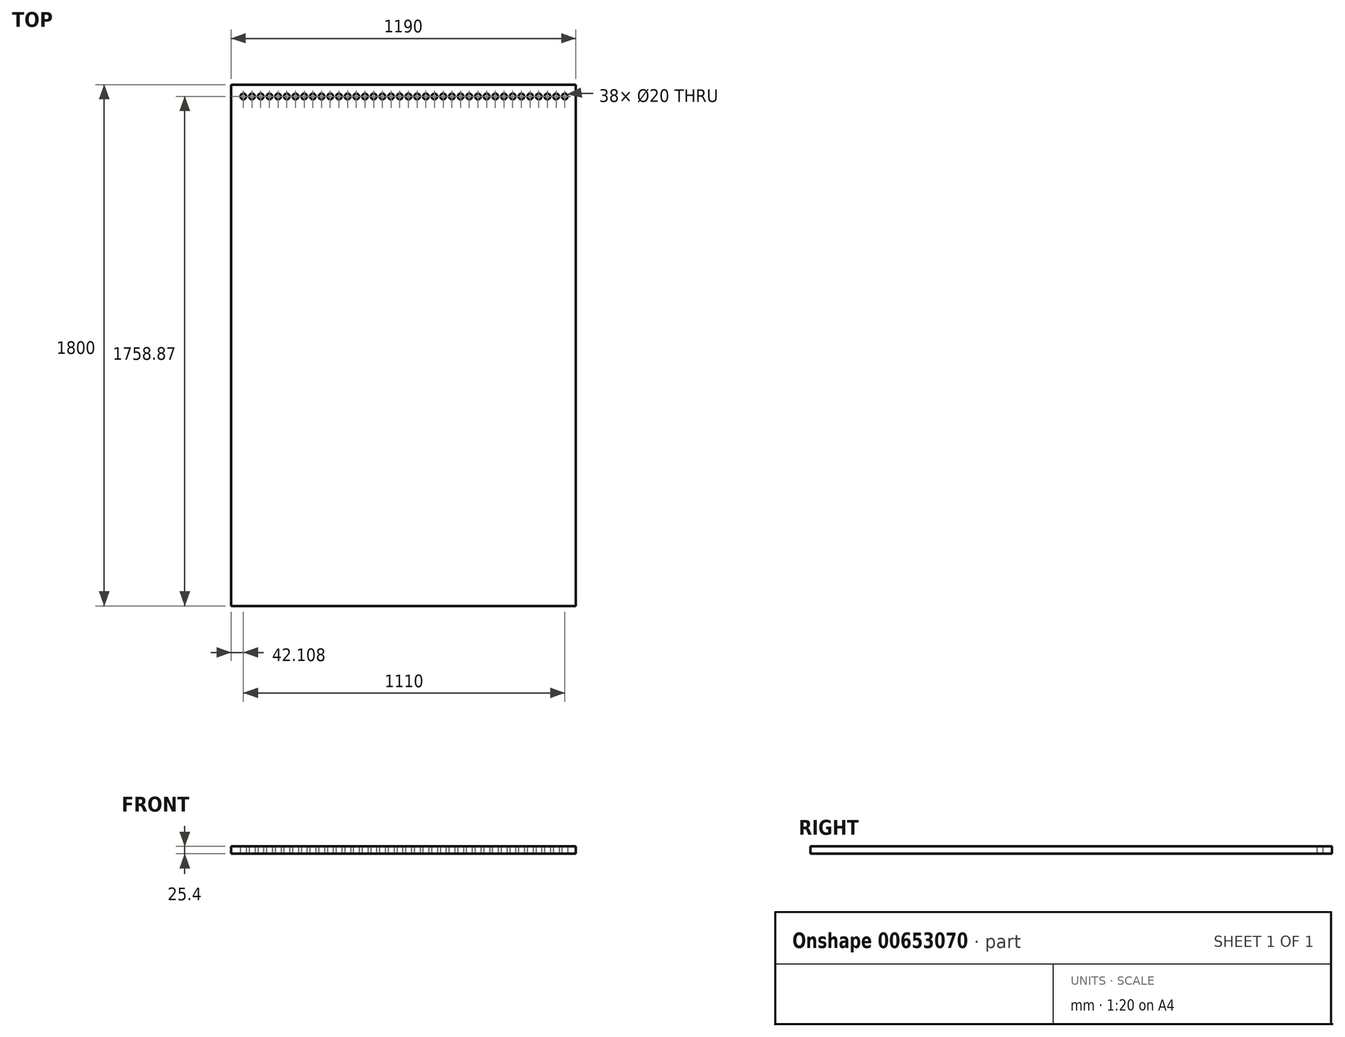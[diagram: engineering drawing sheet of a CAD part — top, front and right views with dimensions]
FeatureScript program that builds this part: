
annotation { "Feature Type Name" : "Feature", "Feature Type Description" : "" }
export const myFeature = defineFeature(function(context is Context, id is Id, definition is map)
    precondition{}
    {
        {
            var Q0;
            Q0=qCreatedBy(makeId("Front.planeOp"),FACE);
            var sketch = newSketch(context, id + "F0", { "sketchPlane" : qUnion([Q0])});
            skLineSegment(sketch, "E0.bottom", {"start": v(0, 0) * mm, "end": v(1190, 0) * mm});
            skLineSegment(sketch, "E0.top", {"start": v(0, 25.4) * mm, "end": v(1190, 25.4) * mm});
            skLineSegment(sketch, "E0.left", {"start": v(0, 0) * mm, "end": v(0, 25.4) * mm});
            skLineSegment(sketch, "E0.right", {"start": v(1190, 0) * mm, "end": v(1190, 25.4) * mm});
            skSolve(sketch);
        }
        {
            var Q0;
            Q0 = qSketchRegion(id + "F0", true);
            extrude(context, id + "F1", {"entities" : qUnion([Q0]), "depth" : 1800 * mm, "offsetDistance" : 25 * mm});
        }
        {
            var Q0;
            Q0=qCreatedBy(makeId("Top.planeOp"),FACE);
            var sketch = newSketch(context, id + "F2", { "sketchPlane" : qUnion([Q0])});
            skPoint(sketch, "E1", {"position": v(42.1, -41.13) * mm});
            skPoint(sketch, "E2.0.1.0", {"position": v(42.1, -66.13) * mm});
            skPoint(sketch, "E2.0.2.0", {"position": v(42.1, -91.13) * mm});
            skPoint(sketch, "E2.0.3.0", {"position": v(42.1, -116.13) * mm});
            skPoint(sketch, "E2.0.4.0", {"position": v(42.1, -141.13) * mm});
            skPoint(sketch, "E2.0.5.0", {"position": v(42.1, -166.13) * mm});
            skPoint(sketch, "E2.0.6.0", {"position": v(42.1, -191.13) * mm});
            skPoint(sketch, "E2.0.7.0", {"position": v(42.1, -216.13) * mm});
            skPoint(sketch, "E2.0.8.0", {"position": v(42.1, -241.13) * mm});
            skPoint(sketch, "E2.0.9.0", {"position": v(42.1, -266.13) * mm});
            skPoint(sketch, "E2.0.10.0", {"position": v(42.1, -291.13) * mm});
            skPoint(sketch, "E2.0.11.0", {"position": v(42.1, -316.13) * mm});
            skPoint(sketch, "E2.0.12.0", {"position": v(42.1, -341.13) * mm});
            skPoint(sketch, "E2.0.13.0", {"position": v(42.1, -366.13) * mm});
            skPoint(sketch, "E2.0.14.0", {"position": v(42.1, -391.13) * mm});
            skPoint(sketch, "E2.0.15.0", {"position": v(42.1, -416.13) * mm});
            skPoint(sketch, "E2.0.16.0", {"position": v(42.1, -441.13) * mm});
            skPoint(sketch, "E2.0.17.0", {"position": v(42.1, -466.13) * mm});
            skPoint(sketch, "E2.0.18.0", {"position": v(42.1, -491.13) * mm});
            skPoint(sketch, "E2.0.19.0", {"position": v(42.1, -516.13) * mm});
            skPoint(sketch, "E2.0.20.0", {"position": v(42.1, -541.13) * mm});
            skPoint(sketch, "E2.0.21.0", {"position": v(42.1, -566.13) * mm});
            skPoint(sketch, "E2.0.22.0", {"position": v(42.1, -591.13) * mm});
            skPoint(sketch, "E2.0.23.0", {"position": v(42.1, -616.13) * mm});
            skPoint(sketch, "E2.0.24.0", {"position": v(42.1, -641.13) * mm});
            skPoint(sketch, "E2.0.25.0", {"position": v(42.1, -666.13) * mm});
            skPoint(sketch, "E2.0.26.0", {"position": v(42.1, -691.13) * mm});
            skPoint(sketch, "E2.0.27.0", {"position": v(42.1, -716.13) * mm});
            skPoint(sketch, "E2.0.28.0", {"position": v(42.1, -741.13) * mm});
            skPoint(sketch, "E2.0.29.0", {"position": v(42.1, -766.13) * mm});
            skPoint(sketch, "E2.0.30.0", {"position": v(42.1, -791.13) * mm});
            skPoint(sketch, "E2.0.31.0", {"position": v(42.1, -816.13) * mm});
            skPoint(sketch, "E2.0.32.0", {"position": v(42.1, -841.13) * mm});
            skPoint(sketch, "E2.0.33.0", {"position": v(42.1, -866.13) * mm});
            skPoint(sketch, "E2.0.34.0", {"position": v(42.1, -891.13) * mm});
            skPoint(sketch, "E2.0.35.0", {"position": v(42.1, -916.13) * mm});
            skPoint(sketch, "E2.0.36.0", {"position": v(42.1, -941.13) * mm});
            skPoint(sketch, "E2.0.37.0", {"position": v(42.1, -966.13) * mm});
            skPoint(sketch, "E2.0.38.0", {"position": v(42.1, -991.13) * mm});
            skPoint(sketch, "E2.0.39.0", {"position": v(42.1, -1016.13) * mm});
            skPoint(sketch, "E2.0.40.0", {"position": v(42.1, -1041.13) * mm});
            skPoint(sketch, "E2.0.41.0", {"position": v(42.1, -1066.13) * mm});
            skPoint(sketch, "E2.0.42.0", {"position": v(42.1, -1091.13) * mm});
            skPoint(sketch, "E2.0.43.0", {"position": v(42.1, -1116.13) * mm});
            skPoint(sketch, "E2.0.44.0", {"position": v(42.1, -1141.13) * mm});
            skPoint(sketch, "E2.0.45.0", {"position": v(42.1, -1166.13) * mm});
            skPoint(sketch, "E2.0.46.0", {"position": v(42.1, -1191.13) * mm});
            skPoint(sketch, "E2.0.47.0", {"position": v(42.1, -1216.13) * mm});
            skPoint(sketch, "E2.0.48.0", {"position": v(42.1, -1241.13) * mm});
            skPoint(sketch, "E2.0.49.0", {"position": v(42.1, -1266.13) * mm});
            skPoint(sketch, "E2.0.50.0", {"position": v(42.1, -1291.13) * mm});
            skPoint(sketch, "E2.0.51.0", {"position": v(42.1, -1316.13) * mm});
            skPoint(sketch, "E2.0.52.0", {"position": v(42.1, -1341.13) * mm});
            skPoint(sketch, "E2.0.53.0", {"position": v(42.1, -1366.13) * mm});
            skPoint(sketch, "E2.0.54.0", {"position": v(42.1, -1391.13) * mm});
            skPoint(sketch, "E2.0.55.0", {"position": v(42.1, -1416.13) * mm});
            skPoint(sketch, "E2.0.56.0", {"position": v(42.1, -1441.13) * mm});
            skPoint(sketch, "E2.0.57.0", {"position": v(42.1, -1466.13) * mm});
            skPoint(sketch, "E2.0.58.0", {"position": v(42.1, -1491.13) * mm});
            skPoint(sketch, "E2.0.59.0", {"position": v(42.1, -1516.13) * mm});
            skPoint(sketch, "E2.0.60.0", {"position": v(42.1, -1541.13) * mm});
            skPoint(sketch, "E2.0.61.0", {"position": v(42.1, -1566.13) * mm});
            skPoint(sketch, "E2.0.62.0", {"position": v(42.1, -1591.13) * mm});
            skPoint(sketch, "E2.0.63.0", {"position": v(42.1, -1616.13) * mm});
            skPoint(sketch, "E2.0.64.0", {"position": v(42.1, -1641.13) * mm});
            skPoint(sketch, "E2.0.65.0", {"position": v(42.1, -1666.13) * mm});
            skPoint(sketch, "E2.0.66.0", {"position": v(42.1, -1691.13) * mm});
            skPoint(sketch, "E2.0.67.0", {"position": v(42.1, -1716.13) * mm});
            skPoint(sketch, "E2.0.68.0", {"position": v(42.1, -1741.13) * mm});
            skPoint(sketch, "E2.1.0.0", {"position": v(72.1, -41.13) * mm});
            skPoint(sketch, "E2.1.1.0", {"position": v(72.1, -66.13) * mm});
            skPoint(sketch, "E2.1.2.0", {"position": v(72.1, -91.13) * mm});
            skPoint(sketch, "E2.1.3.0", {"position": v(72.1, -116.13) * mm});
            skPoint(sketch, "E2.1.4.0", {"position": v(72.1, -141.13) * mm});
            skPoint(sketch, "E2.1.5.0", {"position": v(72.1, -166.13) * mm});
            skPoint(sketch, "E2.1.6.0", {"position": v(72.1, -191.13) * mm});
            skPoint(sketch, "E2.1.7.0", {"position": v(72.1, -216.13) * mm});
            skPoint(sketch, "E2.1.8.0", {"position": v(72.1, -241.13) * mm});
            skPoint(sketch, "E2.1.9.0", {"position": v(72.1, -266.13) * mm});
            skPoint(sketch, "E2.1.10.0", {"position": v(72.1, -291.13) * mm});
            skPoint(sketch, "E2.1.11.0", {"position": v(72.1, -316.13) * mm});
            skPoint(sketch, "E2.1.12.0", {"position": v(72.1, -341.13) * mm});
            skPoint(sketch, "E2.1.13.0", {"position": v(72.1, -366.13) * mm});
            skPoint(sketch, "E2.1.14.0", {"position": v(72.1, -391.13) * mm});
            skPoint(sketch, "E2.1.15.0", {"position": v(72.1, -416.13) * mm});
            skPoint(sketch, "E2.1.16.0", {"position": v(72.1, -441.13) * mm});
            skPoint(sketch, "E2.1.17.0", {"position": v(72.1, -466.13) * mm});
            skPoint(sketch, "E2.1.18.0", {"position": v(72.1, -491.13) * mm});
            skPoint(sketch, "E2.1.19.0", {"position": v(72.1, -516.13) * mm});
            skPoint(sketch, "E2.1.20.0", {"position": v(72.1, -541.13) * mm});
            skPoint(sketch, "E2.1.21.0", {"position": v(72.1, -566.13) * mm});
            skPoint(sketch, "E2.1.22.0", {"position": v(72.1, -591.13) * mm});
            skPoint(sketch, "E2.1.23.0", {"position": v(72.1, -616.13) * mm});
            skPoint(sketch, "E2.1.24.0", {"position": v(72.1, -641.13) * mm});
            skPoint(sketch, "E2.1.25.0", {"position": v(72.1, -666.13) * mm});
            skPoint(sketch, "E2.1.26.0", {"position": v(72.1, -691.13) * mm});
            skPoint(sketch, "E2.1.27.0", {"position": v(72.1, -716.13) * mm});
            skPoint(sketch, "E2.1.28.0", {"position": v(72.1, -741.13) * mm});
            skPoint(sketch, "E2.1.29.0", {"position": v(72.1, -766.13) * mm});
            skPoint(sketch, "E2.1.30.0", {"position": v(72.1, -791.13) * mm});
            skPoint(sketch, "E2.1.31.0", {"position": v(72.1, -816.13) * mm});
            skPoint(sketch, "E2.1.32.0", {"position": v(72.1, -841.13) * mm});
            skPoint(sketch, "E2.1.33.0", {"position": v(72.1, -866.13) * mm});
            skPoint(sketch, "E2.1.34.0", {"position": v(72.1, -891.13) * mm});
            skPoint(sketch, "E2.1.35.0", {"position": v(72.1, -916.13) * mm});
            skPoint(sketch, "E2.1.36.0", {"position": v(72.1, -941.13) * mm});
            skPoint(sketch, "E2.1.37.0", {"position": v(72.1, -966.13) * mm});
            skPoint(sketch, "E2.1.38.0", {"position": v(72.1, -991.13) * mm});
            skPoint(sketch, "E2.1.39.0", {"position": v(72.1, -1016.13) * mm});
            skPoint(sketch, "E2.1.40.0", {"position": v(72.1, -1041.13) * mm});
            skPoint(sketch, "E2.1.41.0", {"position": v(72.1, -1066.13) * mm});
            skPoint(sketch, "E2.1.42.0", {"position": v(72.1, -1091.13) * mm});
            skPoint(sketch, "E2.1.43.0", {"position": v(72.1, -1116.13) * mm});
            skPoint(sketch, "E2.1.44.0", {"position": v(72.1, -1141.13) * mm});
            skPoint(sketch, "E2.1.45.0", {"position": v(72.1, -1166.13) * mm});
            skPoint(sketch, "E2.1.46.0", {"position": v(72.1, -1191.13) * mm});
            skPoint(sketch, "E2.1.47.0", {"position": v(72.1, -1216.13) * mm});
            skPoint(sketch, "E2.1.48.0", {"position": v(72.1, -1241.13) * mm});
            skPoint(sketch, "E2.1.49.0", {"position": v(72.1, -1266.13) * mm});
            skPoint(sketch, "E2.1.50.0", {"position": v(72.1, -1291.13) * mm});
            skPoint(sketch, "E2.1.51.0", {"position": v(72.1, -1316.13) * mm});
            skPoint(sketch, "E2.1.52.0", {"position": v(72.1, -1341.13) * mm});
            skPoint(sketch, "E2.1.53.0", {"position": v(72.1, -1366.13) * mm});
            skPoint(sketch, "E2.1.54.0", {"position": v(72.1, -1391.13) * mm});
            skPoint(sketch, "E2.1.55.0", {"position": v(72.1, -1416.13) * mm});
            skPoint(sketch, "E2.1.56.0", {"position": v(72.1, -1441.13) * mm});
            skPoint(sketch, "E2.1.57.0", {"position": v(72.1, -1466.13) * mm});
            skPoint(sketch, "E2.1.58.0", {"position": v(72.1, -1491.13) * mm});
            skPoint(sketch, "E2.1.59.0", {"position": v(72.1, -1516.13) * mm});
            skPoint(sketch, "E2.1.60.0", {"position": v(72.1, -1541.13) * mm});
            skPoint(sketch, "E2.1.61.0", {"position": v(72.1, -1566.13) * mm});
            skPoint(sketch, "E2.1.62.0", {"position": v(72.1, -1591.13) * mm});
            skPoint(sketch, "E2.1.63.0", {"position": v(72.1, -1616.13) * mm});
            skPoint(sketch, "E2.1.64.0", {"position": v(72.1, -1641.13) * mm});
            skPoint(sketch, "E2.1.65.0", {"position": v(72.1, -1666.13) * mm});
            skPoint(sketch, "E2.1.66.0", {"position": v(72.1, -1691.13) * mm});
            skPoint(sketch, "E2.1.67.0", {"position": v(72.1, -1716.13) * mm});
            skPoint(sketch, "E2.1.68.0", {"position": v(72.1, -1741.13) * mm});
            skPoint(sketch, "E2.2.0.0", {"position": v(102.1, -41.13) * mm});
            skPoint(sketch, "E2.2.1.0", {"position": v(102.1, -66.13) * mm});
            skPoint(sketch, "E2.2.2.0", {"position": v(102.1, -91.13) * mm});
            skPoint(sketch, "E2.2.3.0", {"position": v(102.1, -116.13) * mm});
            skPoint(sketch, "E2.2.4.0", {"position": v(102.1, -141.13) * mm});
            skPoint(sketch, "E2.2.5.0", {"position": v(102.1, -166.13) * mm});
            skPoint(sketch, "E2.2.6.0", {"position": v(102.1, -191.13) * mm});
            skPoint(sketch, "E2.2.7.0", {"position": v(102.1, -216.13) * mm});
            skPoint(sketch, "E2.2.8.0", {"position": v(102.1, -241.13) * mm});
            skPoint(sketch, "E2.2.9.0", {"position": v(102.1, -266.13) * mm});
            skPoint(sketch, "E2.2.10.0", {"position": v(102.1, -291.13) * mm});
            skPoint(sketch, "E2.2.11.0", {"position": v(102.1, -316.13) * mm});
            skPoint(sketch, "E2.2.12.0", {"position": v(102.1, -341.13) * mm});
            skPoint(sketch, "E2.2.13.0", {"position": v(102.1, -366.13) * mm});
            skPoint(sketch, "E2.2.14.0", {"position": v(102.1, -391.13) * mm});
            skPoint(sketch, "E2.2.15.0", {"position": v(102.1, -416.13) * mm});
            skPoint(sketch, "E2.2.16.0", {"position": v(102.1, -441.13) * mm});
            skPoint(sketch, "E2.2.17.0", {"position": v(102.1, -466.13) * mm});
            skPoint(sketch, "E2.2.18.0", {"position": v(102.1, -491.13) * mm});
            skPoint(sketch, "E2.2.19.0", {"position": v(102.1, -516.13) * mm});
            skPoint(sketch, "E2.2.20.0", {"position": v(102.1, -541.13) * mm});
            skPoint(sketch, "E2.2.21.0", {"position": v(102.1, -566.13) * mm});
            skPoint(sketch, "E2.2.22.0", {"position": v(102.1, -591.13) * mm});
            skPoint(sketch, "E2.2.23.0", {"position": v(102.1, -616.13) * mm});
            skPoint(sketch, "E2.2.24.0", {"position": v(102.1, -641.13) * mm});
            skPoint(sketch, "E2.2.25.0", {"position": v(102.1, -666.13) * mm});
            skPoint(sketch, "E2.2.26.0", {"position": v(102.1, -691.13) * mm});
            skPoint(sketch, "E2.2.27.0", {"position": v(102.1, -716.13) * mm});
            skPoint(sketch, "E2.2.28.0", {"position": v(102.1, -741.13) * mm});
            skPoint(sketch, "E2.2.29.0", {"position": v(102.1, -766.13) * mm});
            skPoint(sketch, "E2.2.30.0", {"position": v(102.1, -791.13) * mm});
            skPoint(sketch, "E2.2.31.0", {"position": v(102.1, -816.13) * mm});
            skPoint(sketch, "E2.2.32.0", {"position": v(102.1, -841.13) * mm});
            skPoint(sketch, "E2.2.33.0", {"position": v(102.1, -866.13) * mm});
            skPoint(sketch, "E2.2.34.0", {"position": v(102.1, -891.13) * mm});
            skPoint(sketch, "E2.2.35.0", {"position": v(102.1, -916.13) * mm});
            skPoint(sketch, "E2.2.36.0", {"position": v(102.1, -941.13) * mm});
            skPoint(sketch, "E2.2.37.0", {"position": v(102.1, -966.13) * mm});
            skPoint(sketch, "E2.2.38.0", {"position": v(102.1, -991.13) * mm});
            skPoint(sketch, "E2.2.39.0", {"position": v(102.1, -1016.13) * mm});
            skPoint(sketch, "E2.2.40.0", {"position": v(102.1, -1041.13) * mm});
            skPoint(sketch, "E2.2.41.0", {"position": v(102.1, -1066.13) * mm});
            skPoint(sketch, "E2.2.42.0", {"position": v(102.1, -1091.13) * mm});
            skPoint(sketch, "E2.2.43.0", {"position": v(102.1, -1116.13) * mm});
            skPoint(sketch, "E2.2.44.0", {"position": v(102.1, -1141.13) * mm});
            skPoint(sketch, "E2.2.45.0", {"position": v(102.1, -1166.13) * mm});
            skPoint(sketch, "E2.2.46.0", {"position": v(102.1, -1191.13) * mm});
            skPoint(sketch, "E2.2.47.0", {"position": v(102.1, -1216.13) * mm});
            skPoint(sketch, "E2.2.48.0", {"position": v(102.1, -1241.13) * mm});
            skPoint(sketch, "E2.2.49.0", {"position": v(102.1, -1266.13) * mm});
            skPoint(sketch, "E2.2.50.0", {"position": v(102.1, -1291.13) * mm});
            skPoint(sketch, "E2.2.51.0", {"position": v(102.1, -1316.13) * mm});
            skPoint(sketch, "E2.2.52.0", {"position": v(102.1, -1341.13) * mm});
            skPoint(sketch, "E2.2.53.0", {"position": v(102.1, -1366.13) * mm});
            skPoint(sketch, "E2.2.54.0", {"position": v(102.1, -1391.13) * mm});
            skPoint(sketch, "E2.2.55.0", {"position": v(102.1, -1416.13) * mm});
            skPoint(sketch, "E2.2.56.0", {"position": v(102.1, -1441.13) * mm});
            skPoint(sketch, "E2.2.57.0", {"position": v(102.1, -1466.13) * mm});
            skPoint(sketch, "E2.2.58.0", {"position": v(102.1, -1491.13) * mm});
            skPoint(sketch, "E2.2.59.0", {"position": v(102.1, -1516.13) * mm});
            skPoint(sketch, "E2.2.60.0", {"position": v(102.1, -1541.13) * mm});
            skPoint(sketch, "E2.2.61.0", {"position": v(102.1, -1566.13) * mm});
            skPoint(sketch, "E2.2.62.0", {"position": v(102.1, -1591.13) * mm});
            skPoint(sketch, "E2.2.63.0", {"position": v(102.1, -1616.13) * mm});
            skPoint(sketch, "E2.2.64.0", {"position": v(102.1, -1641.13) * mm});
            skPoint(sketch, "E2.2.65.0", {"position": v(102.1, -1666.13) * mm});
            skPoint(sketch, "E2.2.66.0", {"position": v(102.1, -1691.13) * mm});
            skPoint(sketch, "E2.2.67.0", {"position": v(102.1, -1716.13) * mm});
            skPoint(sketch, "E2.2.68.0", {"position": v(102.1, -1741.13) * mm});
            skPoint(sketch, "E2.3.0.0", {"position": v(132.1, -41.13) * mm});
            skPoint(sketch, "E2.3.1.0", {"position": v(132.1, -66.13) * mm});
            skPoint(sketch, "E2.3.2.0", {"position": v(132.1, -91.13) * mm});
            skPoint(sketch, "E2.3.3.0", {"position": v(132.1, -116.13) * mm});
            skPoint(sketch, "E2.3.4.0", {"position": v(132.1, -141.13) * mm});
            skPoint(sketch, "E2.3.5.0", {"position": v(132.1, -166.13) * mm});
            skPoint(sketch, "E2.3.6.0", {"position": v(132.1, -191.13) * mm});
            skPoint(sketch, "E2.3.7.0", {"position": v(132.1, -216.13) * mm});
            skPoint(sketch, "E2.3.8.0", {"position": v(132.1, -241.13) * mm});
            skPoint(sketch, "E2.3.9.0", {"position": v(132.1, -266.13) * mm});
            skPoint(sketch, "E2.3.10.0", {"position": v(132.1, -291.13) * mm});
            skPoint(sketch, "E2.3.11.0", {"position": v(132.1, -316.13) * mm});
            skPoint(sketch, "E2.3.12.0", {"position": v(132.1, -341.13) * mm});
            skPoint(sketch, "E2.3.13.0", {"position": v(132.1, -366.13) * mm});
            skPoint(sketch, "E2.3.14.0", {"position": v(132.1, -391.13) * mm});
            skPoint(sketch, "E2.3.15.0", {"position": v(132.1, -416.13) * mm});
            skPoint(sketch, "E2.3.16.0", {"position": v(132.1, -441.13) * mm});
            skPoint(sketch, "E2.3.17.0", {"position": v(132.1, -466.13) * mm});
            skPoint(sketch, "E2.3.18.0", {"position": v(132.1, -491.13) * mm});
            skPoint(sketch, "E2.3.19.0", {"position": v(132.1, -516.13) * mm});
            skPoint(sketch, "E2.3.20.0", {"position": v(132.1, -541.13) * mm});
            skPoint(sketch, "E2.3.21.0", {"position": v(132.1, -566.13) * mm});
            skPoint(sketch, "E2.3.22.0", {"position": v(132.1, -591.13) * mm});
            skPoint(sketch, "E2.3.23.0", {"position": v(132.1, -616.13) * mm});
            skPoint(sketch, "E2.3.24.0", {"position": v(132.1, -641.13) * mm});
            skPoint(sketch, "E2.3.25.0", {"position": v(132.1, -666.13) * mm});
            skPoint(sketch, "E2.3.26.0", {"position": v(132.1, -691.13) * mm});
            skPoint(sketch, "E2.3.27.0", {"position": v(132.1, -716.13) * mm});
            skPoint(sketch, "E2.3.28.0", {"position": v(132.1, -741.13) * mm});
            skPoint(sketch, "E2.3.29.0", {"position": v(132.1, -766.13) * mm});
            skPoint(sketch, "E2.3.30.0", {"position": v(132.1, -791.13) * mm});
            skPoint(sketch, "E2.3.31.0", {"position": v(132.1, -816.13) * mm});
            skPoint(sketch, "E2.3.32.0", {"position": v(132.1, -841.13) * mm});
            skPoint(sketch, "E2.3.33.0", {"position": v(132.1, -866.13) * mm});
            skPoint(sketch, "E2.3.34.0", {"position": v(132.1, -891.13) * mm});
            skPoint(sketch, "E2.3.35.0", {"position": v(132.1, -916.13) * mm});
            skPoint(sketch, "E2.3.36.0", {"position": v(132.1, -941.13) * mm});
            skPoint(sketch, "E2.3.37.0", {"position": v(132.1, -966.13) * mm});
            skPoint(sketch, "E2.3.38.0", {"position": v(132.1, -991.13) * mm});
            skPoint(sketch, "E2.3.39.0", {"position": v(132.1, -1016.13) * mm});
            skPoint(sketch, "E2.3.40.0", {"position": v(132.1, -1041.13) * mm});
            skPoint(sketch, "E2.3.41.0", {"position": v(132.1, -1066.13) * mm});
            skPoint(sketch, "E2.3.42.0", {"position": v(132.1, -1091.13) * mm});
            skPoint(sketch, "E2.3.43.0", {"position": v(132.1, -1116.13) * mm});
            skPoint(sketch, "E2.3.44.0", {"position": v(132.1, -1141.13) * mm});
            skPoint(sketch, "E2.3.45.0", {"position": v(132.1, -1166.13) * mm});
            skPoint(sketch, "E2.3.46.0", {"position": v(132.1, -1191.13) * mm});
            skPoint(sketch, "E2.3.47.0", {"position": v(132.1, -1216.13) * mm});
            skPoint(sketch, "E2.3.48.0", {"position": v(132.1, -1241.13) * mm});
            skPoint(sketch, "E2.3.49.0", {"position": v(132.1, -1266.13) * mm});
            skPoint(sketch, "E2.3.50.0", {"position": v(132.1, -1291.13) * mm});
            skPoint(sketch, "E2.3.51.0", {"position": v(132.1, -1316.13) * mm});
            skPoint(sketch, "E2.3.52.0", {"position": v(132.1, -1341.13) * mm});
            skPoint(sketch, "E2.3.53.0", {"position": v(132.1, -1366.13) * mm});
            skPoint(sketch, "E2.3.54.0", {"position": v(132.1, -1391.13) * mm});
            skPoint(sketch, "E2.3.55.0", {"position": v(132.1, -1416.13) * mm});
            skPoint(sketch, "E2.3.56.0", {"position": v(132.1, -1441.13) * mm});
            skPoint(sketch, "E2.3.57.0", {"position": v(132.1, -1466.13) * mm});
            skPoint(sketch, "E2.3.58.0", {"position": v(132.1, -1491.13) * mm});
            skPoint(sketch, "E2.3.59.0", {"position": v(132.1, -1516.13) * mm});
            skPoint(sketch, "E2.3.60.0", {"position": v(132.1, -1541.13) * mm});
            skPoint(sketch, "E2.3.61.0", {"position": v(132.1, -1566.13) * mm});
            skPoint(sketch, "E2.3.62.0", {"position": v(132.1, -1591.13) * mm});
            skPoint(sketch, "E2.3.63.0", {"position": v(132.1, -1616.13) * mm});
            skPoint(sketch, "E2.3.64.0", {"position": v(132.1, -1641.13) * mm});
            skPoint(sketch, "E2.3.65.0", {"position": v(132.1, -1666.13) * mm});
            skPoint(sketch, "E2.3.66.0", {"position": v(132.1, -1691.13) * mm});
            skPoint(sketch, "E2.3.67.0", {"position": v(132.1, -1716.13) * mm});
            skPoint(sketch, "E2.3.68.0", {"position": v(132.1, -1741.13) * mm});
            skPoint(sketch, "E2.4.0.0", {"position": v(162.1, -41.13) * mm});
            skPoint(sketch, "E2.4.1.0", {"position": v(162.1, -66.13) * mm});
            skPoint(sketch, "E2.4.2.0", {"position": v(162.1, -91.13) * mm});
            skPoint(sketch, "E2.4.3.0", {"position": v(162.1, -116.13) * mm});
            skPoint(sketch, "E2.4.4.0", {"position": v(162.1, -141.13) * mm});
            skPoint(sketch, "E2.4.5.0", {"position": v(162.1, -166.13) * mm});
            skPoint(sketch, "E2.4.6.0", {"position": v(162.1, -191.13) * mm});
            skPoint(sketch, "E2.4.7.0", {"position": v(162.1, -216.13) * mm});
            skPoint(sketch, "E2.4.8.0", {"position": v(162.1, -241.13) * mm});
            skPoint(sketch, "E2.4.9.0", {"position": v(162.1, -266.13) * mm});
            skPoint(sketch, "E2.4.10.0", {"position": v(162.1, -291.13) * mm});
            skPoint(sketch, "E2.4.11.0", {"position": v(162.1, -316.13) * mm});
            skPoint(sketch, "E2.4.12.0", {"position": v(162.1, -341.13) * mm});
            skPoint(sketch, "E2.4.13.0", {"position": v(162.1, -366.13) * mm});
            skPoint(sketch, "E2.4.14.0", {"position": v(162.1, -391.13) * mm});
            skPoint(sketch, "E2.4.15.0", {"position": v(162.1, -416.13) * mm});
            skPoint(sketch, "E2.4.16.0", {"position": v(162.1, -441.13) * mm});
            skPoint(sketch, "E2.4.17.0", {"position": v(162.1, -466.13) * mm});
            skPoint(sketch, "E2.4.18.0", {"position": v(162.1, -491.13) * mm});
            skPoint(sketch, "E2.4.19.0", {"position": v(162.1, -516.13) * mm});
            skPoint(sketch, "E2.4.20.0", {"position": v(162.1, -541.13) * mm});
            skPoint(sketch, "E2.4.21.0", {"position": v(162.1, -566.13) * mm});
            skPoint(sketch, "E2.4.22.0", {"position": v(162.1, -591.13) * mm});
            skPoint(sketch, "E2.4.23.0", {"position": v(162.1, -616.13) * mm});
            skPoint(sketch, "E2.4.24.0", {"position": v(162.1, -641.13) * mm});
            skPoint(sketch, "E2.4.25.0", {"position": v(162.1, -666.13) * mm});
            skPoint(sketch, "E2.4.26.0", {"position": v(162.1, -691.13) * mm});
            skPoint(sketch, "E2.4.27.0", {"position": v(162.1, -716.13) * mm});
            skPoint(sketch, "E2.4.28.0", {"position": v(162.1, -741.13) * mm});
            skPoint(sketch, "E2.4.29.0", {"position": v(162.1, -766.13) * mm});
            skPoint(sketch, "E2.4.30.0", {"position": v(162.1, -791.13) * mm});
            skPoint(sketch, "E2.4.31.0", {"position": v(162.1, -816.13) * mm});
            skPoint(sketch, "E2.4.32.0", {"position": v(162.1, -841.13) * mm});
            skPoint(sketch, "E2.4.33.0", {"position": v(162.1, -866.13) * mm});
            skPoint(sketch, "E2.4.34.0", {"position": v(162.1, -891.13) * mm});
            skPoint(sketch, "E2.4.35.0", {"position": v(162.1, -916.13) * mm});
            skPoint(sketch, "E2.4.36.0", {"position": v(162.1, -941.13) * mm});
            skPoint(sketch, "E2.4.37.0", {"position": v(162.1, -966.13) * mm});
            skPoint(sketch, "E2.4.38.0", {"position": v(162.1, -991.13) * mm});
            skPoint(sketch, "E2.4.39.0", {"position": v(162.1, -1016.13) * mm});
            skPoint(sketch, "E2.4.40.0", {"position": v(162.1, -1041.13) * mm});
            skPoint(sketch, "E2.4.41.0", {"position": v(162.1, -1066.13) * mm});
            skPoint(sketch, "E2.4.42.0", {"position": v(162.1, -1091.13) * mm});
            skPoint(sketch, "E2.4.43.0", {"position": v(162.1, -1116.13) * mm});
            skPoint(sketch, "E2.4.44.0", {"position": v(162.1, -1141.13) * mm});
            skPoint(sketch, "E2.4.45.0", {"position": v(162.1, -1166.13) * mm});
            skPoint(sketch, "E2.4.46.0", {"position": v(162.1, -1191.13) * mm});
            skPoint(sketch, "E2.4.47.0", {"position": v(162.1, -1216.13) * mm});
            skPoint(sketch, "E2.4.48.0", {"position": v(162.1, -1241.13) * mm});
            skPoint(sketch, "E2.4.49.0", {"position": v(162.1, -1266.13) * mm});
            skPoint(sketch, "E2.4.50.0", {"position": v(162.1, -1291.13) * mm});
            skPoint(sketch, "E2.4.51.0", {"position": v(162.1, -1316.13) * mm});
            skPoint(sketch, "E2.4.52.0", {"position": v(162.1, -1341.13) * mm});
            skPoint(sketch, "E2.4.53.0", {"position": v(162.1, -1366.13) * mm});
            skPoint(sketch, "E2.4.54.0", {"position": v(162.1, -1391.13) * mm});
            skPoint(sketch, "E2.4.55.0", {"position": v(162.1, -1416.13) * mm});
            skPoint(sketch, "E2.4.56.0", {"position": v(162.1, -1441.13) * mm});
            skPoint(sketch, "E2.4.57.0", {"position": v(162.1, -1466.13) * mm});
            skPoint(sketch, "E2.4.58.0", {"position": v(162.1, -1491.13) * mm});
            skPoint(sketch, "E2.4.59.0", {"position": v(162.1, -1516.13) * mm});
            skPoint(sketch, "E2.4.60.0", {"position": v(162.1, -1541.13) * mm});
            skPoint(sketch, "E2.4.61.0", {"position": v(162.1, -1566.13) * mm});
            skPoint(sketch, "E2.4.62.0", {"position": v(162.1, -1591.13) * mm});
            skPoint(sketch, "E2.4.63.0", {"position": v(162.1, -1616.13) * mm});
            skPoint(sketch, "E2.4.64.0", {"position": v(162.1, -1641.13) * mm});
            skPoint(sketch, "E2.4.65.0", {"position": v(162.1, -1666.13) * mm});
            skPoint(sketch, "E2.4.66.0", {"position": v(162.1, -1691.13) * mm});
            skPoint(sketch, "E2.4.67.0", {"position": v(162.1, -1716.13) * mm});
            skPoint(sketch, "E2.4.68.0", {"position": v(162.1, -1741.13) * mm});
            skPoint(sketch, "E2.5.0.0", {"position": v(192.1, -41.13) * mm});
            skPoint(sketch, "E2.5.1.0", {"position": v(192.1, -66.13) * mm});
            skPoint(sketch, "E2.5.2.0", {"position": v(192.1, -91.13) * mm});
            skPoint(sketch, "E2.5.3.0", {"position": v(192.1, -116.13) * mm});
            skPoint(sketch, "E2.5.4.0", {"position": v(192.1, -141.13) * mm});
            skPoint(sketch, "E2.5.5.0", {"position": v(192.1, -166.13) * mm});
            skPoint(sketch, "E2.5.6.0", {"position": v(192.1, -191.13) * mm});
            skPoint(sketch, "E2.5.7.0", {"position": v(192.1, -216.13) * mm});
            skPoint(sketch, "E2.5.8.0", {"position": v(192.1, -241.13) * mm});
            skPoint(sketch, "E2.5.9.0", {"position": v(192.1, -266.13) * mm});
            skPoint(sketch, "E2.5.10.0", {"position": v(192.1, -291.13) * mm});
            skPoint(sketch, "E2.5.11.0", {"position": v(192.1, -316.13) * mm});
            skPoint(sketch, "E2.5.12.0", {"position": v(192.1, -341.13) * mm});
            skPoint(sketch, "E2.5.13.0", {"position": v(192.1, -366.13) * mm});
            skPoint(sketch, "E2.5.14.0", {"position": v(192.1, -391.13) * mm});
            skPoint(sketch, "E2.5.15.0", {"position": v(192.1, -416.13) * mm});
            skPoint(sketch, "E2.5.16.0", {"position": v(192.1, -441.13) * mm});
            skPoint(sketch, "E2.5.17.0", {"position": v(192.1, -466.13) * mm});
            skPoint(sketch, "E2.5.18.0", {"position": v(192.1, -491.13) * mm});
            skPoint(sketch, "E2.5.19.0", {"position": v(192.1, -516.13) * mm});
            skPoint(sketch, "E2.5.20.0", {"position": v(192.1, -541.13) * mm});
            skPoint(sketch, "E2.5.21.0", {"position": v(192.1, -566.13) * mm});
            skPoint(sketch, "E2.5.22.0", {"position": v(192.1, -591.13) * mm});
            skPoint(sketch, "E2.5.23.0", {"position": v(192.1, -616.13) * mm});
            skPoint(sketch, "E2.5.24.0", {"position": v(192.1, -641.13) * mm});
            skPoint(sketch, "E2.5.25.0", {"position": v(192.1, -666.13) * mm});
            skPoint(sketch, "E2.5.26.0", {"position": v(192.1, -691.13) * mm});
            skPoint(sketch, "E2.5.27.0", {"position": v(192.1, -716.13) * mm});
            skPoint(sketch, "E2.5.28.0", {"position": v(192.1, -741.13) * mm});
            skPoint(sketch, "E2.5.29.0", {"position": v(192.1, -766.13) * mm});
            skPoint(sketch, "E2.5.30.0", {"position": v(192.1, -791.13) * mm});
            skPoint(sketch, "E2.5.31.0", {"position": v(192.1, -816.13) * mm});
            skPoint(sketch, "E2.5.32.0", {"position": v(192.1, -841.13) * mm});
            skPoint(sketch, "E2.5.33.0", {"position": v(192.1, -866.13) * mm});
            skPoint(sketch, "E2.5.34.0", {"position": v(192.1, -891.13) * mm});
            skPoint(sketch, "E2.5.35.0", {"position": v(192.1, -916.13) * mm});
            skPoint(sketch, "E2.5.36.0", {"position": v(192.1, -941.13) * mm});
            skPoint(sketch, "E2.5.37.0", {"position": v(192.1, -966.13) * mm});
            skPoint(sketch, "E2.5.38.0", {"position": v(192.1, -991.13) * mm});
            skPoint(sketch, "E2.5.39.0", {"position": v(192.1, -1016.13) * mm});
            skPoint(sketch, "E2.5.40.0", {"position": v(192.1, -1041.13) * mm});
            skPoint(sketch, "E2.5.41.0", {"position": v(192.1, -1066.13) * mm});
            skPoint(sketch, "E2.5.42.0", {"position": v(192.1, -1091.13) * mm});
            skPoint(sketch, "E2.5.43.0", {"position": v(192.1, -1116.13) * mm});
            skPoint(sketch, "E2.5.44.0", {"position": v(192.1, -1141.13) * mm});
            skPoint(sketch, "E2.5.45.0", {"position": v(192.1, -1166.13) * mm});
            skPoint(sketch, "E2.5.46.0", {"position": v(192.1, -1191.13) * mm});
            skPoint(sketch, "E2.5.47.0", {"position": v(192.1, -1216.13) * mm});
            skPoint(sketch, "E2.5.48.0", {"position": v(192.1, -1241.13) * mm});
            skPoint(sketch, "E2.5.49.0", {"position": v(192.1, -1266.13) * mm});
            skPoint(sketch, "E2.5.50.0", {"position": v(192.1, -1291.13) * mm});
            skPoint(sketch, "E2.5.51.0", {"position": v(192.1, -1316.13) * mm});
            skPoint(sketch, "E2.5.52.0", {"position": v(192.1, -1341.13) * mm});
            skPoint(sketch, "E2.5.53.0", {"position": v(192.1, -1366.13) * mm});
            skPoint(sketch, "E2.5.54.0", {"position": v(192.1, -1391.13) * mm});
            skPoint(sketch, "E2.5.55.0", {"position": v(192.1, -1416.13) * mm});
            skPoint(sketch, "E2.5.56.0", {"position": v(192.1, -1441.13) * mm});
            skPoint(sketch, "E2.5.57.0", {"position": v(192.1, -1466.13) * mm});
            skPoint(sketch, "E2.5.58.0", {"position": v(192.1, -1491.13) * mm});
            skPoint(sketch, "E2.5.59.0", {"position": v(192.1, -1516.13) * mm});
            skPoint(sketch, "E2.5.60.0", {"position": v(192.1, -1541.13) * mm});
            skPoint(sketch, "E2.5.61.0", {"position": v(192.1, -1566.13) * mm});
            skPoint(sketch, "E2.5.62.0", {"position": v(192.1, -1591.13) * mm});
            skPoint(sketch, "E2.5.63.0", {"position": v(192.1, -1616.13) * mm});
            skPoint(sketch, "E2.5.64.0", {"position": v(192.1, -1641.13) * mm});
            skPoint(sketch, "E2.5.65.0", {"position": v(192.1, -1666.13) * mm});
            skPoint(sketch, "E2.5.66.0", {"position": v(192.1, -1691.13) * mm});
            skPoint(sketch, "E2.5.67.0", {"position": v(192.1, -1716.13) * mm});
            skPoint(sketch, "E2.5.68.0", {"position": v(192.1, -1741.13) * mm});
            skPoint(sketch, "E2.6.0.0", {"position": v(222.1, -41.13) * mm});
            skPoint(sketch, "E2.6.1.0", {"position": v(222.1, -66.13) * mm});
            skPoint(sketch, "E2.6.2.0", {"position": v(222.1, -91.13) * mm});
            skPoint(sketch, "E2.6.3.0", {"position": v(222.1, -116.13) * mm});
            skPoint(sketch, "E2.6.4.0", {"position": v(222.1, -141.13) * mm});
            skPoint(sketch, "E2.6.5.0", {"position": v(222.1, -166.13) * mm});
            skPoint(sketch, "E2.6.6.0", {"position": v(222.1, -191.13) * mm});
            skPoint(sketch, "E2.6.7.0", {"position": v(222.1, -216.13) * mm});
            skPoint(sketch, "E2.6.8.0", {"position": v(222.1, -241.13) * mm});
            skPoint(sketch, "E2.6.9.0", {"position": v(222.1, -266.13) * mm});
            skPoint(sketch, "E2.6.10.0", {"position": v(222.1, -291.13) * mm});
            skPoint(sketch, "E2.6.11.0", {"position": v(222.1, -316.13) * mm});
            skPoint(sketch, "E2.6.12.0", {"position": v(222.1, -341.13) * mm});
            skPoint(sketch, "E2.6.13.0", {"position": v(222.1, -366.13) * mm});
            skPoint(sketch, "E2.6.14.0", {"position": v(222.1, -391.13) * mm});
            skPoint(sketch, "E2.6.15.0", {"position": v(222.1, -416.13) * mm});
            skPoint(sketch, "E2.6.16.0", {"position": v(222.1, -441.13) * mm});
            skPoint(sketch, "E2.6.17.0", {"position": v(222.1, -466.13) * mm});
            skPoint(sketch, "E2.6.18.0", {"position": v(222.1, -491.13) * mm});
            skPoint(sketch, "E2.6.19.0", {"position": v(222.1, -516.13) * mm});
            skPoint(sketch, "E2.6.20.0", {"position": v(222.1, -541.13) * mm});
            skPoint(sketch, "E2.6.21.0", {"position": v(222.1, -566.13) * mm});
            skPoint(sketch, "E2.6.22.0", {"position": v(222.1, -591.13) * mm});
            skPoint(sketch, "E2.6.23.0", {"position": v(222.1, -616.13) * mm});
            skPoint(sketch, "E2.6.24.0", {"position": v(222.1, -641.13) * mm});
            skPoint(sketch, "E2.6.25.0", {"position": v(222.1, -666.13) * mm});
            skPoint(sketch, "E2.6.26.0", {"position": v(222.1, -691.13) * mm});
            skPoint(sketch, "E2.6.27.0", {"position": v(222.1, -716.13) * mm});
            skPoint(sketch, "E2.6.28.0", {"position": v(222.1, -741.13) * mm});
            skPoint(sketch, "E2.6.29.0", {"position": v(222.1, -766.13) * mm});
            skPoint(sketch, "E2.6.30.0", {"position": v(222.1, -791.13) * mm});
            skPoint(sketch, "E2.6.31.0", {"position": v(222.1, -816.13) * mm});
            skPoint(sketch, "E2.6.32.0", {"position": v(222.1, -841.13) * mm});
            skPoint(sketch, "E2.6.33.0", {"position": v(222.1, -866.13) * mm});
            skPoint(sketch, "E2.6.34.0", {"position": v(222.1, -891.13) * mm});
            skPoint(sketch, "E2.6.35.0", {"position": v(222.1, -916.13) * mm});
            skPoint(sketch, "E2.6.36.0", {"position": v(222.1, -941.13) * mm});
            skPoint(sketch, "E2.6.37.0", {"position": v(222.1, -966.13) * mm});
            skPoint(sketch, "E2.6.38.0", {"position": v(222.1, -991.13) * mm});
            skPoint(sketch, "E2.6.39.0", {"position": v(222.1, -1016.13) * mm});
            skPoint(sketch, "E2.6.40.0", {"position": v(222.1, -1041.13) * mm});
            skPoint(sketch, "E2.6.41.0", {"position": v(222.1, -1066.13) * mm});
            skPoint(sketch, "E2.6.42.0", {"position": v(222.1, -1091.13) * mm});
            skPoint(sketch, "E2.6.43.0", {"position": v(222.1, -1116.13) * mm});
            skPoint(sketch, "E2.6.44.0", {"position": v(222.1, -1141.13) * mm});
            skPoint(sketch, "E2.6.45.0", {"position": v(222.1, -1166.13) * mm});
            skPoint(sketch, "E2.6.46.0", {"position": v(222.1, -1191.13) * mm});
            skPoint(sketch, "E2.6.47.0", {"position": v(222.1, -1216.13) * mm});
            skPoint(sketch, "E2.6.48.0", {"position": v(222.1, -1241.13) * mm});
            skPoint(sketch, "E2.6.49.0", {"position": v(222.1, -1266.13) * mm});
            skPoint(sketch, "E2.6.50.0", {"position": v(222.1, -1291.13) * mm});
            skPoint(sketch, "E2.6.51.0", {"position": v(222.1, -1316.13) * mm});
            skPoint(sketch, "E2.6.52.0", {"position": v(222.1, -1341.13) * mm});
            skPoint(sketch, "E2.6.53.0", {"position": v(222.1, -1366.13) * mm});
            skPoint(sketch, "E2.6.54.0", {"position": v(222.1, -1391.13) * mm});
            skPoint(sketch, "E2.6.55.0", {"position": v(222.1, -1416.13) * mm});
            skPoint(sketch, "E2.6.56.0", {"position": v(222.1, -1441.13) * mm});
            skPoint(sketch, "E2.6.57.0", {"position": v(222.1, -1466.13) * mm});
            skPoint(sketch, "E2.6.58.0", {"position": v(222.1, -1491.13) * mm});
            skPoint(sketch, "E2.6.59.0", {"position": v(222.1, -1516.13) * mm});
            skPoint(sketch, "E2.6.60.0", {"position": v(222.1, -1541.13) * mm});
            skPoint(sketch, "E2.6.61.0", {"position": v(222.1, -1566.13) * mm});
            skPoint(sketch, "E2.6.62.0", {"position": v(222.1, -1591.13) * mm});
            skPoint(sketch, "E2.6.63.0", {"position": v(222.1, -1616.13) * mm});
            skPoint(sketch, "E2.6.64.0", {"position": v(222.1, -1641.13) * mm});
            skPoint(sketch, "E2.6.65.0", {"position": v(222.1, -1666.13) * mm});
            skPoint(sketch, "E2.6.66.0", {"position": v(222.1, -1691.13) * mm});
            skPoint(sketch, "E2.6.67.0", {"position": v(222.1, -1716.13) * mm});
            skPoint(sketch, "E2.6.68.0", {"position": v(222.1, -1741.13) * mm});
            skPoint(sketch, "E2.7.0.0", {"position": v(252.1, -41.13) * mm});
            skPoint(sketch, "E2.7.1.0", {"position": v(252.1, -66.13) * mm});
            skPoint(sketch, "E2.7.2.0", {"position": v(252.1, -91.13) * mm});
            skPoint(sketch, "E2.7.3.0", {"position": v(252.1, -116.13) * mm});
            skPoint(sketch, "E2.7.4.0", {"position": v(252.1, -141.13) * mm});
            skPoint(sketch, "E2.7.5.0", {"position": v(252.1, -166.13) * mm});
            skPoint(sketch, "E2.7.6.0", {"position": v(252.1, -191.13) * mm});
            skPoint(sketch, "E2.7.7.0", {"position": v(252.1, -216.13) * mm});
            skPoint(sketch, "E2.7.8.0", {"position": v(252.1, -241.13) * mm});
            skPoint(sketch, "E2.7.9.0", {"position": v(252.1, -266.13) * mm});
            skPoint(sketch, "E2.7.10.0", {"position": v(252.1, -291.13) * mm});
            skPoint(sketch, "E2.7.11.0", {"position": v(252.1, -316.13) * mm});
            skPoint(sketch, "E2.7.12.0", {"position": v(252.1, -341.13) * mm});
            skPoint(sketch, "E2.7.13.0", {"position": v(252.1, -366.13) * mm});
            skPoint(sketch, "E2.7.14.0", {"position": v(252.1, -391.13) * mm});
            skPoint(sketch, "E2.7.15.0", {"position": v(252.1, -416.13) * mm});
            skPoint(sketch, "E2.7.16.0", {"position": v(252.1, -441.13) * mm});
            skPoint(sketch, "E2.7.17.0", {"position": v(252.1, -466.13) * mm});
            skPoint(sketch, "E2.7.18.0", {"position": v(252.1, -491.13) * mm});
            skPoint(sketch, "E2.7.19.0", {"position": v(252.1, -516.13) * mm});
            skPoint(sketch, "E2.7.20.0", {"position": v(252.1, -541.13) * mm});
            skPoint(sketch, "E2.7.21.0", {"position": v(252.1, -566.13) * mm});
            skPoint(sketch, "E2.7.22.0", {"position": v(252.1, -591.13) * mm});
            skPoint(sketch, "E2.7.23.0", {"position": v(252.1, -616.13) * mm});
            skPoint(sketch, "E2.7.24.0", {"position": v(252.1, -641.13) * mm});
            skPoint(sketch, "E2.7.25.0", {"position": v(252.1, -666.13) * mm});
            skPoint(sketch, "E2.7.26.0", {"position": v(252.1, -691.13) * mm});
            skPoint(sketch, "E2.7.27.0", {"position": v(252.1, -716.13) * mm});
            skPoint(sketch, "E2.7.28.0", {"position": v(252.1, -741.13) * mm});
            skPoint(sketch, "E2.7.29.0", {"position": v(252.1, -766.13) * mm});
            skPoint(sketch, "E2.7.30.0", {"position": v(252.1, -791.13) * mm});
            skPoint(sketch, "E2.7.31.0", {"position": v(252.1, -816.13) * mm});
            skPoint(sketch, "E2.7.32.0", {"position": v(252.1, -841.13) * mm});
            skPoint(sketch, "E2.7.33.0", {"position": v(252.1, -866.13) * mm});
            skPoint(sketch, "E2.7.34.0", {"position": v(252.1, -891.13) * mm});
            skPoint(sketch, "E2.7.35.0", {"position": v(252.1, -916.13) * mm});
            skPoint(sketch, "E2.7.36.0", {"position": v(252.1, -941.13) * mm});
            skPoint(sketch, "E2.7.37.0", {"position": v(252.1, -966.13) * mm});
            skPoint(sketch, "E2.7.38.0", {"position": v(252.1, -991.13) * mm});
            skPoint(sketch, "E2.7.39.0", {"position": v(252.1, -1016.13) * mm});
            skPoint(sketch, "E2.7.40.0", {"position": v(252.1, -1041.13) * mm});
            skPoint(sketch, "E2.7.41.0", {"position": v(252.1, -1066.13) * mm});
            skPoint(sketch, "E2.7.42.0", {"position": v(252.1, -1091.13) * mm});
            skPoint(sketch, "E2.7.43.0", {"position": v(252.1, -1116.13) * mm});
            skPoint(sketch, "E2.7.44.0", {"position": v(252.1, -1141.13) * mm});
            skPoint(sketch, "E2.7.45.0", {"position": v(252.1, -1166.13) * mm});
            skPoint(sketch, "E2.7.46.0", {"position": v(252.1, -1191.13) * mm});
            skPoint(sketch, "E2.7.47.0", {"position": v(252.1, -1216.13) * mm});
            skPoint(sketch, "E2.7.48.0", {"position": v(252.1, -1241.13) * mm});
            skPoint(sketch, "E2.7.49.0", {"position": v(252.1, -1266.13) * mm});
            skPoint(sketch, "E2.7.50.0", {"position": v(252.1, -1291.13) * mm});
            skPoint(sketch, "E2.7.51.0", {"position": v(252.1, -1316.13) * mm});
            skPoint(sketch, "E2.7.52.0", {"position": v(252.1, -1341.13) * mm});
            skPoint(sketch, "E2.7.53.0", {"position": v(252.1, -1366.13) * mm});
            skPoint(sketch, "E2.7.54.0", {"position": v(252.1, -1391.13) * mm});
            skPoint(sketch, "E2.7.55.0", {"position": v(252.1, -1416.13) * mm});
            skPoint(sketch, "E2.7.56.0", {"position": v(252.1, -1441.13) * mm});
            skPoint(sketch, "E2.7.57.0", {"position": v(252.1, -1466.13) * mm});
            skPoint(sketch, "E2.7.58.0", {"position": v(252.1, -1491.13) * mm});
            skPoint(sketch, "E2.7.59.0", {"position": v(252.1, -1516.13) * mm});
            skPoint(sketch, "E2.7.60.0", {"position": v(252.1, -1541.13) * mm});
            skPoint(sketch, "E2.7.61.0", {"position": v(252.1, -1566.13) * mm});
            skPoint(sketch, "E2.7.62.0", {"position": v(252.1, -1591.13) * mm});
            skPoint(sketch, "E2.7.63.0", {"position": v(252.1, -1616.13) * mm});
            skPoint(sketch, "E2.7.64.0", {"position": v(252.1, -1641.13) * mm});
            skPoint(sketch, "E2.7.65.0", {"position": v(252.1, -1666.13) * mm});
            skPoint(sketch, "E2.7.66.0", {"position": v(252.1, -1691.13) * mm});
            skPoint(sketch, "E2.7.67.0", {"position": v(252.1, -1716.13) * mm});
            skPoint(sketch, "E2.7.68.0", {"position": v(252.1, -1741.13) * mm});
            skPoint(sketch, "E2.8.0.0", {"position": v(282.1, -41.13) * mm});
            skPoint(sketch, "E2.8.1.0", {"position": v(282.1, -66.13) * mm});
            skPoint(sketch, "E2.8.2.0", {"position": v(282.1, -91.13) * mm});
            skPoint(sketch, "E2.8.3.0", {"position": v(282.1, -116.13) * mm});
            skPoint(sketch, "E2.8.4.0", {"position": v(282.1, -141.13) * mm});
            skPoint(sketch, "E2.8.5.0", {"position": v(282.1, -166.13) * mm});
            skPoint(sketch, "E2.8.6.0", {"position": v(282.1, -191.13) * mm});
            skPoint(sketch, "E2.8.7.0", {"position": v(282.1, -216.13) * mm});
            skPoint(sketch, "E2.8.8.0", {"position": v(282.1, -241.13) * mm});
            skPoint(sketch, "E2.8.9.0", {"position": v(282.1, -266.13) * mm});
            skPoint(sketch, "E2.8.10.0", {"position": v(282.1, -291.13) * mm});
            skPoint(sketch, "E2.8.11.0", {"position": v(282.1, -316.13) * mm});
            skPoint(sketch, "E2.8.12.0", {"position": v(282.1, -341.13) * mm});
            skPoint(sketch, "E2.8.13.0", {"position": v(282.1, -366.13) * mm});
            skPoint(sketch, "E2.8.14.0", {"position": v(282.1, -391.13) * mm});
            skPoint(sketch, "E2.8.15.0", {"position": v(282.1, -416.13) * mm});
            skPoint(sketch, "E2.8.16.0", {"position": v(282.1, -441.13) * mm});
            skPoint(sketch, "E2.8.17.0", {"position": v(282.1, -466.13) * mm});
            skPoint(sketch, "E2.8.18.0", {"position": v(282.1, -491.13) * mm});
            skPoint(sketch, "E2.8.19.0", {"position": v(282.1, -516.13) * mm});
            skPoint(sketch, "E2.8.20.0", {"position": v(282.1, -541.13) * mm});
            skPoint(sketch, "E2.8.21.0", {"position": v(282.1, -566.13) * mm});
            skPoint(sketch, "E2.8.22.0", {"position": v(282.1, -591.13) * mm});
            skPoint(sketch, "E2.8.23.0", {"position": v(282.1, -616.13) * mm});
            skPoint(sketch, "E2.8.24.0", {"position": v(282.1, -641.13) * mm});
            skPoint(sketch, "E2.8.25.0", {"position": v(282.1, -666.13) * mm});
            skPoint(sketch, "E2.8.26.0", {"position": v(282.1, -691.13) * mm});
            skPoint(sketch, "E2.8.27.0", {"position": v(282.1, -716.13) * mm});
            skPoint(sketch, "E2.8.28.0", {"position": v(282.1, -741.13) * mm});
            skPoint(sketch, "E2.8.29.0", {"position": v(282.1, -766.13) * mm});
            skPoint(sketch, "E2.8.30.0", {"position": v(282.1, -791.13) * mm});
            skPoint(sketch, "E2.8.31.0", {"position": v(282.1, -816.13) * mm});
            skPoint(sketch, "E2.8.32.0", {"position": v(282.1, -841.13) * mm});
            skPoint(sketch, "E2.8.33.0", {"position": v(282.1, -866.13) * mm});
            skPoint(sketch, "E2.8.34.0", {"position": v(282.1, -891.13) * mm});
            skPoint(sketch, "E2.8.35.0", {"position": v(282.1, -916.13) * mm});
            skPoint(sketch, "E2.8.36.0", {"position": v(282.1, -941.13) * mm});
            skPoint(sketch, "E2.8.37.0", {"position": v(282.1, -966.13) * mm});
            skPoint(sketch, "E2.8.38.0", {"position": v(282.1, -991.13) * mm});
            skPoint(sketch, "E2.8.39.0", {"position": v(282.1, -1016.13) * mm});
            skPoint(sketch, "E2.8.40.0", {"position": v(282.1, -1041.13) * mm});
            skPoint(sketch, "E2.8.41.0", {"position": v(282.1, -1066.13) * mm});
            skPoint(sketch, "E2.8.42.0", {"position": v(282.1, -1091.13) * mm});
            skPoint(sketch, "E2.8.43.0", {"position": v(282.1, -1116.13) * mm});
            skPoint(sketch, "E2.8.44.0", {"position": v(282.1, -1141.13) * mm});
            skPoint(sketch, "E2.8.45.0", {"position": v(282.1, -1166.13) * mm});
            skPoint(sketch, "E2.8.46.0", {"position": v(282.1, -1191.13) * mm});
            skPoint(sketch, "E2.8.47.0", {"position": v(282.1, -1216.13) * mm});
            skPoint(sketch, "E2.8.48.0", {"position": v(282.1, -1241.13) * mm});
            skPoint(sketch, "E2.8.49.0", {"position": v(282.1, -1266.13) * mm});
            skPoint(sketch, "E2.8.50.0", {"position": v(282.1, -1291.13) * mm});
            skPoint(sketch, "E2.8.51.0", {"position": v(282.1, -1316.13) * mm});
            skPoint(sketch, "E2.8.52.0", {"position": v(282.1, -1341.13) * mm});
            skPoint(sketch, "E2.8.53.0", {"position": v(282.1, -1366.13) * mm});
            skPoint(sketch, "E2.8.54.0", {"position": v(282.1, -1391.13) * mm});
            skPoint(sketch, "E2.8.55.0", {"position": v(282.1, -1416.13) * mm});
            skPoint(sketch, "E2.8.56.0", {"position": v(282.1, -1441.13) * mm});
            skPoint(sketch, "E2.8.57.0", {"position": v(282.1, -1466.13) * mm});
            skPoint(sketch, "E2.8.58.0", {"position": v(282.1, -1491.13) * mm});
            skPoint(sketch, "E2.8.59.0", {"position": v(282.1, -1516.13) * mm});
            skPoint(sketch, "E2.8.60.0", {"position": v(282.1, -1541.13) * mm});
            skPoint(sketch, "E2.8.61.0", {"position": v(282.1, -1566.13) * mm});
            skPoint(sketch, "E2.8.62.0", {"position": v(282.1, -1591.13) * mm});
            skPoint(sketch, "E2.8.63.0", {"position": v(282.1, -1616.13) * mm});
            skPoint(sketch, "E2.8.64.0", {"position": v(282.1, -1641.13) * mm});
            skPoint(sketch, "E2.8.65.0", {"position": v(282.1, -1666.13) * mm});
            skPoint(sketch, "E2.8.66.0", {"position": v(282.1, -1691.13) * mm});
            skPoint(sketch, "E2.8.67.0", {"position": v(282.1, -1716.13) * mm});
            skPoint(sketch, "E2.8.68.0", {"position": v(282.1, -1741.13) * mm});
            skPoint(sketch, "E2.9.0.0", {"position": v(312.1, -41.13) * mm});
            skPoint(sketch, "E2.9.1.0", {"position": v(312.1, -66.13) * mm});
            skPoint(sketch, "E2.9.2.0", {"position": v(312.1, -91.13) * mm});
            skPoint(sketch, "E2.9.3.0", {"position": v(312.1, -116.13) * mm});
            skPoint(sketch, "E2.9.4.0", {"position": v(312.1, -141.13) * mm});
            skPoint(sketch, "E2.9.5.0", {"position": v(312.1, -166.13) * mm});
            skPoint(sketch, "E2.9.6.0", {"position": v(312.1, -191.13) * mm});
            skPoint(sketch, "E2.9.7.0", {"position": v(312.1, -216.13) * mm});
            skPoint(sketch, "E2.9.8.0", {"position": v(312.1, -241.13) * mm});
            skPoint(sketch, "E2.9.9.0", {"position": v(312.1, -266.13) * mm});
            skPoint(sketch, "E2.9.10.0", {"position": v(312.1, -291.13) * mm});
            skPoint(sketch, "E2.9.11.0", {"position": v(312.1, -316.13) * mm});
            skPoint(sketch, "E2.9.12.0", {"position": v(312.1, -341.13) * mm});
            skPoint(sketch, "E2.9.13.0", {"position": v(312.1, -366.13) * mm});
            skPoint(sketch, "E2.9.14.0", {"position": v(312.1, -391.13) * mm});
            skPoint(sketch, "E2.9.15.0", {"position": v(312.1, -416.13) * mm});
            skPoint(sketch, "E2.9.16.0", {"position": v(312.1, -441.13) * mm});
            skPoint(sketch, "E2.9.17.0", {"position": v(312.1, -466.13) * mm});
            skPoint(sketch, "E2.9.18.0", {"position": v(312.1, -491.13) * mm});
            skPoint(sketch, "E2.9.19.0", {"position": v(312.1, -516.13) * mm});
            skPoint(sketch, "E2.9.20.0", {"position": v(312.1, -541.13) * mm});
            skPoint(sketch, "E2.9.21.0", {"position": v(312.1, -566.13) * mm});
            skPoint(sketch, "E2.9.22.0", {"position": v(312.1, -591.13) * mm});
            skPoint(sketch, "E2.9.23.0", {"position": v(312.1, -616.13) * mm});
            skPoint(sketch, "E2.9.24.0", {"position": v(312.1, -641.13) * mm});
            skPoint(sketch, "E2.9.25.0", {"position": v(312.1, -666.13) * mm});
            skPoint(sketch, "E2.9.26.0", {"position": v(312.1, -691.13) * mm});
            skPoint(sketch, "E2.9.27.0", {"position": v(312.1, -716.13) * mm});
            skPoint(sketch, "E2.9.28.0", {"position": v(312.1, -741.13) * mm});
            skPoint(sketch, "E2.9.29.0", {"position": v(312.1, -766.13) * mm});
            skPoint(sketch, "E2.9.30.0", {"position": v(312.1, -791.13) * mm});
            skPoint(sketch, "E2.9.31.0", {"position": v(312.1, -816.13) * mm});
            skPoint(sketch, "E2.9.32.0", {"position": v(312.1, -841.13) * mm});
            skPoint(sketch, "E2.9.33.0", {"position": v(312.1, -866.13) * mm});
            skPoint(sketch, "E2.9.34.0", {"position": v(312.1, -891.13) * mm});
            skPoint(sketch, "E2.9.35.0", {"position": v(312.1, -916.13) * mm});
            skPoint(sketch, "E2.9.36.0", {"position": v(312.1, -941.13) * mm});
            skPoint(sketch, "E2.9.37.0", {"position": v(312.1, -966.13) * mm});
            skPoint(sketch, "E2.9.38.0", {"position": v(312.1, -991.13) * mm});
            skPoint(sketch, "E2.9.39.0", {"position": v(312.1, -1016.13) * mm});
            skPoint(sketch, "E2.9.40.0", {"position": v(312.1, -1041.13) * mm});
            skPoint(sketch, "E2.9.41.0", {"position": v(312.1, -1066.13) * mm});
            skPoint(sketch, "E2.9.42.0", {"position": v(312.1, -1091.13) * mm});
            skPoint(sketch, "E2.9.43.0", {"position": v(312.1, -1116.13) * mm});
            skPoint(sketch, "E2.9.44.0", {"position": v(312.1, -1141.13) * mm});
            skPoint(sketch, "E2.9.45.0", {"position": v(312.1, -1166.13) * mm});
            skPoint(sketch, "E2.9.46.0", {"position": v(312.1, -1191.13) * mm});
            skPoint(sketch, "E2.9.47.0", {"position": v(312.1, -1216.13) * mm});
            skPoint(sketch, "E2.9.48.0", {"position": v(312.1, -1241.13) * mm});
            skPoint(sketch, "E2.9.49.0", {"position": v(312.1, -1266.13) * mm});
            skPoint(sketch, "E2.9.50.0", {"position": v(312.1, -1291.13) * mm});
            skPoint(sketch, "E2.9.51.0", {"position": v(312.1, -1316.13) * mm});
            skPoint(sketch, "E2.9.52.0", {"position": v(312.1, -1341.13) * mm});
            skPoint(sketch, "E2.9.53.0", {"position": v(312.1, -1366.13) * mm});
            skPoint(sketch, "E2.9.54.0", {"position": v(312.1, -1391.13) * mm});
            skPoint(sketch, "E2.9.55.0", {"position": v(312.1, -1416.13) * mm});
            skPoint(sketch, "E2.9.56.0", {"position": v(312.1, -1441.13) * mm});
            skPoint(sketch, "E2.9.57.0", {"position": v(312.1, -1466.13) * mm});
            skPoint(sketch, "E2.9.58.0", {"position": v(312.1, -1491.13) * mm});
            skPoint(sketch, "E2.9.59.0", {"position": v(312.1, -1516.13) * mm});
            skPoint(sketch, "E2.9.60.0", {"position": v(312.1, -1541.13) * mm});
            skPoint(sketch, "E2.9.61.0", {"position": v(312.1, -1566.13) * mm});
            skPoint(sketch, "E2.9.62.0", {"position": v(312.1, -1591.13) * mm});
            skPoint(sketch, "E2.9.63.0", {"position": v(312.1, -1616.13) * mm});
            skPoint(sketch, "E2.9.64.0", {"position": v(312.1, -1641.13) * mm});
            skPoint(sketch, "E2.9.65.0", {"position": v(312.1, -1666.13) * mm});
            skPoint(sketch, "E2.9.66.0", {"position": v(312.1, -1691.13) * mm});
            skPoint(sketch, "E2.9.67.0", {"position": v(312.1, -1716.13) * mm});
            skPoint(sketch, "E2.9.68.0", {"position": v(312.1, -1741.13) * mm});
            skPoint(sketch, "E2.10.0.0", {"position": v(342.1, -41.13) * mm});
            skPoint(sketch, "E2.10.1.0", {"position": v(342.1, -66.13) * mm});
            skPoint(sketch, "E2.10.2.0", {"position": v(342.1, -91.13) * mm});
            skPoint(sketch, "E2.10.3.0", {"position": v(342.1, -116.13) * mm});
            skPoint(sketch, "E2.10.4.0", {"position": v(342.1, -141.13) * mm});
            skPoint(sketch, "E2.10.5.0", {"position": v(342.1, -166.13) * mm});
            skPoint(sketch, "E2.10.6.0", {"position": v(342.1, -191.13) * mm});
            skPoint(sketch, "E2.10.7.0", {"position": v(342.1, -216.13) * mm});
            skPoint(sketch, "E2.10.8.0", {"position": v(342.1, -241.13) * mm});
            skPoint(sketch, "E2.10.9.0", {"position": v(342.1, -266.13) * mm});
            skPoint(sketch, "E2.10.10.0", {"position": v(342.1, -291.13) * mm});
            skPoint(sketch, "E2.10.11.0", {"position": v(342.1, -316.13) * mm});
            skPoint(sketch, "E2.10.12.0", {"position": v(342.1, -341.13) * mm});
            skPoint(sketch, "E2.10.13.0", {"position": v(342.1, -366.13) * mm});
            skPoint(sketch, "E2.10.14.0", {"position": v(342.1, -391.13) * mm});
            skPoint(sketch, "E2.10.15.0", {"position": v(342.1, -416.13) * mm});
            skPoint(sketch, "E2.10.16.0", {"position": v(342.1, -441.13) * mm});
            skPoint(sketch, "E2.10.17.0", {"position": v(342.1, -466.13) * mm});
            skPoint(sketch, "E2.10.18.0", {"position": v(342.1, -491.13) * mm});
            skPoint(sketch, "E2.10.19.0", {"position": v(342.1, -516.13) * mm});
            skPoint(sketch, "E2.10.20.0", {"position": v(342.1, -541.13) * mm});
            skPoint(sketch, "E2.10.21.0", {"position": v(342.1, -566.13) * mm});
            skPoint(sketch, "E2.10.22.0", {"position": v(342.1, -591.13) * mm});
            skPoint(sketch, "E2.10.23.0", {"position": v(342.1, -616.13) * mm});
            skPoint(sketch, "E2.10.24.0", {"position": v(342.1, -641.13) * mm});
            skPoint(sketch, "E2.10.25.0", {"position": v(342.1, -666.13) * mm});
            skPoint(sketch, "E2.10.26.0", {"position": v(342.1, -691.13) * mm});
            skPoint(sketch, "E2.10.27.0", {"position": v(342.1, -716.13) * mm});
            skPoint(sketch, "E2.10.28.0", {"position": v(342.1, -741.13) * mm});
            skPoint(sketch, "E2.10.29.0", {"position": v(342.1, -766.13) * mm});
            skPoint(sketch, "E2.10.30.0", {"position": v(342.1, -791.13) * mm});
            skPoint(sketch, "E2.10.31.0", {"position": v(342.1, -816.13) * mm});
            skPoint(sketch, "E2.10.32.0", {"position": v(342.1, -841.13) * mm});
            skPoint(sketch, "E2.10.33.0", {"position": v(342.1, -866.13) * mm});
            skPoint(sketch, "E2.10.34.0", {"position": v(342.1, -891.13) * mm});
            skPoint(sketch, "E2.10.35.0", {"position": v(342.1, -916.13) * mm});
            skPoint(sketch, "E2.10.36.0", {"position": v(342.1, -941.13) * mm});
            skPoint(sketch, "E2.10.37.0", {"position": v(342.1, -966.13) * mm});
            skPoint(sketch, "E2.10.38.0", {"position": v(342.1, -991.13) * mm});
            skPoint(sketch, "E2.10.39.0", {"position": v(342.1, -1016.13) * mm});
            skPoint(sketch, "E2.10.40.0", {"position": v(342.1, -1041.13) * mm});
            skPoint(sketch, "E2.10.41.0", {"position": v(342.1, -1066.13) * mm});
            skPoint(sketch, "E2.10.42.0", {"position": v(342.1, -1091.13) * mm});
            skPoint(sketch, "E2.10.43.0", {"position": v(342.1, -1116.13) * mm});
            skPoint(sketch, "E2.10.44.0", {"position": v(342.1, -1141.13) * mm});
            skPoint(sketch, "E2.10.45.0", {"position": v(342.1, -1166.13) * mm});
            skPoint(sketch, "E2.10.46.0", {"position": v(342.1, -1191.13) * mm});
            skPoint(sketch, "E2.10.47.0", {"position": v(342.1, -1216.13) * mm});
            skPoint(sketch, "E2.10.48.0", {"position": v(342.1, -1241.13) * mm});
            skPoint(sketch, "E2.10.49.0", {"position": v(342.1, -1266.13) * mm});
            skPoint(sketch, "E2.10.50.0", {"position": v(342.1, -1291.13) * mm});
            skPoint(sketch, "E2.10.51.0", {"position": v(342.1, -1316.13) * mm});
            skPoint(sketch, "E2.10.52.0", {"position": v(342.1, -1341.13) * mm});
            skPoint(sketch, "E2.10.53.0", {"position": v(342.1, -1366.13) * mm});
            skPoint(sketch, "E2.10.54.0", {"position": v(342.1, -1391.13) * mm});
            skPoint(sketch, "E2.10.55.0", {"position": v(342.1, -1416.13) * mm});
            skPoint(sketch, "E2.10.56.0", {"position": v(342.1, -1441.13) * mm});
            skPoint(sketch, "E2.10.57.0", {"position": v(342.1, -1466.13) * mm});
            skPoint(sketch, "E2.10.58.0", {"position": v(342.1, -1491.13) * mm});
            skPoint(sketch, "E2.10.59.0", {"position": v(342.1, -1516.13) * mm});
            skPoint(sketch, "E2.10.60.0", {"position": v(342.1, -1541.13) * mm});
            skPoint(sketch, "E2.10.61.0", {"position": v(342.1, -1566.13) * mm});
            skPoint(sketch, "E2.10.62.0", {"position": v(342.1, -1591.13) * mm});
            skPoint(sketch, "E2.10.63.0", {"position": v(342.1, -1616.13) * mm});
            skPoint(sketch, "E2.10.64.0", {"position": v(342.1, -1641.13) * mm});
            skPoint(sketch, "E2.10.65.0", {"position": v(342.1, -1666.13) * mm});
            skPoint(sketch, "E2.10.66.0", {"position": v(342.1, -1691.13) * mm});
            skPoint(sketch, "E2.10.67.0", {"position": v(342.1, -1716.13) * mm});
            skPoint(sketch, "E2.10.68.0", {"position": v(342.1, -1741.13) * mm});
            skPoint(sketch, "E2.11.0.0", {"position": v(372.1, -41.13) * mm});
            skPoint(sketch, "E2.11.1.0", {"position": v(372.1, -66.13) * mm});
            skPoint(sketch, "E2.11.2.0", {"position": v(372.1, -91.13) * mm});
            skPoint(sketch, "E2.11.3.0", {"position": v(372.1, -116.13) * mm});
            skPoint(sketch, "E2.11.4.0", {"position": v(372.1, -141.13) * mm});
            skPoint(sketch, "E2.11.5.0", {"position": v(372.1, -166.13) * mm});
            skPoint(sketch, "E2.11.6.0", {"position": v(372.1, -191.13) * mm});
            skPoint(sketch, "E2.11.7.0", {"position": v(372.1, -216.13) * mm});
            skPoint(sketch, "E2.11.8.0", {"position": v(372.1, -241.13) * mm});
            skPoint(sketch, "E2.11.9.0", {"position": v(372.1, -266.13) * mm});
            skPoint(sketch, "E2.11.10.0", {"position": v(372.1, -291.13) * mm});
            skPoint(sketch, "E2.11.11.0", {"position": v(372.1, -316.13) * mm});
            skPoint(sketch, "E2.11.12.0", {"position": v(372.1, -341.13) * mm});
            skPoint(sketch, "E2.11.13.0", {"position": v(372.1, -366.13) * mm});
            skPoint(sketch, "E2.11.14.0", {"position": v(372.1, -391.13) * mm});
            skPoint(sketch, "E2.11.15.0", {"position": v(372.1, -416.13) * mm});
            skPoint(sketch, "E2.11.16.0", {"position": v(372.1, -441.13) * mm});
            skPoint(sketch, "E2.11.17.0", {"position": v(372.1, -466.13) * mm});
            skPoint(sketch, "E2.11.18.0", {"position": v(372.1, -491.13) * mm});
            skPoint(sketch, "E2.11.19.0", {"position": v(372.1, -516.13) * mm});
            skPoint(sketch, "E2.11.20.0", {"position": v(372.1, -541.13) * mm});
            skPoint(sketch, "E2.11.21.0", {"position": v(372.1, -566.13) * mm});
            skPoint(sketch, "E2.11.22.0", {"position": v(372.1, -591.13) * mm});
            skPoint(sketch, "E2.11.23.0", {"position": v(372.1, -616.13) * mm});
            skPoint(sketch, "E2.11.24.0", {"position": v(372.1, -641.13) * mm});
            skPoint(sketch, "E2.11.25.0", {"position": v(372.1, -666.13) * mm});
            skPoint(sketch, "E2.11.26.0", {"position": v(372.1, -691.13) * mm});
            skPoint(sketch, "E2.11.27.0", {"position": v(372.1, -716.13) * mm});
            skPoint(sketch, "E2.11.28.0", {"position": v(372.1, -741.13) * mm});
            skPoint(sketch, "E2.11.29.0", {"position": v(372.1, -766.13) * mm});
            skPoint(sketch, "E2.11.30.0", {"position": v(372.1, -791.13) * mm});
            skPoint(sketch, "E2.11.31.0", {"position": v(372.1, -816.13) * mm});
            skPoint(sketch, "E2.11.32.0", {"position": v(372.1, -841.13) * mm});
            skPoint(sketch, "E2.11.33.0", {"position": v(372.1, -866.13) * mm});
            skPoint(sketch, "E2.11.34.0", {"position": v(372.1, -891.13) * mm});
            skPoint(sketch, "E2.11.35.0", {"position": v(372.1, -916.13) * mm});
            skPoint(sketch, "E2.11.36.0", {"position": v(372.1, -941.13) * mm});
            skPoint(sketch, "E2.11.37.0", {"position": v(372.1, -966.13) * mm});
            skPoint(sketch, "E2.11.38.0", {"position": v(372.1, -991.13) * mm});
            skPoint(sketch, "E2.11.39.0", {"position": v(372.1, -1016.13) * mm});
            skPoint(sketch, "E2.11.40.0", {"position": v(372.1, -1041.13) * mm});
            skPoint(sketch, "E2.11.41.0", {"position": v(372.1, -1066.13) * mm});
            skPoint(sketch, "E2.11.42.0", {"position": v(372.1, -1091.13) * mm});
            skPoint(sketch, "E2.11.43.0", {"position": v(372.1, -1116.13) * mm});
            skPoint(sketch, "E2.11.44.0", {"position": v(372.1, -1141.13) * mm});
            skPoint(sketch, "E2.11.45.0", {"position": v(372.1, -1166.13) * mm});
            skPoint(sketch, "E2.11.46.0", {"position": v(372.1, -1191.13) * mm});
            skPoint(sketch, "E2.11.47.0", {"position": v(372.1, -1216.13) * mm});
            skPoint(sketch, "E2.11.48.0", {"position": v(372.1, -1241.13) * mm});
            skPoint(sketch, "E2.11.49.0", {"position": v(372.1, -1266.13) * mm});
            skPoint(sketch, "E2.11.50.0", {"position": v(372.1, -1291.13) * mm});
            skPoint(sketch, "E2.11.51.0", {"position": v(372.1, -1316.13) * mm});
            skPoint(sketch, "E2.11.52.0", {"position": v(372.1, -1341.13) * mm});
            skPoint(sketch, "E2.11.53.0", {"position": v(372.1, -1366.13) * mm});
            skPoint(sketch, "E2.11.54.0", {"position": v(372.1, -1391.13) * mm});
            skPoint(sketch, "E2.11.55.0", {"position": v(372.1, -1416.13) * mm});
            skPoint(sketch, "E2.11.56.0", {"position": v(372.1, -1441.13) * mm});
            skPoint(sketch, "E2.11.57.0", {"position": v(372.1, -1466.13) * mm});
            skPoint(sketch, "E2.11.58.0", {"position": v(372.1, -1491.13) * mm});
            skPoint(sketch, "E2.11.59.0", {"position": v(372.1, -1516.13) * mm});
            skPoint(sketch, "E2.11.60.0", {"position": v(372.1, -1541.13) * mm});
            skPoint(sketch, "E2.11.61.0", {"position": v(372.1, -1566.13) * mm});
            skPoint(sketch, "E2.11.62.0", {"position": v(372.1, -1591.13) * mm});
            skPoint(sketch, "E2.11.63.0", {"position": v(372.1, -1616.13) * mm});
            skPoint(sketch, "E2.11.64.0", {"position": v(372.1, -1641.13) * mm});
            skPoint(sketch, "E2.11.65.0", {"position": v(372.1, -1666.13) * mm});
            skPoint(sketch, "E2.11.66.0", {"position": v(372.1, -1691.13) * mm});
            skPoint(sketch, "E2.11.67.0", {"position": v(372.1, -1716.13) * mm});
            skPoint(sketch, "E2.11.68.0", {"position": v(372.1, -1741.13) * mm});
            skPoint(sketch, "E2.12.0.0", {"position": v(402.1, -41.13) * mm});
            skPoint(sketch, "E2.12.1.0", {"position": v(402.1, -66.13) * mm});
            skPoint(sketch, "E2.12.2.0", {"position": v(402.1, -91.13) * mm});
            skPoint(sketch, "E2.12.3.0", {"position": v(402.1, -116.13) * mm});
            skPoint(sketch, "E2.12.4.0", {"position": v(402.1, -141.13) * mm});
            skPoint(sketch, "E2.12.5.0", {"position": v(402.1, -166.13) * mm});
            skPoint(sketch, "E2.12.6.0", {"position": v(402.1, -191.13) * mm});
            skPoint(sketch, "E2.12.7.0", {"position": v(402.1, -216.13) * mm});
            skPoint(sketch, "E2.12.8.0", {"position": v(402.1, -241.13) * mm});
            skPoint(sketch, "E2.12.9.0", {"position": v(402.1, -266.13) * mm});
            skPoint(sketch, "E2.12.10.0", {"position": v(402.1, -291.13) * mm});
            skPoint(sketch, "E2.12.11.0", {"position": v(402.1, -316.13) * mm});
            skPoint(sketch, "E2.12.12.0", {"position": v(402.1, -341.13) * mm});
            skPoint(sketch, "E2.12.13.0", {"position": v(402.1, -366.13) * mm});
            skPoint(sketch, "E2.12.14.0", {"position": v(402.1, -391.13) * mm});
            skPoint(sketch, "E2.12.15.0", {"position": v(402.1, -416.13) * mm});
            skPoint(sketch, "E2.12.16.0", {"position": v(402.1, -441.13) * mm});
            skPoint(sketch, "E2.12.17.0", {"position": v(402.1, -466.13) * mm});
            skPoint(sketch, "E2.12.18.0", {"position": v(402.1, -491.13) * mm});
            skPoint(sketch, "E2.12.19.0", {"position": v(402.1, -516.13) * mm});
            skPoint(sketch, "E2.12.20.0", {"position": v(402.1, -541.13) * mm});
            skPoint(sketch, "E2.12.21.0", {"position": v(402.1, -566.13) * mm});
            skPoint(sketch, "E2.12.22.0", {"position": v(402.1, -591.13) * mm});
            skPoint(sketch, "E2.12.23.0", {"position": v(402.1, -616.13) * mm});
            skPoint(sketch, "E2.12.24.0", {"position": v(402.1, -641.13) * mm});
            skPoint(sketch, "E2.12.25.0", {"position": v(402.1, -666.13) * mm});
            skPoint(sketch, "E2.12.26.0", {"position": v(402.1, -691.13) * mm});
            skPoint(sketch, "E2.12.27.0", {"position": v(402.1, -716.13) * mm});
            skPoint(sketch, "E2.12.28.0", {"position": v(402.1, -741.13) * mm});
            skPoint(sketch, "E2.12.29.0", {"position": v(402.1, -766.13) * mm});
            skPoint(sketch, "E2.12.30.0", {"position": v(402.1, -791.13) * mm});
            skPoint(sketch, "E2.12.31.0", {"position": v(402.1, -816.13) * mm});
            skPoint(sketch, "E2.12.32.0", {"position": v(402.1, -841.13) * mm});
            skPoint(sketch, "E2.12.33.0", {"position": v(402.1, -866.13) * mm});
            skPoint(sketch, "E2.12.34.0", {"position": v(402.1, -891.13) * mm});
            skPoint(sketch, "E2.12.35.0", {"position": v(402.1, -916.13) * mm});
            skPoint(sketch, "E2.12.36.0", {"position": v(402.1, -941.13) * mm});
            skPoint(sketch, "E2.12.37.0", {"position": v(402.1, -966.13) * mm});
            skPoint(sketch, "E2.12.38.0", {"position": v(402.1, -991.13) * mm});
            skPoint(sketch, "E2.12.39.0", {"position": v(402.1, -1016.13) * mm});
            skPoint(sketch, "E2.12.40.0", {"position": v(402.1, -1041.13) * mm});
            skPoint(sketch, "E2.12.41.0", {"position": v(402.1, -1066.13) * mm});
            skPoint(sketch, "E2.12.42.0", {"position": v(402.1, -1091.13) * mm});
            skPoint(sketch, "E2.12.43.0", {"position": v(402.1, -1116.13) * mm});
            skPoint(sketch, "E2.12.44.0", {"position": v(402.1, -1141.13) * mm});
            skPoint(sketch, "E2.12.45.0", {"position": v(402.1, -1166.13) * mm});
            skPoint(sketch, "E2.12.46.0", {"position": v(402.1, -1191.13) * mm});
            skPoint(sketch, "E2.12.47.0", {"position": v(402.1, -1216.13) * mm});
            skPoint(sketch, "E2.12.48.0", {"position": v(402.1, -1241.13) * mm});
            skPoint(sketch, "E2.12.49.0", {"position": v(402.1, -1266.13) * mm});
            skPoint(sketch, "E2.12.50.0", {"position": v(402.1, -1291.13) * mm});
            skPoint(sketch, "E2.12.51.0", {"position": v(402.1, -1316.13) * mm});
            skPoint(sketch, "E2.12.52.0", {"position": v(402.1, -1341.13) * mm});
            skPoint(sketch, "E2.12.53.0", {"position": v(402.1, -1366.13) * mm});
            skPoint(sketch, "E2.12.54.0", {"position": v(402.1, -1391.13) * mm});
            skPoint(sketch, "E2.12.55.0", {"position": v(402.1, -1416.13) * mm});
            skPoint(sketch, "E2.12.56.0", {"position": v(402.1, -1441.13) * mm});
            skPoint(sketch, "E2.12.57.0", {"position": v(402.1, -1466.13) * mm});
            skPoint(sketch, "E2.12.58.0", {"position": v(402.1, -1491.13) * mm});
            skPoint(sketch, "E2.12.59.0", {"position": v(402.1, -1516.13) * mm});
            skPoint(sketch, "E2.12.60.0", {"position": v(402.1, -1541.13) * mm});
            skPoint(sketch, "E2.12.61.0", {"position": v(402.1, -1566.13) * mm});
            skPoint(sketch, "E2.12.62.0", {"position": v(402.1, -1591.13) * mm});
            skPoint(sketch, "E2.12.63.0", {"position": v(402.1, -1616.13) * mm});
            skPoint(sketch, "E2.12.64.0", {"position": v(402.1, -1641.13) * mm});
            skPoint(sketch, "E2.12.65.0", {"position": v(402.1, -1666.13) * mm});
            skPoint(sketch, "E2.12.66.0", {"position": v(402.1, -1691.13) * mm});
            skPoint(sketch, "E2.12.67.0", {"position": v(402.1, -1716.13) * mm});
            skPoint(sketch, "E2.12.68.0", {"position": v(402.1, -1741.13) * mm});
            skPoint(sketch, "E2.13.0.0", {"position": v(432.1, -41.13) * mm});
            skPoint(sketch, "E2.13.1.0", {"position": v(432.1, -66.13) * mm});
            skPoint(sketch, "E2.13.2.0", {"position": v(432.1, -91.13) * mm});
            skPoint(sketch, "E2.13.3.0", {"position": v(432.1, -116.13) * mm});
            skPoint(sketch, "E2.13.4.0", {"position": v(432.1, -141.13) * mm});
            skPoint(sketch, "E2.13.5.0", {"position": v(432.1, -166.13) * mm});
            skPoint(sketch, "E2.13.6.0", {"position": v(432.1, -191.13) * mm});
            skPoint(sketch, "E2.13.7.0", {"position": v(432.1, -216.13) * mm});
            skPoint(sketch, "E2.13.8.0", {"position": v(432.1, -241.13) * mm});
            skPoint(sketch, "E2.13.9.0", {"position": v(432.1, -266.13) * mm});
            skPoint(sketch, "E2.13.10.0", {"position": v(432.1, -291.13) * mm});
            skPoint(sketch, "E2.13.11.0", {"position": v(432.1, -316.13) * mm});
            skPoint(sketch, "E2.13.12.0", {"position": v(432.1, -341.13) * mm});
            skPoint(sketch, "E2.13.13.0", {"position": v(432.1, -366.13) * mm});
            skPoint(sketch, "E2.13.14.0", {"position": v(432.1, -391.13) * mm});
            skPoint(sketch, "E2.13.15.0", {"position": v(432.1, -416.13) * mm});
            skPoint(sketch, "E2.13.16.0", {"position": v(432.1, -441.13) * mm});
            skPoint(sketch, "E2.13.17.0", {"position": v(432.1, -466.13) * mm});
            skPoint(sketch, "E2.13.18.0", {"position": v(432.1, -491.13) * mm});
            skPoint(sketch, "E2.13.19.0", {"position": v(432.1, -516.13) * mm});
            skPoint(sketch, "E2.13.20.0", {"position": v(432.1, -541.13) * mm});
            skPoint(sketch, "E2.13.21.0", {"position": v(432.1, -566.13) * mm});
            skPoint(sketch, "E2.13.22.0", {"position": v(432.1, -591.13) * mm});
            skPoint(sketch, "E2.13.23.0", {"position": v(432.1, -616.13) * mm});
            skPoint(sketch, "E2.13.24.0", {"position": v(432.1, -641.13) * mm});
            skPoint(sketch, "E2.13.25.0", {"position": v(432.1, -666.13) * mm});
            skPoint(sketch, "E2.13.26.0", {"position": v(432.1, -691.13) * mm});
            skPoint(sketch, "E2.13.27.0", {"position": v(432.1, -716.13) * mm});
            skPoint(sketch, "E2.13.28.0", {"position": v(432.1, -741.13) * mm});
            skPoint(sketch, "E2.13.29.0", {"position": v(432.1, -766.13) * mm});
            skPoint(sketch, "E2.13.30.0", {"position": v(432.1, -791.13) * mm});
            skPoint(sketch, "E2.13.31.0", {"position": v(432.1, -816.13) * mm});
            skPoint(sketch, "E2.13.32.0", {"position": v(432.1, -841.13) * mm});
            skPoint(sketch, "E2.13.33.0", {"position": v(432.1, -866.13) * mm});
            skPoint(sketch, "E2.13.34.0", {"position": v(432.1, -891.13) * mm});
            skPoint(sketch, "E2.13.35.0", {"position": v(432.1, -916.13) * mm});
            skPoint(sketch, "E2.13.36.0", {"position": v(432.1, -941.13) * mm});
            skPoint(sketch, "E2.13.37.0", {"position": v(432.1, -966.13) * mm});
            skPoint(sketch, "E2.13.38.0", {"position": v(432.1, -991.13) * mm});
            skPoint(sketch, "E2.13.39.0", {"position": v(432.1, -1016.13) * mm});
            skPoint(sketch, "E2.13.40.0", {"position": v(432.1, -1041.13) * mm});
            skPoint(sketch, "E2.13.41.0", {"position": v(432.1, -1066.13) * mm});
            skPoint(sketch, "E2.13.42.0", {"position": v(432.1, -1091.13) * mm});
            skPoint(sketch, "E2.13.43.0", {"position": v(432.1, -1116.13) * mm});
            skPoint(sketch, "E2.13.44.0", {"position": v(432.1, -1141.13) * mm});
            skPoint(sketch, "E2.13.45.0", {"position": v(432.1, -1166.13) * mm});
            skPoint(sketch, "E2.13.46.0", {"position": v(432.1, -1191.13) * mm});
            skPoint(sketch, "E2.13.47.0", {"position": v(432.1, -1216.13) * mm});
            skPoint(sketch, "E2.13.48.0", {"position": v(432.1, -1241.13) * mm});
            skPoint(sketch, "E2.13.49.0", {"position": v(432.1, -1266.13) * mm});
            skPoint(sketch, "E2.13.50.0", {"position": v(432.1, -1291.13) * mm});
            skPoint(sketch, "E2.13.51.0", {"position": v(432.1, -1316.13) * mm});
            skPoint(sketch, "E2.13.52.0", {"position": v(432.1, -1341.13) * mm});
            skPoint(sketch, "E2.13.53.0", {"position": v(432.1, -1366.13) * mm});
            skPoint(sketch, "E2.13.54.0", {"position": v(432.1, -1391.13) * mm});
            skPoint(sketch, "E2.13.55.0", {"position": v(432.1, -1416.13) * mm});
            skPoint(sketch, "E2.13.56.0", {"position": v(432.1, -1441.13) * mm});
            skPoint(sketch, "E2.13.57.0", {"position": v(432.1, -1466.13) * mm});
            skPoint(sketch, "E2.13.58.0", {"position": v(432.1, -1491.13) * mm});
            skPoint(sketch, "E2.13.59.0", {"position": v(432.1, -1516.13) * mm});
            skPoint(sketch, "E2.13.60.0", {"position": v(432.1, -1541.13) * mm});
            skPoint(sketch, "E2.13.61.0", {"position": v(432.1, -1566.13) * mm});
            skPoint(sketch, "E2.13.62.0", {"position": v(432.1, -1591.13) * mm});
            skPoint(sketch, "E2.13.63.0", {"position": v(432.1, -1616.13) * mm});
            skPoint(sketch, "E2.13.64.0", {"position": v(432.1, -1641.13) * mm});
            skPoint(sketch, "E2.13.65.0", {"position": v(432.1, -1666.13) * mm});
            skPoint(sketch, "E2.13.66.0", {"position": v(432.1, -1691.13) * mm});
            skPoint(sketch, "E2.13.67.0", {"position": v(432.1, -1716.13) * mm});
            skPoint(sketch, "E2.13.68.0", {"position": v(432.1, -1741.13) * mm});
            skPoint(sketch, "E2.14.0.0", {"position": v(462.1, -41.13) * mm});
            skPoint(sketch, "E2.14.1.0", {"position": v(462.1, -66.13) * mm});
            skPoint(sketch, "E2.14.2.0", {"position": v(462.1, -91.13) * mm});
            skPoint(sketch, "E2.14.3.0", {"position": v(462.1, -116.13) * mm});
            skPoint(sketch, "E2.14.4.0", {"position": v(462.1, -141.13) * mm});
            skPoint(sketch, "E2.14.5.0", {"position": v(462.1, -166.13) * mm});
            skPoint(sketch, "E2.14.6.0", {"position": v(462.1, -191.13) * mm});
            skPoint(sketch, "E2.14.7.0", {"position": v(462.1, -216.13) * mm});
            skPoint(sketch, "E2.14.8.0", {"position": v(462.1, -241.13) * mm});
            skPoint(sketch, "E2.14.9.0", {"position": v(462.1, -266.13) * mm});
            skPoint(sketch, "E2.14.10.0", {"position": v(462.1, -291.13) * mm});
            skPoint(sketch, "E2.14.11.0", {"position": v(462.1, -316.13) * mm});
            skPoint(sketch, "E2.14.12.0", {"position": v(462.1, -341.13) * mm});
            skPoint(sketch, "E2.14.13.0", {"position": v(462.1, -366.13) * mm});
            skPoint(sketch, "E2.14.14.0", {"position": v(462.1, -391.13) * mm});
            skPoint(sketch, "E2.14.15.0", {"position": v(462.1, -416.13) * mm});
            skPoint(sketch, "E2.14.16.0", {"position": v(462.1, -441.13) * mm});
            skPoint(sketch, "E2.14.17.0", {"position": v(462.1, -466.13) * mm});
            skPoint(sketch, "E2.14.18.0", {"position": v(462.1, -491.13) * mm});
            skPoint(sketch, "E2.14.19.0", {"position": v(462.1, -516.13) * mm});
            skPoint(sketch, "E2.14.20.0", {"position": v(462.1, -541.13) * mm});
            skPoint(sketch, "E2.14.21.0", {"position": v(462.1, -566.13) * mm});
            skPoint(sketch, "E2.14.22.0", {"position": v(462.1, -591.13) * mm});
            skPoint(sketch, "E2.14.23.0", {"position": v(462.1, -616.13) * mm});
            skPoint(sketch, "E2.14.24.0", {"position": v(462.1, -641.13) * mm});
            skPoint(sketch, "E2.14.25.0", {"position": v(462.1, -666.13) * mm});
            skPoint(sketch, "E2.14.26.0", {"position": v(462.1, -691.13) * mm});
            skPoint(sketch, "E2.14.27.0", {"position": v(462.1, -716.13) * mm});
            skPoint(sketch, "E2.14.28.0", {"position": v(462.1, -741.13) * mm});
            skPoint(sketch, "E2.14.29.0", {"position": v(462.1, -766.13) * mm});
            skPoint(sketch, "E2.14.30.0", {"position": v(462.1, -791.13) * mm});
            skPoint(sketch, "E2.14.31.0", {"position": v(462.1, -816.13) * mm});
            skPoint(sketch, "E2.14.32.0", {"position": v(462.1, -841.13) * mm});
            skPoint(sketch, "E2.14.33.0", {"position": v(462.1, -866.13) * mm});
            skPoint(sketch, "E2.14.34.0", {"position": v(462.1, -891.13) * mm});
            skPoint(sketch, "E2.14.35.0", {"position": v(462.1, -916.13) * mm});
            skPoint(sketch, "E2.14.36.0", {"position": v(462.1, -941.13) * mm});
            skPoint(sketch, "E2.14.37.0", {"position": v(462.1, -966.13) * mm});
            skPoint(sketch, "E2.14.38.0", {"position": v(462.1, -991.13) * mm});
            skPoint(sketch, "E2.14.39.0", {"position": v(462.1, -1016.13) * mm});
            skPoint(sketch, "E2.14.40.0", {"position": v(462.1, -1041.13) * mm});
            skPoint(sketch, "E2.14.41.0", {"position": v(462.1, -1066.13) * mm});
            skPoint(sketch, "E2.14.42.0", {"position": v(462.1, -1091.13) * mm});
            skPoint(sketch, "E2.14.43.0", {"position": v(462.1, -1116.13) * mm});
            skPoint(sketch, "E2.14.44.0", {"position": v(462.1, -1141.13) * mm});
            skPoint(sketch, "E2.14.45.0", {"position": v(462.1, -1166.13) * mm});
            skPoint(sketch, "E2.14.46.0", {"position": v(462.1, -1191.13) * mm});
            skPoint(sketch, "E2.14.47.0", {"position": v(462.1, -1216.13) * mm});
            skPoint(sketch, "E2.14.48.0", {"position": v(462.1, -1241.13) * mm});
            skPoint(sketch, "E2.14.49.0", {"position": v(462.1, -1266.13) * mm});
            skPoint(sketch, "E2.14.50.0", {"position": v(462.1, -1291.13) * mm});
            skPoint(sketch, "E2.14.51.0", {"position": v(462.1, -1316.13) * mm});
            skPoint(sketch, "E2.14.52.0", {"position": v(462.1, -1341.13) * mm});
            skPoint(sketch, "E2.14.53.0", {"position": v(462.1, -1366.13) * mm});
            skPoint(sketch, "E2.14.54.0", {"position": v(462.1, -1391.13) * mm});
            skPoint(sketch, "E2.14.55.0", {"position": v(462.1, -1416.13) * mm});
            skPoint(sketch, "E2.14.56.0", {"position": v(462.1, -1441.13) * mm});
            skPoint(sketch, "E2.14.57.0", {"position": v(462.1, -1466.13) * mm});
            skPoint(sketch, "E2.14.58.0", {"position": v(462.1, -1491.13) * mm});
            skPoint(sketch, "E2.14.59.0", {"position": v(462.1, -1516.13) * mm});
            skPoint(sketch, "E2.14.60.0", {"position": v(462.1, -1541.13) * mm});
            skPoint(sketch, "E2.14.61.0", {"position": v(462.1, -1566.13) * mm});
            skPoint(sketch, "E2.14.62.0", {"position": v(462.1, -1591.13) * mm});
            skPoint(sketch, "E2.14.63.0", {"position": v(462.1, -1616.13) * mm});
            skPoint(sketch, "E2.14.64.0", {"position": v(462.1, -1641.13) * mm});
            skPoint(sketch, "E2.14.65.0", {"position": v(462.1, -1666.13) * mm});
            skPoint(sketch, "E2.14.66.0", {"position": v(462.1, -1691.13) * mm});
            skPoint(sketch, "E2.14.67.0", {"position": v(462.1, -1716.13) * mm});
            skPoint(sketch, "E2.14.68.0", {"position": v(462.1, -1741.13) * mm});
            skPoint(sketch, "E2.15.0.0", {"position": v(492.1, -41.13) * mm});
            skPoint(sketch, "E2.15.1.0", {"position": v(492.1, -66.13) * mm});
            skPoint(sketch, "E2.15.2.0", {"position": v(492.1, -91.13) * mm});
            skPoint(sketch, "E2.15.3.0", {"position": v(492.1, -116.13) * mm});
            skPoint(sketch, "E2.15.4.0", {"position": v(492.1, -141.13) * mm});
            skPoint(sketch, "E2.15.5.0", {"position": v(492.1, -166.13) * mm});
            skPoint(sketch, "E2.15.6.0", {"position": v(492.1, -191.13) * mm});
            skPoint(sketch, "E2.15.7.0", {"position": v(492.1, -216.13) * mm});
            skPoint(sketch, "E2.15.8.0", {"position": v(492.1, -241.13) * mm});
            skPoint(sketch, "E2.15.9.0", {"position": v(492.1, -266.13) * mm});
            skPoint(sketch, "E2.15.10.0", {"position": v(492.1, -291.13) * mm});
            skPoint(sketch, "E2.15.11.0", {"position": v(492.1, -316.13) * mm});
            skPoint(sketch, "E2.15.12.0", {"position": v(492.1, -341.13) * mm});
            skPoint(sketch, "E2.15.13.0", {"position": v(492.1, -366.13) * mm});
            skPoint(sketch, "E2.15.14.0", {"position": v(492.1, -391.13) * mm});
            skPoint(sketch, "E2.15.15.0", {"position": v(492.1, -416.13) * mm});
            skPoint(sketch, "E2.15.16.0", {"position": v(492.1, -441.13) * mm});
            skPoint(sketch, "E2.15.17.0", {"position": v(492.1, -466.13) * mm});
            skPoint(sketch, "E2.15.18.0", {"position": v(492.1, -491.13) * mm});
            skPoint(sketch, "E2.15.19.0", {"position": v(492.1, -516.13) * mm});
            skPoint(sketch, "E2.15.20.0", {"position": v(492.1, -541.13) * mm});
            skPoint(sketch, "E2.15.21.0", {"position": v(492.1, -566.13) * mm});
            skPoint(sketch, "E2.15.22.0", {"position": v(492.1, -591.13) * mm});
            skPoint(sketch, "E2.15.23.0", {"position": v(492.1, -616.13) * mm});
            skPoint(sketch, "E2.15.24.0", {"position": v(492.1, -641.13) * mm});
            skPoint(sketch, "E2.15.25.0", {"position": v(492.1, -666.13) * mm});
            skPoint(sketch, "E2.15.26.0", {"position": v(492.1, -691.13) * mm});
            skPoint(sketch, "E2.15.27.0", {"position": v(492.1, -716.13) * mm});
            skPoint(sketch, "E2.15.28.0", {"position": v(492.1, -741.13) * mm});
            skPoint(sketch, "E2.15.29.0", {"position": v(492.1, -766.13) * mm});
            skPoint(sketch, "E2.15.30.0", {"position": v(492.1, -791.13) * mm});
            skPoint(sketch, "E2.15.31.0", {"position": v(492.1, -816.13) * mm});
            skPoint(sketch, "E2.15.32.0", {"position": v(492.1, -841.13) * mm});
            skPoint(sketch, "E2.15.33.0", {"position": v(492.1, -866.13) * mm});
            skPoint(sketch, "E2.15.34.0", {"position": v(492.1, -891.13) * mm});
            skPoint(sketch, "E2.15.35.0", {"position": v(492.1, -916.13) * mm});
            skPoint(sketch, "E2.15.36.0", {"position": v(492.1, -941.13) * mm});
            skPoint(sketch, "E2.15.37.0", {"position": v(492.1, -966.13) * mm});
            skPoint(sketch, "E2.15.38.0", {"position": v(492.1, -991.13) * mm});
            skPoint(sketch, "E2.15.39.0", {"position": v(492.1, -1016.13) * mm});
            skPoint(sketch, "E2.15.40.0", {"position": v(492.1, -1041.13) * mm});
            skPoint(sketch, "E2.15.41.0", {"position": v(492.1, -1066.13) * mm});
            skPoint(sketch, "E2.15.42.0", {"position": v(492.1, -1091.13) * mm});
            skPoint(sketch, "E2.15.43.0", {"position": v(492.1, -1116.13) * mm});
            skPoint(sketch, "E2.15.44.0", {"position": v(492.1, -1141.13) * mm});
            skPoint(sketch, "E2.15.45.0", {"position": v(492.1, -1166.13) * mm});
            skPoint(sketch, "E2.15.46.0", {"position": v(492.1, -1191.13) * mm});
            skPoint(sketch, "E2.15.47.0", {"position": v(492.1, -1216.13) * mm});
            skPoint(sketch, "E2.15.48.0", {"position": v(492.1, -1241.13) * mm});
            skPoint(sketch, "E2.15.49.0", {"position": v(492.1, -1266.13) * mm});
            skPoint(sketch, "E2.15.50.0", {"position": v(492.1, -1291.13) * mm});
            skPoint(sketch, "E2.15.51.0", {"position": v(492.1, -1316.13) * mm});
            skPoint(sketch, "E2.15.52.0", {"position": v(492.1, -1341.13) * mm});
            skPoint(sketch, "E2.15.53.0", {"position": v(492.1, -1366.13) * mm});
            skPoint(sketch, "E2.15.54.0", {"position": v(492.1, -1391.13) * mm});
            skPoint(sketch, "E2.15.55.0", {"position": v(492.1, -1416.13) * mm});
            skPoint(sketch, "E2.15.56.0", {"position": v(492.1, -1441.13) * mm});
            skPoint(sketch, "E2.15.57.0", {"position": v(492.1, -1466.13) * mm});
            skPoint(sketch, "E2.15.58.0", {"position": v(492.1, -1491.13) * mm});
            skPoint(sketch, "E2.15.59.0", {"position": v(492.1, -1516.13) * mm});
            skPoint(sketch, "E2.15.60.0", {"position": v(492.1, -1541.13) * mm});
            skPoint(sketch, "E2.15.61.0", {"position": v(492.1, -1566.13) * mm});
            skPoint(sketch, "E2.15.62.0", {"position": v(492.1, -1591.13) * mm});
            skPoint(sketch, "E2.15.63.0", {"position": v(492.1, -1616.13) * mm});
            skPoint(sketch, "E2.15.64.0", {"position": v(492.1, -1641.13) * mm});
            skPoint(sketch, "E2.15.65.0", {"position": v(492.1, -1666.13) * mm});
            skPoint(sketch, "E2.15.66.0", {"position": v(492.1, -1691.13) * mm});
            skPoint(sketch, "E2.15.67.0", {"position": v(492.1, -1716.13) * mm});
            skPoint(sketch, "E2.15.68.0", {"position": v(492.1, -1741.13) * mm});
            skPoint(sketch, "E2.16.0.0", {"position": v(522.1, -41.13) * mm});
            skPoint(sketch, "E2.16.1.0", {"position": v(522.1, -66.13) * mm});
            skPoint(sketch, "E2.16.2.0", {"position": v(522.1, -91.13) * mm});
            skPoint(sketch, "E2.16.3.0", {"position": v(522.1, -116.13) * mm});
            skPoint(sketch, "E2.16.4.0", {"position": v(522.1, -141.13) * mm});
            skPoint(sketch, "E2.16.5.0", {"position": v(522.1, -166.13) * mm});
            skPoint(sketch, "E2.16.6.0", {"position": v(522.1, -191.13) * mm});
            skPoint(sketch, "E2.16.7.0", {"position": v(522.1, -216.13) * mm});
            skPoint(sketch, "E2.16.8.0", {"position": v(522.1, -241.13) * mm});
            skPoint(sketch, "E2.16.9.0", {"position": v(522.1, -266.13) * mm});
            skPoint(sketch, "E2.16.10.0", {"position": v(522.1, -291.13) * mm});
            skPoint(sketch, "E2.16.11.0", {"position": v(522.1, -316.13) * mm});
            skPoint(sketch, "E2.16.12.0", {"position": v(522.1, -341.13) * mm});
            skPoint(sketch, "E2.16.13.0", {"position": v(522.1, -366.13) * mm});
            skPoint(sketch, "E2.16.14.0", {"position": v(522.1, -391.13) * mm});
            skPoint(sketch, "E2.16.15.0", {"position": v(522.1, -416.13) * mm});
            skPoint(sketch, "E2.16.16.0", {"position": v(522.1, -441.13) * mm});
            skPoint(sketch, "E2.16.17.0", {"position": v(522.1, -466.13) * mm});
            skPoint(sketch, "E2.16.18.0", {"position": v(522.1, -491.13) * mm});
            skPoint(sketch, "E2.16.19.0", {"position": v(522.1, -516.13) * mm});
            skPoint(sketch, "E2.16.20.0", {"position": v(522.1, -541.13) * mm});
            skPoint(sketch, "E2.16.21.0", {"position": v(522.1, -566.13) * mm});
            skPoint(sketch, "E2.16.22.0", {"position": v(522.1, -591.13) * mm});
            skPoint(sketch, "E2.16.23.0", {"position": v(522.1, -616.13) * mm});
            skPoint(sketch, "E2.16.24.0", {"position": v(522.1, -641.13) * mm});
            skPoint(sketch, "E2.16.25.0", {"position": v(522.1, -666.13) * mm});
            skPoint(sketch, "E2.16.26.0", {"position": v(522.1, -691.13) * mm});
            skPoint(sketch, "E2.16.27.0", {"position": v(522.1, -716.13) * mm});
            skPoint(sketch, "E2.16.28.0", {"position": v(522.1, -741.13) * mm});
            skPoint(sketch, "E2.16.29.0", {"position": v(522.1, -766.13) * mm});
            skPoint(sketch, "E2.16.30.0", {"position": v(522.1, -791.13) * mm});
            skPoint(sketch, "E2.16.31.0", {"position": v(522.1, -816.13) * mm});
            skPoint(sketch, "E2.16.32.0", {"position": v(522.1, -841.13) * mm});
            skPoint(sketch, "E2.16.33.0", {"position": v(522.1, -866.13) * mm});
            skPoint(sketch, "E2.16.34.0", {"position": v(522.1, -891.13) * mm});
            skPoint(sketch, "E2.16.35.0", {"position": v(522.1, -916.13) * mm});
            skPoint(sketch, "E2.16.36.0", {"position": v(522.1, -941.13) * mm});
            skPoint(sketch, "E2.16.37.0", {"position": v(522.1, -966.13) * mm});
            skPoint(sketch, "E2.16.38.0", {"position": v(522.1, -991.13) * mm});
            skPoint(sketch, "E2.16.39.0", {"position": v(522.1, -1016.13) * mm});
            skPoint(sketch, "E2.16.40.0", {"position": v(522.1, -1041.13) * mm});
            skPoint(sketch, "E2.16.41.0", {"position": v(522.1, -1066.13) * mm});
            skPoint(sketch, "E2.16.42.0", {"position": v(522.1, -1091.13) * mm});
            skPoint(sketch, "E2.16.43.0", {"position": v(522.1, -1116.13) * mm});
            skPoint(sketch, "E2.16.44.0", {"position": v(522.1, -1141.13) * mm});
            skPoint(sketch, "E2.16.45.0", {"position": v(522.1, -1166.13) * mm});
            skPoint(sketch, "E2.16.46.0", {"position": v(522.1, -1191.13) * mm});
            skPoint(sketch, "E2.16.47.0", {"position": v(522.1, -1216.13) * mm});
            skPoint(sketch, "E2.16.48.0", {"position": v(522.1, -1241.13) * mm});
            skPoint(sketch, "E2.16.49.0", {"position": v(522.1, -1266.13) * mm});
            skPoint(sketch, "E2.16.50.0", {"position": v(522.1, -1291.13) * mm});
            skPoint(sketch, "E2.16.51.0", {"position": v(522.1, -1316.13) * mm});
            skPoint(sketch, "E2.16.52.0", {"position": v(522.1, -1341.13) * mm});
            skPoint(sketch, "E2.16.53.0", {"position": v(522.1, -1366.13) * mm});
            skPoint(sketch, "E2.16.54.0", {"position": v(522.1, -1391.13) * mm});
            skPoint(sketch, "E2.16.55.0", {"position": v(522.1, -1416.13) * mm});
            skPoint(sketch, "E2.16.56.0", {"position": v(522.1, -1441.13) * mm});
            skPoint(sketch, "E2.16.57.0", {"position": v(522.1, -1466.13) * mm});
            skPoint(sketch, "E2.16.58.0", {"position": v(522.1, -1491.13) * mm});
            skPoint(sketch, "E2.16.59.0", {"position": v(522.1, -1516.13) * mm});
            skPoint(sketch, "E2.16.60.0", {"position": v(522.1, -1541.13) * mm});
            skPoint(sketch, "E2.16.61.0", {"position": v(522.1, -1566.13) * mm});
            skPoint(sketch, "E2.16.62.0", {"position": v(522.1, -1591.13) * mm});
            skPoint(sketch, "E2.16.63.0", {"position": v(522.1, -1616.13) * mm});
            skPoint(sketch, "E2.16.64.0", {"position": v(522.1, -1641.13) * mm});
            skPoint(sketch, "E2.16.65.0", {"position": v(522.1, -1666.13) * mm});
            skPoint(sketch, "E2.16.66.0", {"position": v(522.1, -1691.13) * mm});
            skPoint(sketch, "E2.16.67.0", {"position": v(522.1, -1716.13) * mm});
            skPoint(sketch, "E2.16.68.0", {"position": v(522.1, -1741.13) * mm});
            skPoint(sketch, "E2.17.0.0", {"position": v(552.1, -41.13) * mm});
            skPoint(sketch, "E2.17.1.0", {"position": v(552.1, -66.13) * mm});
            skPoint(sketch, "E2.17.2.0", {"position": v(552.1, -91.13) * mm});
            skPoint(sketch, "E2.17.3.0", {"position": v(552.1, -116.13) * mm});
            skPoint(sketch, "E2.17.4.0", {"position": v(552.1, -141.13) * mm});
            skPoint(sketch, "E2.17.5.0", {"position": v(552.1, -166.13) * mm});
            skPoint(sketch, "E2.17.6.0", {"position": v(552.1, -191.13) * mm});
            skPoint(sketch, "E2.17.7.0", {"position": v(552.1, -216.13) * mm});
            skPoint(sketch, "E2.17.8.0", {"position": v(552.1, -241.13) * mm});
            skPoint(sketch, "E2.17.9.0", {"position": v(552.1, -266.13) * mm});
            skPoint(sketch, "E2.17.10.0", {"position": v(552.1, -291.13) * mm});
            skPoint(sketch, "E2.17.11.0", {"position": v(552.1, -316.13) * mm});
            skPoint(sketch, "E2.17.12.0", {"position": v(552.1, -341.13) * mm});
            skPoint(sketch, "E2.17.13.0", {"position": v(552.1, -366.13) * mm});
            skPoint(sketch, "E2.17.14.0", {"position": v(552.1, -391.13) * mm});
            skPoint(sketch, "E2.17.15.0", {"position": v(552.1, -416.13) * mm});
            skPoint(sketch, "E2.17.16.0", {"position": v(552.1, -441.13) * mm});
            skPoint(sketch, "E2.17.17.0", {"position": v(552.1, -466.13) * mm});
            skPoint(sketch, "E2.17.18.0", {"position": v(552.1, -491.13) * mm});
            skPoint(sketch, "E2.17.19.0", {"position": v(552.1, -516.13) * mm});
            skPoint(sketch, "E2.17.20.0", {"position": v(552.1, -541.13) * mm});
            skPoint(sketch, "E2.17.21.0", {"position": v(552.1, -566.13) * mm});
            skPoint(sketch, "E2.17.22.0", {"position": v(552.1, -591.13) * mm});
            skPoint(sketch, "E2.17.23.0", {"position": v(552.1, -616.13) * mm});
            skPoint(sketch, "E2.17.24.0", {"position": v(552.1, -641.13) * mm});
            skPoint(sketch, "E2.17.25.0", {"position": v(552.1, -666.13) * mm});
            skPoint(sketch, "E2.17.26.0", {"position": v(552.1, -691.13) * mm});
            skPoint(sketch, "E2.17.27.0", {"position": v(552.1, -716.13) * mm});
            skPoint(sketch, "E2.17.28.0", {"position": v(552.1, -741.13) * mm});
            skPoint(sketch, "E2.17.29.0", {"position": v(552.1, -766.13) * mm});
            skPoint(sketch, "E2.17.30.0", {"position": v(552.1, -791.13) * mm});
            skPoint(sketch, "E2.17.31.0", {"position": v(552.1, -816.13) * mm});
            skPoint(sketch, "E2.17.32.0", {"position": v(552.1, -841.13) * mm});
            skPoint(sketch, "E2.17.33.0", {"position": v(552.1, -866.13) * mm});
            skPoint(sketch, "E2.17.34.0", {"position": v(552.1, -891.13) * mm});
            skPoint(sketch, "E2.17.35.0", {"position": v(552.1, -916.13) * mm});
            skPoint(sketch, "E2.17.36.0", {"position": v(552.1, -941.13) * mm});
            skPoint(sketch, "E2.17.37.0", {"position": v(552.1, -966.13) * mm});
            skPoint(sketch, "E2.17.38.0", {"position": v(552.1, -991.13) * mm});
            skPoint(sketch, "E2.17.39.0", {"position": v(552.1, -1016.13) * mm});
            skPoint(sketch, "E2.17.40.0", {"position": v(552.1, -1041.13) * mm});
            skPoint(sketch, "E2.17.41.0", {"position": v(552.1, -1066.13) * mm});
            skPoint(sketch, "E2.17.42.0", {"position": v(552.1, -1091.13) * mm});
            skPoint(sketch, "E2.17.43.0", {"position": v(552.1, -1116.13) * mm});
            skPoint(sketch, "E2.17.44.0", {"position": v(552.1, -1141.13) * mm});
            skPoint(sketch, "E2.17.45.0", {"position": v(552.1, -1166.13) * mm});
            skPoint(sketch, "E2.17.46.0", {"position": v(552.1, -1191.13) * mm});
            skPoint(sketch, "E2.17.47.0", {"position": v(552.1, -1216.13) * mm});
            skPoint(sketch, "E2.17.48.0", {"position": v(552.1, -1241.13) * mm});
            skPoint(sketch, "E2.17.49.0", {"position": v(552.1, -1266.13) * mm});
            skPoint(sketch, "E2.17.50.0", {"position": v(552.1, -1291.13) * mm});
            skPoint(sketch, "E2.17.51.0", {"position": v(552.1, -1316.13) * mm});
            skPoint(sketch, "E2.17.52.0", {"position": v(552.1, -1341.13) * mm});
            skPoint(sketch, "E2.17.53.0", {"position": v(552.1, -1366.13) * mm});
            skPoint(sketch, "E2.17.54.0", {"position": v(552.1, -1391.13) * mm});
            skPoint(sketch, "E2.17.55.0", {"position": v(552.1, -1416.13) * mm});
            skPoint(sketch, "E2.17.56.0", {"position": v(552.1, -1441.13) * mm});
            skPoint(sketch, "E2.17.57.0", {"position": v(552.1, -1466.13) * mm});
            skPoint(sketch, "E2.17.58.0", {"position": v(552.1, -1491.13) * mm});
            skPoint(sketch, "E2.17.59.0", {"position": v(552.1, -1516.13) * mm});
            skPoint(sketch, "E2.17.60.0", {"position": v(552.1, -1541.13) * mm});
            skPoint(sketch, "E2.17.61.0", {"position": v(552.1, -1566.13) * mm});
            skPoint(sketch, "E2.17.62.0", {"position": v(552.1, -1591.13) * mm});
            skPoint(sketch, "E2.17.63.0", {"position": v(552.1, -1616.13) * mm});
            skPoint(sketch, "E2.17.64.0", {"position": v(552.1, -1641.13) * mm});
            skPoint(sketch, "E2.17.65.0", {"position": v(552.1, -1666.13) * mm});
            skPoint(sketch, "E2.17.66.0", {"position": v(552.1, -1691.13) * mm});
            skPoint(sketch, "E2.17.67.0", {"position": v(552.1, -1716.13) * mm});
            skPoint(sketch, "E2.17.68.0", {"position": v(552.1, -1741.13) * mm});
            skPoint(sketch, "E2.18.0.0", {"position": v(582.1, -41.13) * mm});
            skPoint(sketch, "E2.18.1.0", {"position": v(582.1, -66.13) * mm});
            skPoint(sketch, "E2.18.2.0", {"position": v(582.1, -91.13) * mm});
            skPoint(sketch, "E2.18.3.0", {"position": v(582.1, -116.13) * mm});
            skPoint(sketch, "E2.18.4.0", {"position": v(582.1, -141.13) * mm});
            skPoint(sketch, "E2.18.5.0", {"position": v(582.1, -166.13) * mm});
            skPoint(sketch, "E2.18.6.0", {"position": v(582.1, -191.13) * mm});
            skPoint(sketch, "E2.18.7.0", {"position": v(582.1, -216.13) * mm});
            skPoint(sketch, "E2.18.8.0", {"position": v(582.1, -241.13) * mm});
            skPoint(sketch, "E2.18.9.0", {"position": v(582.1, -266.13) * mm});
            skPoint(sketch, "E2.18.10.0", {"position": v(582.1, -291.13) * mm});
            skPoint(sketch, "E2.18.11.0", {"position": v(582.1, -316.13) * mm});
            skPoint(sketch, "E2.18.12.0", {"position": v(582.1, -341.13) * mm});
            skPoint(sketch, "E2.18.13.0", {"position": v(582.1, -366.13) * mm});
            skPoint(sketch, "E2.18.14.0", {"position": v(582.1, -391.13) * mm});
            skPoint(sketch, "E2.18.15.0", {"position": v(582.1, -416.13) * mm});
            skPoint(sketch, "E2.18.16.0", {"position": v(582.1, -441.13) * mm});
            skPoint(sketch, "E2.18.17.0", {"position": v(582.1, -466.13) * mm});
            skPoint(sketch, "E2.18.18.0", {"position": v(582.1, -491.13) * mm});
            skPoint(sketch, "E2.18.19.0", {"position": v(582.1, -516.13) * mm});
            skPoint(sketch, "E2.18.20.0", {"position": v(582.1, -541.13) * mm});
            skPoint(sketch, "E2.18.21.0", {"position": v(582.1, -566.13) * mm});
            skPoint(sketch, "E2.18.22.0", {"position": v(582.1, -591.13) * mm});
            skPoint(sketch, "E2.18.23.0", {"position": v(582.1, -616.13) * mm});
            skPoint(sketch, "E2.18.24.0", {"position": v(582.1, -641.13) * mm});
            skPoint(sketch, "E2.18.25.0", {"position": v(582.1, -666.13) * mm});
            skPoint(sketch, "E2.18.26.0", {"position": v(582.1, -691.13) * mm});
            skPoint(sketch, "E2.18.27.0", {"position": v(582.1, -716.13) * mm});
            skPoint(sketch, "E2.18.28.0", {"position": v(582.1, -741.13) * mm});
            skPoint(sketch, "E2.18.29.0", {"position": v(582.1, -766.13) * mm});
            skPoint(sketch, "E2.18.30.0", {"position": v(582.1, -791.13) * mm});
            skPoint(sketch, "E2.18.31.0", {"position": v(582.1, -816.13) * mm});
            skPoint(sketch, "E2.18.32.0", {"position": v(582.1, -841.13) * mm});
            skPoint(sketch, "E2.18.33.0", {"position": v(582.1, -866.13) * mm});
            skPoint(sketch, "E2.18.34.0", {"position": v(582.1, -891.13) * mm});
            skPoint(sketch, "E2.18.35.0", {"position": v(582.1, -916.13) * mm});
            skPoint(sketch, "E2.18.36.0", {"position": v(582.1, -941.13) * mm});
            skPoint(sketch, "E2.18.37.0", {"position": v(582.1, -966.13) * mm});
            skPoint(sketch, "E2.18.38.0", {"position": v(582.1, -991.13) * mm});
            skPoint(sketch, "E2.18.39.0", {"position": v(582.1, -1016.13) * mm});
            skPoint(sketch, "E2.18.40.0", {"position": v(582.1, -1041.13) * mm});
            skPoint(sketch, "E2.18.41.0", {"position": v(582.1, -1066.13) * mm});
            skPoint(sketch, "E2.18.42.0", {"position": v(582.1, -1091.13) * mm});
            skPoint(sketch, "E2.18.43.0", {"position": v(582.1, -1116.13) * mm});
            skPoint(sketch, "E2.18.44.0", {"position": v(582.1, -1141.13) * mm});
            skPoint(sketch, "E2.18.45.0", {"position": v(582.1, -1166.13) * mm});
            skPoint(sketch, "E2.18.46.0", {"position": v(582.1, -1191.13) * mm});
            skPoint(sketch, "E2.18.47.0", {"position": v(582.1, -1216.13) * mm});
            skPoint(sketch, "E2.18.48.0", {"position": v(582.1, -1241.13) * mm});
            skPoint(sketch, "E2.18.49.0", {"position": v(582.1, -1266.13) * mm});
            skPoint(sketch, "E2.18.50.0", {"position": v(582.1, -1291.13) * mm});
            skPoint(sketch, "E2.18.51.0", {"position": v(582.1, -1316.13) * mm});
            skPoint(sketch, "E2.18.52.0", {"position": v(582.1, -1341.13) * mm});
            skPoint(sketch, "E2.18.53.0", {"position": v(582.1, -1366.13) * mm});
            skPoint(sketch, "E2.18.54.0", {"position": v(582.1, -1391.13) * mm});
            skPoint(sketch, "E2.18.55.0", {"position": v(582.1, -1416.13) * mm});
            skPoint(sketch, "E2.18.56.0", {"position": v(582.1, -1441.13) * mm});
            skPoint(sketch, "E2.18.57.0", {"position": v(582.1, -1466.13) * mm});
            skPoint(sketch, "E2.18.58.0", {"position": v(582.1, -1491.13) * mm});
            skPoint(sketch, "E2.18.59.0", {"position": v(582.1, -1516.13) * mm});
            skPoint(sketch, "E2.18.60.0", {"position": v(582.1, -1541.13) * mm});
            skPoint(sketch, "E2.18.61.0", {"position": v(582.1, -1566.13) * mm});
            skPoint(sketch, "E2.18.62.0", {"position": v(582.1, -1591.13) * mm});
            skPoint(sketch, "E2.18.63.0", {"position": v(582.1, -1616.13) * mm});
            skPoint(sketch, "E2.18.64.0", {"position": v(582.1, -1641.13) * mm});
            skPoint(sketch, "E2.18.65.0", {"position": v(582.1, -1666.13) * mm});
            skPoint(sketch, "E2.18.66.0", {"position": v(582.1, -1691.13) * mm});
            skPoint(sketch, "E2.18.67.0", {"position": v(582.1, -1716.13) * mm});
            skPoint(sketch, "E2.18.68.0", {"position": v(582.1, -1741.13) * mm});
            skPoint(sketch, "E2.19.0.0", {"position": v(612.1, -41.13) * mm});
            skPoint(sketch, "E2.19.1.0", {"position": v(612.1, -66.13) * mm});
            skPoint(sketch, "E2.19.2.0", {"position": v(612.1, -91.13) * mm});
            skPoint(sketch, "E2.19.3.0", {"position": v(612.1, -116.13) * mm});
            skPoint(sketch, "E2.19.4.0", {"position": v(612.1, -141.13) * mm});
            skPoint(sketch, "E2.19.5.0", {"position": v(612.1, -166.13) * mm});
            skPoint(sketch, "E2.19.6.0", {"position": v(612.1, -191.13) * mm});
            skPoint(sketch, "E2.19.7.0", {"position": v(612.1, -216.13) * mm});
            skPoint(sketch, "E2.19.8.0", {"position": v(612.1, -241.13) * mm});
            skPoint(sketch, "E2.19.9.0", {"position": v(612.1, -266.13) * mm});
            skPoint(sketch, "E2.19.10.0", {"position": v(612.1, -291.13) * mm});
            skPoint(sketch, "E2.19.11.0", {"position": v(612.1, -316.13) * mm});
            skPoint(sketch, "E2.19.12.0", {"position": v(612.1, -341.13) * mm});
            skPoint(sketch, "E2.19.13.0", {"position": v(612.1, -366.13) * mm});
            skPoint(sketch, "E2.19.14.0", {"position": v(612.1, -391.13) * mm});
            skPoint(sketch, "E2.19.15.0", {"position": v(612.1, -416.13) * mm});
            skPoint(sketch, "E2.19.16.0", {"position": v(612.1, -441.13) * mm});
            skPoint(sketch, "E2.19.17.0", {"position": v(612.1, -466.13) * mm});
            skPoint(sketch, "E2.19.18.0", {"position": v(612.1, -491.13) * mm});
            skPoint(sketch, "E2.19.19.0", {"position": v(612.1, -516.13) * mm});
            skPoint(sketch, "E2.19.20.0", {"position": v(612.1, -541.13) * mm});
            skPoint(sketch, "E2.19.21.0", {"position": v(612.1, -566.13) * mm});
            skPoint(sketch, "E2.19.22.0", {"position": v(612.1, -591.13) * mm});
            skPoint(sketch, "E2.19.23.0", {"position": v(612.1, -616.13) * mm});
            skPoint(sketch, "E2.19.24.0", {"position": v(612.1, -641.13) * mm});
            skPoint(sketch, "E2.19.25.0", {"position": v(612.1, -666.13) * mm});
            skPoint(sketch, "E2.19.26.0", {"position": v(612.1, -691.13) * mm});
            skPoint(sketch, "E2.19.27.0", {"position": v(612.1, -716.13) * mm});
            skPoint(sketch, "E2.19.28.0", {"position": v(612.1, -741.13) * mm});
            skPoint(sketch, "E2.19.29.0", {"position": v(612.1, -766.13) * mm});
            skPoint(sketch, "E2.19.30.0", {"position": v(612.1, -791.13) * mm});
            skPoint(sketch, "E2.19.31.0", {"position": v(612.1, -816.13) * mm});
            skPoint(sketch, "E2.19.32.0", {"position": v(612.1, -841.13) * mm});
            skPoint(sketch, "E2.19.33.0", {"position": v(612.1, -866.13) * mm});
            skPoint(sketch, "E2.19.34.0", {"position": v(612.1, -891.13) * mm});
            skPoint(sketch, "E2.19.35.0", {"position": v(612.1, -916.13) * mm});
            skPoint(sketch, "E2.19.36.0", {"position": v(612.1, -941.13) * mm});
            skPoint(sketch, "E2.19.37.0", {"position": v(612.1, -966.13) * mm});
            skPoint(sketch, "E2.19.38.0", {"position": v(612.1, -991.13) * mm});
            skPoint(sketch, "E2.19.39.0", {"position": v(612.1, -1016.13) * mm});
            skPoint(sketch, "E2.19.40.0", {"position": v(612.1, -1041.13) * mm});
            skPoint(sketch, "E2.19.41.0", {"position": v(612.1, -1066.13) * mm});
            skPoint(sketch, "E2.19.42.0", {"position": v(612.1, -1091.13) * mm});
            skPoint(sketch, "E2.19.43.0", {"position": v(612.1, -1116.13) * mm});
            skPoint(sketch, "E2.19.44.0", {"position": v(612.1, -1141.13) * mm});
            skPoint(sketch, "E2.19.45.0", {"position": v(612.1, -1166.13) * mm});
            skPoint(sketch, "E2.19.46.0", {"position": v(612.1, -1191.13) * mm});
            skPoint(sketch, "E2.19.47.0", {"position": v(612.1, -1216.13) * mm});
            skPoint(sketch, "E2.19.48.0", {"position": v(612.1, -1241.13) * mm});
            skPoint(sketch, "E2.19.49.0", {"position": v(612.1, -1266.13) * mm});
            skPoint(sketch, "E2.19.50.0", {"position": v(612.1, -1291.13) * mm});
            skPoint(sketch, "E2.19.51.0", {"position": v(612.1, -1316.13) * mm});
            skPoint(sketch, "E2.19.52.0", {"position": v(612.1, -1341.13) * mm});
            skPoint(sketch, "E2.19.53.0", {"position": v(612.1, -1366.13) * mm});
            skPoint(sketch, "E2.19.54.0", {"position": v(612.1, -1391.13) * mm});
            skPoint(sketch, "E2.19.55.0", {"position": v(612.1, -1416.13) * mm});
            skPoint(sketch, "E2.19.56.0", {"position": v(612.1, -1441.13) * mm});
            skPoint(sketch, "E2.19.57.0", {"position": v(612.1, -1466.13) * mm});
            skPoint(sketch, "E2.19.58.0", {"position": v(612.1, -1491.13) * mm});
            skPoint(sketch, "E2.19.59.0", {"position": v(612.1, -1516.13) * mm});
            skPoint(sketch, "E2.19.60.0", {"position": v(612.1, -1541.13) * mm});
            skPoint(sketch, "E2.19.61.0", {"position": v(612.1, -1566.13) * mm});
            skPoint(sketch, "E2.19.62.0", {"position": v(612.1, -1591.13) * mm});
            skPoint(sketch, "E2.19.63.0", {"position": v(612.1, -1616.13) * mm});
            skPoint(sketch, "E2.19.64.0", {"position": v(612.1, -1641.13) * mm});
            skPoint(sketch, "E2.19.65.0", {"position": v(612.1, -1666.13) * mm});
            skPoint(sketch, "E2.19.66.0", {"position": v(612.1, -1691.13) * mm});
            skPoint(sketch, "E2.19.67.0", {"position": v(612.1, -1716.13) * mm});
            skPoint(sketch, "E2.19.68.0", {"position": v(612.1, -1741.13) * mm});
            skPoint(sketch, "E2.20.0.0", {"position": v(642.1, -41.13) * mm});
            skPoint(sketch, "E2.20.1.0", {"position": v(642.1, -66.13) * mm});
            skPoint(sketch, "E2.20.2.0", {"position": v(642.1, -91.13) * mm});
            skPoint(sketch, "E2.20.3.0", {"position": v(642.1, -116.13) * mm});
            skPoint(sketch, "E2.20.4.0", {"position": v(642.1, -141.13) * mm});
            skPoint(sketch, "E2.20.5.0", {"position": v(642.1, -166.13) * mm});
            skPoint(sketch, "E2.20.6.0", {"position": v(642.1, -191.13) * mm});
            skPoint(sketch, "E2.20.7.0", {"position": v(642.1, -216.13) * mm});
            skPoint(sketch, "E2.20.8.0", {"position": v(642.1, -241.13) * mm});
            skPoint(sketch, "E2.20.9.0", {"position": v(642.1, -266.13) * mm});
            skPoint(sketch, "E2.20.10.0", {"position": v(642.1, -291.13) * mm});
            skPoint(sketch, "E2.20.11.0", {"position": v(642.1, -316.13) * mm});
            skPoint(sketch, "E2.20.12.0", {"position": v(642.1, -341.13) * mm});
            skPoint(sketch, "E2.20.13.0", {"position": v(642.1, -366.13) * mm});
            skPoint(sketch, "E2.20.14.0", {"position": v(642.1, -391.13) * mm});
            skPoint(sketch, "E2.20.15.0", {"position": v(642.1, -416.13) * mm});
            skPoint(sketch, "E2.20.16.0", {"position": v(642.1, -441.13) * mm});
            skPoint(sketch, "E2.20.17.0", {"position": v(642.1, -466.13) * mm});
            skPoint(sketch, "E2.20.18.0", {"position": v(642.1, -491.13) * mm});
            skPoint(sketch, "E2.20.19.0", {"position": v(642.1, -516.13) * mm});
            skPoint(sketch, "E2.20.20.0", {"position": v(642.1, -541.13) * mm});
            skPoint(sketch, "E2.20.21.0", {"position": v(642.1, -566.13) * mm});
            skPoint(sketch, "E2.20.22.0", {"position": v(642.1, -591.13) * mm});
            skPoint(sketch, "E2.20.23.0", {"position": v(642.1, -616.13) * mm});
            skPoint(sketch, "E2.20.24.0", {"position": v(642.1, -641.13) * mm});
            skPoint(sketch, "E2.20.25.0", {"position": v(642.1, -666.13) * mm});
            skPoint(sketch, "E2.20.26.0", {"position": v(642.1, -691.13) * mm});
            skPoint(sketch, "E2.20.27.0", {"position": v(642.1, -716.13) * mm});
            skPoint(sketch, "E2.20.28.0", {"position": v(642.1, -741.13) * mm});
            skPoint(sketch, "E2.20.29.0", {"position": v(642.1, -766.13) * mm});
            skPoint(sketch, "E2.20.30.0", {"position": v(642.1, -791.13) * mm});
            skPoint(sketch, "E2.20.31.0", {"position": v(642.1, -816.13) * mm});
            skPoint(sketch, "E2.20.32.0", {"position": v(642.1, -841.13) * mm});
            skPoint(sketch, "E2.20.33.0", {"position": v(642.1, -866.13) * mm});
            skPoint(sketch, "E2.20.34.0", {"position": v(642.1, -891.13) * mm});
            skPoint(sketch, "E2.20.35.0", {"position": v(642.1, -916.13) * mm});
            skPoint(sketch, "E2.20.36.0", {"position": v(642.1, -941.13) * mm});
            skPoint(sketch, "E2.20.37.0", {"position": v(642.1, -966.13) * mm});
            skPoint(sketch, "E2.20.38.0", {"position": v(642.1, -991.13) * mm});
            skPoint(sketch, "E2.20.39.0", {"position": v(642.1, -1016.13) * mm});
            skPoint(sketch, "E2.20.40.0", {"position": v(642.1, -1041.13) * mm});
            skPoint(sketch, "E2.20.41.0", {"position": v(642.1, -1066.13) * mm});
            skPoint(sketch, "E2.20.42.0", {"position": v(642.1, -1091.13) * mm});
            skPoint(sketch, "E2.20.43.0", {"position": v(642.1, -1116.13) * mm});
            skPoint(sketch, "E2.20.44.0", {"position": v(642.1, -1141.13) * mm});
            skPoint(sketch, "E2.20.45.0", {"position": v(642.1, -1166.13) * mm});
            skPoint(sketch, "E2.20.46.0", {"position": v(642.1, -1191.13) * mm});
            skPoint(sketch, "E2.20.47.0", {"position": v(642.1, -1216.13) * mm});
            skPoint(sketch, "E2.20.48.0", {"position": v(642.1, -1241.13) * mm});
            skPoint(sketch, "E2.20.49.0", {"position": v(642.1, -1266.13) * mm});
            skPoint(sketch, "E2.20.50.0", {"position": v(642.1, -1291.13) * mm});
            skPoint(sketch, "E2.20.51.0", {"position": v(642.1, -1316.13) * mm});
            skPoint(sketch, "E2.20.52.0", {"position": v(642.1, -1341.13) * mm});
            skPoint(sketch, "E2.20.53.0", {"position": v(642.1, -1366.13) * mm});
            skPoint(sketch, "E2.20.54.0", {"position": v(642.1, -1391.13) * mm});
            skPoint(sketch, "E2.20.55.0", {"position": v(642.1, -1416.13) * mm});
            skPoint(sketch, "E2.20.56.0", {"position": v(642.1, -1441.13) * mm});
            skPoint(sketch, "E2.20.57.0", {"position": v(642.1, -1466.13) * mm});
            skPoint(sketch, "E2.20.58.0", {"position": v(642.1, -1491.13) * mm});
            skPoint(sketch, "E2.20.59.0", {"position": v(642.1, -1516.13) * mm});
            skPoint(sketch, "E2.20.60.0", {"position": v(642.1, -1541.13) * mm});
            skPoint(sketch, "E2.20.61.0", {"position": v(642.1, -1566.13) * mm});
            skPoint(sketch, "E2.20.62.0", {"position": v(642.1, -1591.13) * mm});
            skPoint(sketch, "E2.20.63.0", {"position": v(642.1, -1616.13) * mm});
            skPoint(sketch, "E2.20.64.0", {"position": v(642.1, -1641.13) * mm});
            skPoint(sketch, "E2.20.65.0", {"position": v(642.1, -1666.13) * mm});
            skPoint(sketch, "E2.20.66.0", {"position": v(642.1, -1691.13) * mm});
            skPoint(sketch, "E2.20.67.0", {"position": v(642.1, -1716.13) * mm});
            skPoint(sketch, "E2.20.68.0", {"position": v(642.1, -1741.13) * mm});
            skPoint(sketch, "E2.21.0.0", {"position": v(672.1, -41.13) * mm});
            skPoint(sketch, "E2.21.1.0", {"position": v(672.1, -66.13) * mm});
            skPoint(sketch, "E2.21.2.0", {"position": v(672.1, -91.13) * mm});
            skPoint(sketch, "E2.21.3.0", {"position": v(672.1, -116.13) * mm});
            skPoint(sketch, "E2.21.4.0", {"position": v(672.1, -141.13) * mm});
            skPoint(sketch, "E2.21.5.0", {"position": v(672.1, -166.13) * mm});
            skPoint(sketch, "E2.21.6.0", {"position": v(672.1, -191.13) * mm});
            skPoint(sketch, "E2.21.7.0", {"position": v(672.1, -216.13) * mm});
            skPoint(sketch, "E2.21.8.0", {"position": v(672.1, -241.13) * mm});
            skPoint(sketch, "E2.21.9.0", {"position": v(672.1, -266.13) * mm});
            skPoint(sketch, "E2.21.10.0", {"position": v(672.1, -291.13) * mm});
            skPoint(sketch, "E2.21.11.0", {"position": v(672.1, -316.13) * mm});
            skPoint(sketch, "E2.21.12.0", {"position": v(672.1, -341.13) * mm});
            skPoint(sketch, "E2.21.13.0", {"position": v(672.1, -366.13) * mm});
            skPoint(sketch, "E2.21.14.0", {"position": v(672.1, -391.13) * mm});
            skPoint(sketch, "E2.21.15.0", {"position": v(672.1, -416.13) * mm});
            skPoint(sketch, "E2.21.16.0", {"position": v(672.1, -441.13) * mm});
            skPoint(sketch, "E2.21.17.0", {"position": v(672.1, -466.13) * mm});
            skPoint(sketch, "E2.21.18.0", {"position": v(672.1, -491.13) * mm});
            skPoint(sketch, "E2.21.19.0", {"position": v(672.1, -516.13) * mm});
            skPoint(sketch, "E2.21.20.0", {"position": v(672.1, -541.13) * mm});
            skPoint(sketch, "E2.21.21.0", {"position": v(672.1, -566.13) * mm});
            skPoint(sketch, "E2.21.22.0", {"position": v(672.1, -591.13) * mm});
            skPoint(sketch, "E2.21.23.0", {"position": v(672.1, -616.13) * mm});
            skPoint(sketch, "E2.21.24.0", {"position": v(672.1, -641.13) * mm});
            skPoint(sketch, "E2.21.25.0", {"position": v(672.1, -666.13) * mm});
            skPoint(sketch, "E2.21.26.0", {"position": v(672.1, -691.13) * mm});
            skPoint(sketch, "E2.21.27.0", {"position": v(672.1, -716.13) * mm});
            skPoint(sketch, "E2.21.28.0", {"position": v(672.1, -741.13) * mm});
            skPoint(sketch, "E2.21.29.0", {"position": v(672.1, -766.13) * mm});
            skPoint(sketch, "E2.21.30.0", {"position": v(672.1, -791.13) * mm});
            skPoint(sketch, "E2.21.31.0", {"position": v(672.1, -816.13) * mm});
            skPoint(sketch, "E2.21.32.0", {"position": v(672.1, -841.13) * mm});
            skPoint(sketch, "E2.21.33.0", {"position": v(672.1, -866.13) * mm});
            skPoint(sketch, "E2.21.34.0", {"position": v(672.1, -891.13) * mm});
            skPoint(sketch, "E2.21.35.0", {"position": v(672.1, -916.13) * mm});
            skPoint(sketch, "E2.21.36.0", {"position": v(672.1, -941.13) * mm});
            skPoint(sketch, "E2.21.37.0", {"position": v(672.1, -966.13) * mm});
            skPoint(sketch, "E2.21.38.0", {"position": v(672.1, -991.13) * mm});
            skPoint(sketch, "E2.21.39.0", {"position": v(672.1, -1016.13) * mm});
            skPoint(sketch, "E2.21.40.0", {"position": v(672.1, -1041.13) * mm});
            skPoint(sketch, "E2.21.41.0", {"position": v(672.1, -1066.13) * mm});
            skPoint(sketch, "E2.21.42.0", {"position": v(672.1, -1091.13) * mm});
            skPoint(sketch, "E2.21.43.0", {"position": v(672.1, -1116.13) * mm});
            skPoint(sketch, "E2.21.44.0", {"position": v(672.1, -1141.13) * mm});
            skPoint(sketch, "E2.21.45.0", {"position": v(672.1, -1166.13) * mm});
            skPoint(sketch, "E2.21.46.0", {"position": v(672.1, -1191.13) * mm});
            skPoint(sketch, "E2.21.47.0", {"position": v(672.1, -1216.13) * mm});
            skPoint(sketch, "E2.21.48.0", {"position": v(672.1, -1241.13) * mm});
            skPoint(sketch, "E2.21.49.0", {"position": v(672.1, -1266.13) * mm});
            skPoint(sketch, "E2.21.50.0", {"position": v(672.1, -1291.13) * mm});
            skPoint(sketch, "E2.21.51.0", {"position": v(672.1, -1316.13) * mm});
            skPoint(sketch, "E2.21.52.0", {"position": v(672.1, -1341.13) * mm});
            skPoint(sketch, "E2.21.53.0", {"position": v(672.1, -1366.13) * mm});
            skPoint(sketch, "E2.21.54.0", {"position": v(672.1, -1391.13) * mm});
            skPoint(sketch, "E2.21.55.0", {"position": v(672.1, -1416.13) * mm});
            skPoint(sketch, "E2.21.56.0", {"position": v(672.1, -1441.13) * mm});
            skPoint(sketch, "E2.21.57.0", {"position": v(672.1, -1466.13) * mm});
            skPoint(sketch, "E2.21.58.0", {"position": v(672.1, -1491.13) * mm});
            skPoint(sketch, "E2.21.59.0", {"position": v(672.1, -1516.13) * mm});
            skPoint(sketch, "E2.21.60.0", {"position": v(672.1, -1541.13) * mm});
            skPoint(sketch, "E2.21.61.0", {"position": v(672.1, -1566.13) * mm});
            skPoint(sketch, "E2.21.62.0", {"position": v(672.1, -1591.13) * mm});
            skPoint(sketch, "E2.21.63.0", {"position": v(672.1, -1616.13) * mm});
            skPoint(sketch, "E2.21.64.0", {"position": v(672.1, -1641.13) * mm});
            skPoint(sketch, "E2.21.65.0", {"position": v(672.1, -1666.13) * mm});
            skPoint(sketch, "E2.21.66.0", {"position": v(672.1, -1691.13) * mm});
            skPoint(sketch, "E2.21.67.0", {"position": v(672.1, -1716.13) * mm});
            skPoint(sketch, "E2.21.68.0", {"position": v(672.1, -1741.13) * mm});
            skPoint(sketch, "E2.22.0.0", {"position": v(702.1, -41.13) * mm});
            skPoint(sketch, "E2.22.1.0", {"position": v(702.1, -66.13) * mm});
            skPoint(sketch, "E2.22.2.0", {"position": v(702.1, -91.13) * mm});
            skPoint(sketch, "E2.22.3.0", {"position": v(702.1, -116.13) * mm});
            skPoint(sketch, "E2.22.4.0", {"position": v(702.1, -141.13) * mm});
            skPoint(sketch, "E2.22.5.0", {"position": v(702.1, -166.13) * mm});
            skPoint(sketch, "E2.22.6.0", {"position": v(702.1, -191.13) * mm});
            skPoint(sketch, "E2.22.7.0", {"position": v(702.1, -216.13) * mm});
            skPoint(sketch, "E2.22.8.0", {"position": v(702.1, -241.13) * mm});
            skPoint(sketch, "E2.22.9.0", {"position": v(702.1, -266.13) * mm});
            skPoint(sketch, "E2.22.10.0", {"position": v(702.1, -291.13) * mm});
            skPoint(sketch, "E2.22.11.0", {"position": v(702.1, -316.13) * mm});
            skPoint(sketch, "E2.22.12.0", {"position": v(702.1, -341.13) * mm});
            skPoint(sketch, "E2.22.13.0", {"position": v(702.1, -366.13) * mm});
            skPoint(sketch, "E2.22.14.0", {"position": v(702.1, -391.13) * mm});
            skPoint(sketch, "E2.22.15.0", {"position": v(702.1, -416.13) * mm});
            skPoint(sketch, "E2.22.16.0", {"position": v(702.1, -441.13) * mm});
            skPoint(sketch, "E2.22.17.0", {"position": v(702.1, -466.13) * mm});
            skPoint(sketch, "E2.22.18.0", {"position": v(702.1, -491.13) * mm});
            skPoint(sketch, "E2.22.19.0", {"position": v(702.1, -516.13) * mm});
            skPoint(sketch, "E2.22.20.0", {"position": v(702.1, -541.13) * mm});
            skPoint(sketch, "E2.22.21.0", {"position": v(702.1, -566.13) * mm});
            skPoint(sketch, "E2.22.22.0", {"position": v(702.1, -591.13) * mm});
            skPoint(sketch, "E2.22.23.0", {"position": v(702.1, -616.13) * mm});
            skPoint(sketch, "E2.22.24.0", {"position": v(702.1, -641.13) * mm});
            skPoint(sketch, "E2.22.25.0", {"position": v(702.1, -666.13) * mm});
            skPoint(sketch, "E2.22.26.0", {"position": v(702.1, -691.13) * mm});
            skPoint(sketch, "E2.22.27.0", {"position": v(702.1, -716.13) * mm});
            skPoint(sketch, "E2.22.28.0", {"position": v(702.1, -741.13) * mm});
            skPoint(sketch, "E2.22.29.0", {"position": v(702.1, -766.13) * mm});
            skPoint(sketch, "E2.22.30.0", {"position": v(702.1, -791.13) * mm});
            skPoint(sketch, "E2.22.31.0", {"position": v(702.1, -816.13) * mm});
            skPoint(sketch, "E2.22.32.0", {"position": v(702.1, -841.13) * mm});
            skPoint(sketch, "E2.22.33.0", {"position": v(702.1, -866.13) * mm});
            skPoint(sketch, "E2.22.34.0", {"position": v(702.1, -891.13) * mm});
            skPoint(sketch, "E2.22.35.0", {"position": v(702.1, -916.13) * mm});
            skPoint(sketch, "E2.22.36.0", {"position": v(702.1, -941.13) * mm});
            skPoint(sketch, "E2.22.37.0", {"position": v(702.1, -966.13) * mm});
            skPoint(sketch, "E2.22.38.0", {"position": v(702.1, -991.13) * mm});
            skPoint(sketch, "E2.22.39.0", {"position": v(702.1, -1016.13) * mm});
            skPoint(sketch, "E2.22.40.0", {"position": v(702.1, -1041.13) * mm});
            skPoint(sketch, "E2.22.41.0", {"position": v(702.1, -1066.13) * mm});
            skPoint(sketch, "E2.22.42.0", {"position": v(702.1, -1091.13) * mm});
            skPoint(sketch, "E2.22.43.0", {"position": v(702.1, -1116.13) * mm});
            skPoint(sketch, "E2.22.44.0", {"position": v(702.1, -1141.13) * mm});
            skPoint(sketch, "E2.22.45.0", {"position": v(702.1, -1166.13) * mm});
            skPoint(sketch, "E2.22.46.0", {"position": v(702.1, -1191.13) * mm});
            skPoint(sketch, "E2.22.47.0", {"position": v(702.1, -1216.13) * mm});
            skPoint(sketch, "E2.22.48.0", {"position": v(702.1, -1241.13) * mm});
            skPoint(sketch, "E2.22.49.0", {"position": v(702.1, -1266.13) * mm});
            skPoint(sketch, "E2.22.50.0", {"position": v(702.1, -1291.13) * mm});
            skPoint(sketch, "E2.22.51.0", {"position": v(702.1, -1316.13) * mm});
            skPoint(sketch, "E2.22.52.0", {"position": v(702.1, -1341.13) * mm});
            skPoint(sketch, "E2.22.53.0", {"position": v(702.1, -1366.13) * mm});
            skPoint(sketch, "E2.22.54.0", {"position": v(702.1, -1391.13) * mm});
            skPoint(sketch, "E2.22.55.0", {"position": v(702.1, -1416.13) * mm});
            skPoint(sketch, "E2.22.56.0", {"position": v(702.1, -1441.13) * mm});
            skPoint(sketch, "E2.22.57.0", {"position": v(702.1, -1466.13) * mm});
            skPoint(sketch, "E2.22.58.0", {"position": v(702.1, -1491.13) * mm});
            skPoint(sketch, "E2.22.59.0", {"position": v(702.1, -1516.13) * mm});
            skPoint(sketch, "E2.22.60.0", {"position": v(702.1, -1541.13) * mm});
            skPoint(sketch, "E2.22.61.0", {"position": v(702.1, -1566.13) * mm});
            skPoint(sketch, "E2.22.62.0", {"position": v(702.1, -1591.13) * mm});
            skPoint(sketch, "E2.22.63.0", {"position": v(702.1, -1616.13) * mm});
            skPoint(sketch, "E2.22.64.0", {"position": v(702.1, -1641.13) * mm});
            skPoint(sketch, "E2.22.65.0", {"position": v(702.1, -1666.13) * mm});
            skPoint(sketch, "E2.22.66.0", {"position": v(702.1, -1691.13) * mm});
            skPoint(sketch, "E2.22.67.0", {"position": v(702.1, -1716.13) * mm});
            skPoint(sketch, "E2.22.68.0", {"position": v(702.1, -1741.13) * mm});
            skPoint(sketch, "E2.23.0.0", {"position": v(732.1, -41.13) * mm});
            skPoint(sketch, "E2.23.1.0", {"position": v(732.1, -66.13) * mm});
            skPoint(sketch, "E2.23.2.0", {"position": v(732.1, -91.13) * mm});
            skPoint(sketch, "E2.23.3.0", {"position": v(732.1, -116.13) * mm});
            skPoint(sketch, "E2.23.4.0", {"position": v(732.1, -141.13) * mm});
            skPoint(sketch, "E2.23.5.0", {"position": v(732.1, -166.13) * mm});
            skPoint(sketch, "E2.23.6.0", {"position": v(732.1, -191.13) * mm});
            skPoint(sketch, "E2.23.7.0", {"position": v(732.1, -216.13) * mm});
            skPoint(sketch, "E2.23.8.0", {"position": v(732.1, -241.13) * mm});
            skPoint(sketch, "E2.23.9.0", {"position": v(732.1, -266.13) * mm});
            skPoint(sketch, "E2.23.10.0", {"position": v(732.1, -291.13) * mm});
            skPoint(sketch, "E2.23.11.0", {"position": v(732.1, -316.13) * mm});
            skPoint(sketch, "E2.23.12.0", {"position": v(732.1, -341.13) * mm});
            skPoint(sketch, "E2.23.13.0", {"position": v(732.1, -366.13) * mm});
            skPoint(sketch, "E2.23.14.0", {"position": v(732.1, -391.13) * mm});
            skPoint(sketch, "E2.23.15.0", {"position": v(732.1, -416.13) * mm});
            skPoint(sketch, "E2.23.16.0", {"position": v(732.1, -441.13) * mm});
            skPoint(sketch, "E2.23.17.0", {"position": v(732.1, -466.13) * mm});
            skPoint(sketch, "E2.23.18.0", {"position": v(732.1, -491.13) * mm});
            skPoint(sketch, "E2.23.19.0", {"position": v(732.1, -516.13) * mm});
            skPoint(sketch, "E2.23.20.0", {"position": v(732.1, -541.13) * mm});
            skPoint(sketch, "E2.23.21.0", {"position": v(732.1, -566.13) * mm});
            skPoint(sketch, "E2.23.22.0", {"position": v(732.1, -591.13) * mm});
            skPoint(sketch, "E2.23.23.0", {"position": v(732.1, -616.13) * mm});
            skPoint(sketch, "E2.23.24.0", {"position": v(732.1, -641.13) * mm});
            skPoint(sketch, "E2.23.25.0", {"position": v(732.1, -666.13) * mm});
            skPoint(sketch, "E2.23.26.0", {"position": v(732.1, -691.13) * mm});
            skPoint(sketch, "E2.23.27.0", {"position": v(732.1, -716.13) * mm});
            skPoint(sketch, "E2.23.28.0", {"position": v(732.1, -741.13) * mm});
            skPoint(sketch, "E2.23.29.0", {"position": v(732.1, -766.13) * mm});
            skPoint(sketch, "E2.23.30.0", {"position": v(732.1, -791.13) * mm});
            skPoint(sketch, "E2.23.31.0", {"position": v(732.1, -816.13) * mm});
            skPoint(sketch, "E2.23.32.0", {"position": v(732.1, -841.13) * mm});
            skPoint(sketch, "E2.23.33.0", {"position": v(732.1, -866.13) * mm});
            skPoint(sketch, "E2.23.34.0", {"position": v(732.1, -891.13) * mm});
            skPoint(sketch, "E2.23.35.0", {"position": v(732.1, -916.13) * mm});
            skPoint(sketch, "E2.23.36.0", {"position": v(732.1, -941.13) * mm});
            skPoint(sketch, "E2.23.37.0", {"position": v(732.1, -966.13) * mm});
            skPoint(sketch, "E2.23.38.0", {"position": v(732.1, -991.13) * mm});
            skPoint(sketch, "E2.23.39.0", {"position": v(732.1, -1016.13) * mm});
            skPoint(sketch, "E2.23.40.0", {"position": v(732.1, -1041.13) * mm});
            skPoint(sketch, "E2.23.41.0", {"position": v(732.1, -1066.13) * mm});
            skPoint(sketch, "E2.23.42.0", {"position": v(732.1, -1091.13) * mm});
            skPoint(sketch, "E2.23.43.0", {"position": v(732.1, -1116.13) * mm});
            skPoint(sketch, "E2.23.44.0", {"position": v(732.1, -1141.13) * mm});
            skPoint(sketch, "E2.23.45.0", {"position": v(732.1, -1166.13) * mm});
            skPoint(sketch, "E2.23.46.0", {"position": v(732.1, -1191.13) * mm});
            skPoint(sketch, "E2.23.47.0", {"position": v(732.1, -1216.13) * mm});
            skPoint(sketch, "E2.23.48.0", {"position": v(732.1, -1241.13) * mm});
            skPoint(sketch, "E2.23.49.0", {"position": v(732.1, -1266.13) * mm});
            skPoint(sketch, "E2.23.50.0", {"position": v(732.1, -1291.13) * mm});
            skPoint(sketch, "E2.23.51.0", {"position": v(732.1, -1316.13) * mm});
            skPoint(sketch, "E2.23.52.0", {"position": v(732.1, -1341.13) * mm});
            skPoint(sketch, "E2.23.53.0", {"position": v(732.1, -1366.13) * mm});
            skPoint(sketch, "E2.23.54.0", {"position": v(732.1, -1391.13) * mm});
            skPoint(sketch, "E2.23.55.0", {"position": v(732.1, -1416.13) * mm});
            skPoint(sketch, "E2.23.56.0", {"position": v(732.1, -1441.13) * mm});
            skPoint(sketch, "E2.23.57.0", {"position": v(732.1, -1466.13) * mm});
            skPoint(sketch, "E2.23.58.0", {"position": v(732.1, -1491.13) * mm});
            skPoint(sketch, "E2.23.59.0", {"position": v(732.1, -1516.13) * mm});
            skPoint(sketch, "E2.23.60.0", {"position": v(732.1, -1541.13) * mm});
            skPoint(sketch, "E2.23.61.0", {"position": v(732.1, -1566.13) * mm});
            skPoint(sketch, "E2.23.62.0", {"position": v(732.1, -1591.13) * mm});
            skPoint(sketch, "E2.23.63.0", {"position": v(732.1, -1616.13) * mm});
            skPoint(sketch, "E2.23.64.0", {"position": v(732.1, -1641.13) * mm});
            skPoint(sketch, "E2.23.65.0", {"position": v(732.1, -1666.13) * mm});
            skPoint(sketch, "E2.23.66.0", {"position": v(732.1, -1691.13) * mm});
            skPoint(sketch, "E2.23.67.0", {"position": v(732.1, -1716.13) * mm});
            skPoint(sketch, "E2.23.68.0", {"position": v(732.1, -1741.13) * mm});
            skPoint(sketch, "E2.24.0.0", {"position": v(762.1, -41.13) * mm});
            skPoint(sketch, "E2.24.1.0", {"position": v(762.1, -66.13) * mm});
            skPoint(sketch, "E2.24.2.0", {"position": v(762.1, -91.13) * mm});
            skPoint(sketch, "E2.24.3.0", {"position": v(762.1, -116.13) * mm});
            skPoint(sketch, "E2.24.4.0", {"position": v(762.1, -141.13) * mm});
            skPoint(sketch, "E2.24.5.0", {"position": v(762.1, -166.13) * mm});
            skPoint(sketch, "E2.24.6.0", {"position": v(762.1, -191.13) * mm});
            skPoint(sketch, "E2.24.7.0", {"position": v(762.1, -216.13) * mm});
            skPoint(sketch, "E2.24.8.0", {"position": v(762.1, -241.13) * mm});
            skPoint(sketch, "E2.24.9.0", {"position": v(762.1, -266.13) * mm});
            skPoint(sketch, "E2.24.10.0", {"position": v(762.1, -291.13) * mm});
            skPoint(sketch, "E2.24.11.0", {"position": v(762.1, -316.13) * mm});
            skPoint(sketch, "E2.24.12.0", {"position": v(762.1, -341.13) * mm});
            skPoint(sketch, "E2.24.13.0", {"position": v(762.1, -366.13) * mm});
            skPoint(sketch, "E2.24.14.0", {"position": v(762.1, -391.13) * mm});
            skPoint(sketch, "E2.24.15.0", {"position": v(762.1, -416.13) * mm});
            skPoint(sketch, "E2.24.16.0", {"position": v(762.1, -441.13) * mm});
            skPoint(sketch, "E2.24.17.0", {"position": v(762.1, -466.13) * mm});
            skPoint(sketch, "E2.24.18.0", {"position": v(762.1, -491.13) * mm});
            skPoint(sketch, "E2.24.19.0", {"position": v(762.1, -516.13) * mm});
            skPoint(sketch, "E2.24.20.0", {"position": v(762.1, -541.13) * mm});
            skPoint(sketch, "E2.24.21.0", {"position": v(762.1, -566.13) * mm});
            skPoint(sketch, "E2.24.22.0", {"position": v(762.1, -591.13) * mm});
            skPoint(sketch, "E2.24.23.0", {"position": v(762.1, -616.13) * mm});
            skPoint(sketch, "E2.24.24.0", {"position": v(762.1, -641.13) * mm});
            skPoint(sketch, "E2.24.25.0", {"position": v(762.1, -666.13) * mm});
            skPoint(sketch, "E2.24.26.0", {"position": v(762.1, -691.13) * mm});
            skPoint(sketch, "E2.24.27.0", {"position": v(762.1, -716.13) * mm});
            skPoint(sketch, "E2.24.28.0", {"position": v(762.1, -741.13) * mm});
            skPoint(sketch, "E2.24.29.0", {"position": v(762.1, -766.13) * mm});
            skPoint(sketch, "E2.24.30.0", {"position": v(762.1, -791.13) * mm});
            skPoint(sketch, "E2.24.31.0", {"position": v(762.1, -816.13) * mm});
            skPoint(sketch, "E2.24.32.0", {"position": v(762.1, -841.13) * mm});
            skPoint(sketch, "E2.24.33.0", {"position": v(762.1, -866.13) * mm});
            skPoint(sketch, "E2.24.34.0", {"position": v(762.1, -891.13) * mm});
            skPoint(sketch, "E2.24.35.0", {"position": v(762.1, -916.13) * mm});
            skPoint(sketch, "E2.24.36.0", {"position": v(762.1, -941.13) * mm});
            skPoint(sketch, "E2.24.37.0", {"position": v(762.1, -966.13) * mm});
            skPoint(sketch, "E2.24.38.0", {"position": v(762.1, -991.13) * mm});
            skPoint(sketch, "E2.24.39.0", {"position": v(762.1, -1016.13) * mm});
            skPoint(sketch, "E2.24.40.0", {"position": v(762.1, -1041.13) * mm});
            skPoint(sketch, "E2.24.41.0", {"position": v(762.1, -1066.13) * mm});
            skPoint(sketch, "E2.24.42.0", {"position": v(762.1, -1091.13) * mm});
            skPoint(sketch, "E2.24.43.0", {"position": v(762.1, -1116.13) * mm});
            skPoint(sketch, "E2.24.44.0", {"position": v(762.1, -1141.13) * mm});
            skPoint(sketch, "E2.24.45.0", {"position": v(762.1, -1166.13) * mm});
            skPoint(sketch, "E2.24.46.0", {"position": v(762.1, -1191.13) * mm});
            skPoint(sketch, "E2.24.47.0", {"position": v(762.1, -1216.13) * mm});
            skPoint(sketch, "E2.24.48.0", {"position": v(762.1, -1241.13) * mm});
            skPoint(sketch, "E2.24.49.0", {"position": v(762.1, -1266.13) * mm});
            skPoint(sketch, "E2.24.50.0", {"position": v(762.1, -1291.13) * mm});
            skPoint(sketch, "E2.24.51.0", {"position": v(762.1, -1316.13) * mm});
            skPoint(sketch, "E2.24.52.0", {"position": v(762.1, -1341.13) * mm});
            skPoint(sketch, "E2.24.53.0", {"position": v(762.1, -1366.13) * mm});
            skPoint(sketch, "E2.24.54.0", {"position": v(762.1, -1391.13) * mm});
            skPoint(sketch, "E2.24.55.0", {"position": v(762.1, -1416.13) * mm});
            skPoint(sketch, "E2.24.56.0", {"position": v(762.1, -1441.13) * mm});
            skPoint(sketch, "E2.24.57.0", {"position": v(762.1, -1466.13) * mm});
            skPoint(sketch, "E2.24.58.0", {"position": v(762.1, -1491.13) * mm});
            skPoint(sketch, "E2.24.59.0", {"position": v(762.1, -1516.13) * mm});
            skPoint(sketch, "E2.24.60.0", {"position": v(762.1, -1541.13) * mm});
            skPoint(sketch, "E2.24.61.0", {"position": v(762.1, -1566.13) * mm});
            skPoint(sketch, "E2.24.62.0", {"position": v(762.1, -1591.13) * mm});
            skPoint(sketch, "E2.24.63.0", {"position": v(762.1, -1616.13) * mm});
            skPoint(sketch, "E2.24.64.0", {"position": v(762.1, -1641.13) * mm});
            skPoint(sketch, "E2.24.65.0", {"position": v(762.1, -1666.13) * mm});
            skPoint(sketch, "E2.24.66.0", {"position": v(762.1, -1691.13) * mm});
            skPoint(sketch, "E2.24.67.0", {"position": v(762.1, -1716.13) * mm});
            skPoint(sketch, "E2.24.68.0", {"position": v(762.1, -1741.13) * mm});
            skPoint(sketch, "E2.25.0.0", {"position": v(792.1, -41.13) * mm});
            skPoint(sketch, "E2.25.1.0", {"position": v(792.1, -66.13) * mm});
            skPoint(sketch, "E2.25.2.0", {"position": v(792.1, -91.13) * mm});
            skPoint(sketch, "E2.25.3.0", {"position": v(792.1, -116.13) * mm});
            skPoint(sketch, "E2.25.4.0", {"position": v(792.1, -141.13) * mm});
            skPoint(sketch, "E2.25.5.0", {"position": v(792.1, -166.13) * mm});
            skPoint(sketch, "E2.25.6.0", {"position": v(792.1, -191.13) * mm});
            skPoint(sketch, "E2.25.7.0", {"position": v(792.1, -216.13) * mm});
            skPoint(sketch, "E2.25.8.0", {"position": v(792.1, -241.13) * mm});
            skPoint(sketch, "E2.25.9.0", {"position": v(792.1, -266.13) * mm});
            skPoint(sketch, "E2.25.10.0", {"position": v(792.1, -291.13) * mm});
            skPoint(sketch, "E2.25.11.0", {"position": v(792.1, -316.13) * mm});
            skPoint(sketch, "E2.25.12.0", {"position": v(792.1, -341.13) * mm});
            skPoint(sketch, "E2.25.13.0", {"position": v(792.1, -366.13) * mm});
            skPoint(sketch, "E2.25.14.0", {"position": v(792.1, -391.13) * mm});
            skPoint(sketch, "E2.25.15.0", {"position": v(792.1, -416.13) * mm});
            skPoint(sketch, "E2.25.16.0", {"position": v(792.1, -441.13) * mm});
            skPoint(sketch, "E2.25.17.0", {"position": v(792.1, -466.13) * mm});
            skPoint(sketch, "E2.25.18.0", {"position": v(792.1, -491.13) * mm});
            skPoint(sketch, "E2.25.19.0", {"position": v(792.1, -516.13) * mm});
            skPoint(sketch, "E2.25.20.0", {"position": v(792.1, -541.13) * mm});
            skPoint(sketch, "E2.25.21.0", {"position": v(792.1, -566.13) * mm});
            skPoint(sketch, "E2.25.22.0", {"position": v(792.1, -591.13) * mm});
            skPoint(sketch, "E2.25.23.0", {"position": v(792.1, -616.13) * mm});
            skPoint(sketch, "E2.25.24.0", {"position": v(792.1, -641.13) * mm});
            skPoint(sketch, "E2.25.25.0", {"position": v(792.1, -666.13) * mm});
            skPoint(sketch, "E2.25.26.0", {"position": v(792.1, -691.13) * mm});
            skPoint(sketch, "E2.25.27.0", {"position": v(792.1, -716.13) * mm});
            skPoint(sketch, "E2.25.28.0", {"position": v(792.1, -741.13) * mm});
            skPoint(sketch, "E2.25.29.0", {"position": v(792.1, -766.13) * mm});
            skPoint(sketch, "E2.25.30.0", {"position": v(792.1, -791.13) * mm});
            skPoint(sketch, "E2.25.31.0", {"position": v(792.1, -816.13) * mm});
            skPoint(sketch, "E2.25.32.0", {"position": v(792.1, -841.13) * mm});
            skPoint(sketch, "E2.25.33.0", {"position": v(792.1, -866.13) * mm});
            skPoint(sketch, "E2.25.34.0", {"position": v(792.1, -891.13) * mm});
            skPoint(sketch, "E2.25.35.0", {"position": v(792.1, -916.13) * mm});
            skPoint(sketch, "E2.25.36.0", {"position": v(792.1, -941.13) * mm});
            skPoint(sketch, "E2.25.37.0", {"position": v(792.1, -966.13) * mm});
            skPoint(sketch, "E2.25.38.0", {"position": v(792.1, -991.13) * mm});
            skPoint(sketch, "E2.25.39.0", {"position": v(792.1, -1016.13) * mm});
            skPoint(sketch, "E2.25.40.0", {"position": v(792.1, -1041.13) * mm});
            skPoint(sketch, "E2.25.41.0", {"position": v(792.1, -1066.13) * mm});
            skPoint(sketch, "E2.25.42.0", {"position": v(792.1, -1091.13) * mm});
            skPoint(sketch, "E2.25.43.0", {"position": v(792.1, -1116.13) * mm});
            skPoint(sketch, "E2.25.44.0", {"position": v(792.1, -1141.13) * mm});
            skPoint(sketch, "E2.25.45.0", {"position": v(792.1, -1166.13) * mm});
            skPoint(sketch, "E2.25.46.0", {"position": v(792.1, -1191.13) * mm});
            skPoint(sketch, "E2.25.47.0", {"position": v(792.1, -1216.13) * mm});
            skPoint(sketch, "E2.25.48.0", {"position": v(792.1, -1241.13) * mm});
            skPoint(sketch, "E2.25.49.0", {"position": v(792.1, -1266.13) * mm});
            skPoint(sketch, "E2.25.50.0", {"position": v(792.1, -1291.13) * mm});
            skPoint(sketch, "E2.25.51.0", {"position": v(792.1, -1316.13) * mm});
            skPoint(sketch, "E2.25.52.0", {"position": v(792.1, -1341.13) * mm});
            skPoint(sketch, "E2.25.53.0", {"position": v(792.1, -1366.13) * mm});
            skPoint(sketch, "E2.25.54.0", {"position": v(792.1, -1391.13) * mm});
            skPoint(sketch, "E2.25.55.0", {"position": v(792.1, -1416.13) * mm});
            skPoint(sketch, "E2.25.56.0", {"position": v(792.1, -1441.13) * mm});
            skPoint(sketch, "E2.25.57.0", {"position": v(792.1, -1466.13) * mm});
            skPoint(sketch, "E2.25.58.0", {"position": v(792.1, -1491.13) * mm});
            skPoint(sketch, "E2.25.59.0", {"position": v(792.1, -1516.13) * mm});
            skPoint(sketch, "E2.25.60.0", {"position": v(792.1, -1541.13) * mm});
            skPoint(sketch, "E2.25.61.0", {"position": v(792.1, -1566.13) * mm});
            skPoint(sketch, "E2.25.62.0", {"position": v(792.1, -1591.13) * mm});
            skPoint(sketch, "E2.25.63.0", {"position": v(792.1, -1616.13) * mm});
            skPoint(sketch, "E2.25.64.0", {"position": v(792.1, -1641.13) * mm});
            skPoint(sketch, "E2.25.65.0", {"position": v(792.1, -1666.13) * mm});
            skPoint(sketch, "E2.25.66.0", {"position": v(792.1, -1691.13) * mm});
            skPoint(sketch, "E2.25.67.0", {"position": v(792.1, -1716.13) * mm});
            skPoint(sketch, "E2.25.68.0", {"position": v(792.1, -1741.13) * mm});
            skPoint(sketch, "E2.26.0.0", {"position": v(822.1, -41.13) * mm});
            skPoint(sketch, "E2.26.1.0", {"position": v(822.1, -66.13) * mm});
            skPoint(sketch, "E2.26.2.0", {"position": v(822.1, -91.13) * mm});
            skPoint(sketch, "E2.26.3.0", {"position": v(822.1, -116.13) * mm});
            skPoint(sketch, "E2.26.4.0", {"position": v(822.1, -141.13) * mm});
            skPoint(sketch, "E2.26.5.0", {"position": v(822.1, -166.13) * mm});
            skPoint(sketch, "E2.26.6.0", {"position": v(822.1, -191.13) * mm});
            skPoint(sketch, "E2.26.7.0", {"position": v(822.1, -216.13) * mm});
            skPoint(sketch, "E2.26.8.0", {"position": v(822.1, -241.13) * mm});
            skPoint(sketch, "E2.26.9.0", {"position": v(822.1, -266.13) * mm});
            skPoint(sketch, "E2.26.10.0", {"position": v(822.1, -291.13) * mm});
            skPoint(sketch, "E2.26.11.0", {"position": v(822.1, -316.13) * mm});
            skPoint(sketch, "E2.26.12.0", {"position": v(822.1, -341.13) * mm});
            skPoint(sketch, "E2.26.13.0", {"position": v(822.1, -366.13) * mm});
            skPoint(sketch, "E2.26.14.0", {"position": v(822.1, -391.13) * mm});
            skPoint(sketch, "E2.26.15.0", {"position": v(822.1, -416.13) * mm});
            skPoint(sketch, "E2.26.16.0", {"position": v(822.1, -441.13) * mm});
            skPoint(sketch, "E2.26.17.0", {"position": v(822.1, -466.13) * mm});
            skPoint(sketch, "E2.26.18.0", {"position": v(822.1, -491.13) * mm});
            skPoint(sketch, "E2.26.19.0", {"position": v(822.1, -516.13) * mm});
            skPoint(sketch, "E2.26.20.0", {"position": v(822.1, -541.13) * mm});
            skPoint(sketch, "E2.26.21.0", {"position": v(822.1, -566.13) * mm});
            skPoint(sketch, "E2.26.22.0", {"position": v(822.1, -591.13) * mm});
            skPoint(sketch, "E2.26.23.0", {"position": v(822.1, -616.13) * mm});
            skPoint(sketch, "E2.26.24.0", {"position": v(822.1, -641.13) * mm});
            skPoint(sketch, "E2.26.25.0", {"position": v(822.1, -666.13) * mm});
            skPoint(sketch, "E2.26.26.0", {"position": v(822.1, -691.13) * mm});
            skPoint(sketch, "E2.26.27.0", {"position": v(822.1, -716.13) * mm});
            skPoint(sketch, "E2.26.28.0", {"position": v(822.1, -741.13) * mm});
            skPoint(sketch, "E2.26.29.0", {"position": v(822.1, -766.13) * mm});
            skPoint(sketch, "E2.26.30.0", {"position": v(822.1, -791.13) * mm});
            skPoint(sketch, "E2.26.31.0", {"position": v(822.1, -816.13) * mm});
            skPoint(sketch, "E2.26.32.0", {"position": v(822.1, -841.13) * mm});
            skPoint(sketch, "E2.26.33.0", {"position": v(822.1, -866.13) * mm});
            skPoint(sketch, "E2.26.34.0", {"position": v(822.1, -891.13) * mm});
            skPoint(sketch, "E2.26.35.0", {"position": v(822.1, -916.13) * mm});
            skPoint(sketch, "E2.26.36.0", {"position": v(822.1, -941.13) * mm});
            skPoint(sketch, "E2.26.37.0", {"position": v(822.1, -966.13) * mm});
            skPoint(sketch, "E2.26.38.0", {"position": v(822.1, -991.13) * mm});
            skPoint(sketch, "E2.26.39.0", {"position": v(822.1, -1016.13) * mm});
            skPoint(sketch, "E2.26.40.0", {"position": v(822.1, -1041.13) * mm});
            skPoint(sketch, "E2.26.41.0", {"position": v(822.1, -1066.13) * mm});
            skPoint(sketch, "E2.26.42.0", {"position": v(822.1, -1091.13) * mm});
            skPoint(sketch, "E2.26.43.0", {"position": v(822.1, -1116.13) * mm});
            skPoint(sketch, "E2.26.44.0", {"position": v(822.1, -1141.13) * mm});
            skPoint(sketch, "E2.26.45.0", {"position": v(822.1, -1166.13) * mm});
            skPoint(sketch, "E2.26.46.0", {"position": v(822.1, -1191.13) * mm});
            skPoint(sketch, "E2.26.47.0", {"position": v(822.1, -1216.13) * mm});
            skPoint(sketch, "E2.26.48.0", {"position": v(822.1, -1241.13) * mm});
            skPoint(sketch, "E2.26.49.0", {"position": v(822.1, -1266.13) * mm});
            skPoint(sketch, "E2.26.50.0", {"position": v(822.1, -1291.13) * mm});
            skPoint(sketch, "E2.26.51.0", {"position": v(822.1, -1316.13) * mm});
            skPoint(sketch, "E2.26.52.0", {"position": v(822.1, -1341.13) * mm});
            skPoint(sketch, "E2.26.53.0", {"position": v(822.1, -1366.13) * mm});
            skPoint(sketch, "E2.26.54.0", {"position": v(822.1, -1391.13) * mm});
            skPoint(sketch, "E2.26.55.0", {"position": v(822.1, -1416.13) * mm});
            skPoint(sketch, "E2.26.56.0", {"position": v(822.1, -1441.13) * mm});
            skPoint(sketch, "E2.26.57.0", {"position": v(822.1, -1466.13) * mm});
            skPoint(sketch, "E2.26.58.0", {"position": v(822.1, -1491.13) * mm});
            skPoint(sketch, "E2.26.59.0", {"position": v(822.1, -1516.13) * mm});
            skPoint(sketch, "E2.26.60.0", {"position": v(822.1, -1541.13) * mm});
            skPoint(sketch, "E2.26.61.0", {"position": v(822.1, -1566.13) * mm});
            skPoint(sketch, "E2.26.62.0", {"position": v(822.1, -1591.13) * mm});
            skPoint(sketch, "E2.26.63.0", {"position": v(822.1, -1616.13) * mm});
            skPoint(sketch, "E2.26.64.0", {"position": v(822.1, -1641.13) * mm});
            skPoint(sketch, "E2.26.65.0", {"position": v(822.1, -1666.13) * mm});
            skPoint(sketch, "E2.26.66.0", {"position": v(822.1, -1691.13) * mm});
            skPoint(sketch, "E2.26.67.0", {"position": v(822.1, -1716.13) * mm});
            skPoint(sketch, "E2.26.68.0", {"position": v(822.1, -1741.13) * mm});
            skPoint(sketch, "E2.27.0.0", {"position": v(852.1, -41.13) * mm});
            skPoint(sketch, "E2.27.1.0", {"position": v(852.1, -66.13) * mm});
            skPoint(sketch, "E2.27.2.0", {"position": v(852.1, -91.13) * mm});
            skPoint(sketch, "E2.27.3.0", {"position": v(852.1, -116.13) * mm});
            skPoint(sketch, "E2.27.4.0", {"position": v(852.1, -141.13) * mm});
            skPoint(sketch, "E2.27.5.0", {"position": v(852.1, -166.13) * mm});
            skPoint(sketch, "E2.27.6.0", {"position": v(852.1, -191.13) * mm});
            skPoint(sketch, "E2.27.7.0", {"position": v(852.1, -216.13) * mm});
            skPoint(sketch, "E2.27.8.0", {"position": v(852.1, -241.13) * mm});
            skPoint(sketch, "E2.27.9.0", {"position": v(852.1, -266.13) * mm});
            skPoint(sketch, "E2.27.10.0", {"position": v(852.1, -291.13) * mm});
            skPoint(sketch, "E2.27.11.0", {"position": v(852.1, -316.13) * mm});
            skPoint(sketch, "E2.27.12.0", {"position": v(852.1, -341.13) * mm});
            skPoint(sketch, "E2.27.13.0", {"position": v(852.1, -366.13) * mm});
            skPoint(sketch, "E2.27.14.0", {"position": v(852.1, -391.13) * mm});
            skPoint(sketch, "E2.27.15.0", {"position": v(852.1, -416.13) * mm});
            skPoint(sketch, "E2.27.16.0", {"position": v(852.1, -441.13) * mm});
            skPoint(sketch, "E2.27.17.0", {"position": v(852.1, -466.13) * mm});
            skPoint(sketch, "E2.27.18.0", {"position": v(852.1, -491.13) * mm});
            skPoint(sketch, "E2.27.19.0", {"position": v(852.1, -516.13) * mm});
            skPoint(sketch, "E2.27.20.0", {"position": v(852.1, -541.13) * mm});
            skPoint(sketch, "E2.27.21.0", {"position": v(852.1, -566.13) * mm});
            skPoint(sketch, "E2.27.22.0", {"position": v(852.1, -591.13) * mm});
            skPoint(sketch, "E2.27.23.0", {"position": v(852.1, -616.13) * mm});
            skPoint(sketch, "E2.27.24.0", {"position": v(852.1, -641.13) * mm});
            skPoint(sketch, "E2.27.25.0", {"position": v(852.1, -666.13) * mm});
            skPoint(sketch, "E2.27.26.0", {"position": v(852.1, -691.13) * mm});
            skPoint(sketch, "E2.27.27.0", {"position": v(852.1, -716.13) * mm});
            skPoint(sketch, "E2.27.28.0", {"position": v(852.1, -741.13) * mm});
            skPoint(sketch, "E2.27.29.0", {"position": v(852.1, -766.13) * mm});
            skPoint(sketch, "E2.27.30.0", {"position": v(852.1, -791.13) * mm});
            skPoint(sketch, "E2.27.31.0", {"position": v(852.1, -816.13) * mm});
            skPoint(sketch, "E2.27.32.0", {"position": v(852.1, -841.13) * mm});
            skPoint(sketch, "E2.27.33.0", {"position": v(852.1, -866.13) * mm});
            skPoint(sketch, "E2.27.34.0", {"position": v(852.1, -891.13) * mm});
            skPoint(sketch, "E2.27.35.0", {"position": v(852.1, -916.13) * mm});
            skPoint(sketch, "E2.27.36.0", {"position": v(852.1, -941.13) * mm});
            skPoint(sketch, "E2.27.37.0", {"position": v(852.1, -966.13) * mm});
            skPoint(sketch, "E2.27.38.0", {"position": v(852.1, -991.13) * mm});
            skPoint(sketch, "E2.27.39.0", {"position": v(852.1, -1016.13) * mm});
            skPoint(sketch, "E2.27.40.0", {"position": v(852.1, -1041.13) * mm});
            skPoint(sketch, "E2.27.41.0", {"position": v(852.1, -1066.13) * mm});
            skPoint(sketch, "E2.27.42.0", {"position": v(852.1, -1091.13) * mm});
            skPoint(sketch, "E2.27.43.0", {"position": v(852.1, -1116.13) * mm});
            skPoint(sketch, "E2.27.44.0", {"position": v(852.1, -1141.13) * mm});
            skPoint(sketch, "E2.27.45.0", {"position": v(852.1, -1166.13) * mm});
            skPoint(sketch, "E2.27.46.0", {"position": v(852.1, -1191.13) * mm});
            skPoint(sketch, "E2.27.47.0", {"position": v(852.1, -1216.13) * mm});
            skPoint(sketch, "E2.27.48.0", {"position": v(852.1, -1241.13) * mm});
            skPoint(sketch, "E2.27.49.0", {"position": v(852.1, -1266.13) * mm});
            skPoint(sketch, "E2.27.50.0", {"position": v(852.1, -1291.13) * mm});
            skPoint(sketch, "E2.27.51.0", {"position": v(852.1, -1316.13) * mm});
            skPoint(sketch, "E2.27.52.0", {"position": v(852.1, -1341.13) * mm});
            skPoint(sketch, "E2.27.53.0", {"position": v(852.1, -1366.13) * mm});
            skPoint(sketch, "E2.27.54.0", {"position": v(852.1, -1391.13) * mm});
            skPoint(sketch, "E2.27.55.0", {"position": v(852.1, -1416.13) * mm});
            skPoint(sketch, "E2.27.56.0", {"position": v(852.1, -1441.13) * mm});
            skPoint(sketch, "E2.27.57.0", {"position": v(852.1, -1466.13) * mm});
            skPoint(sketch, "E2.27.58.0", {"position": v(852.1, -1491.13) * mm});
            skPoint(sketch, "E2.27.59.0", {"position": v(852.1, -1516.13) * mm});
            skPoint(sketch, "E2.27.60.0", {"position": v(852.1, -1541.13) * mm});
            skPoint(sketch, "E2.27.61.0", {"position": v(852.1, -1566.13) * mm});
            skPoint(sketch, "E2.27.62.0", {"position": v(852.1, -1591.13) * mm});
            skPoint(sketch, "E2.27.63.0", {"position": v(852.1, -1616.13) * mm});
            skPoint(sketch, "E2.27.64.0", {"position": v(852.1, -1641.13) * mm});
            skPoint(sketch, "E2.27.65.0", {"position": v(852.1, -1666.13) * mm});
            skPoint(sketch, "E2.27.66.0", {"position": v(852.1, -1691.13) * mm});
            skPoint(sketch, "E2.27.67.0", {"position": v(852.1, -1716.13) * mm});
            skPoint(sketch, "E2.27.68.0", {"position": v(852.1, -1741.13) * mm});
            skPoint(sketch, "E2.28.0.0", {"position": v(882.1, -41.13) * mm});
            skPoint(sketch, "E2.28.1.0", {"position": v(882.1, -66.13) * mm});
            skPoint(sketch, "E2.28.2.0", {"position": v(882.1, -91.13) * mm});
            skPoint(sketch, "E2.28.3.0", {"position": v(882.1, -116.13) * mm});
            skPoint(sketch, "E2.28.4.0", {"position": v(882.1, -141.13) * mm});
            skPoint(sketch, "E2.28.5.0", {"position": v(882.1, -166.13) * mm});
            skPoint(sketch, "E2.28.6.0", {"position": v(882.1, -191.13) * mm});
            skPoint(sketch, "E2.28.7.0", {"position": v(882.1, -216.13) * mm});
            skPoint(sketch, "E2.28.8.0", {"position": v(882.1, -241.13) * mm});
            skPoint(sketch, "E2.28.9.0", {"position": v(882.1, -266.13) * mm});
            skPoint(sketch, "E2.28.10.0", {"position": v(882.1, -291.13) * mm});
            skPoint(sketch, "E2.28.11.0", {"position": v(882.1, -316.13) * mm});
            skPoint(sketch, "E2.28.12.0", {"position": v(882.1, -341.13) * mm});
            skPoint(sketch, "E2.28.13.0", {"position": v(882.1, -366.13) * mm});
            skPoint(sketch, "E2.28.14.0", {"position": v(882.1, -391.13) * mm});
            skPoint(sketch, "E2.28.15.0", {"position": v(882.1, -416.13) * mm});
            skPoint(sketch, "E2.28.16.0", {"position": v(882.1, -441.13) * mm});
            skPoint(sketch, "E2.28.17.0", {"position": v(882.1, -466.13) * mm});
            skPoint(sketch, "E2.28.18.0", {"position": v(882.1, -491.13) * mm});
            skPoint(sketch, "E2.28.19.0", {"position": v(882.1, -516.13) * mm});
            skPoint(sketch, "E2.28.20.0", {"position": v(882.1, -541.13) * mm});
            skPoint(sketch, "E2.28.21.0", {"position": v(882.1, -566.13) * mm});
            skPoint(sketch, "E2.28.22.0", {"position": v(882.1, -591.13) * mm});
            skPoint(sketch, "E2.28.23.0", {"position": v(882.1, -616.13) * mm});
            skPoint(sketch, "E2.28.24.0", {"position": v(882.1, -641.13) * mm});
            skPoint(sketch, "E2.28.25.0", {"position": v(882.1, -666.13) * mm});
            skPoint(sketch, "E2.28.26.0", {"position": v(882.1, -691.13) * mm});
            skPoint(sketch, "E2.28.27.0", {"position": v(882.1, -716.13) * mm});
            skPoint(sketch, "E2.28.28.0", {"position": v(882.1, -741.13) * mm});
            skPoint(sketch, "E2.28.29.0", {"position": v(882.1, -766.13) * mm});
            skPoint(sketch, "E2.28.30.0", {"position": v(882.1, -791.13) * mm});
            skPoint(sketch, "E2.28.31.0", {"position": v(882.1, -816.13) * mm});
            skPoint(sketch, "E2.28.32.0", {"position": v(882.1, -841.13) * mm});
            skPoint(sketch, "E2.28.33.0", {"position": v(882.1, -866.13) * mm});
            skPoint(sketch, "E2.28.34.0", {"position": v(882.1, -891.13) * mm});
            skPoint(sketch, "E2.28.35.0", {"position": v(882.1, -916.13) * mm});
            skPoint(sketch, "E2.28.36.0", {"position": v(882.1, -941.13) * mm});
            skPoint(sketch, "E2.28.37.0", {"position": v(882.1, -966.13) * mm});
            skPoint(sketch, "E2.28.38.0", {"position": v(882.1, -991.13) * mm});
            skPoint(sketch, "E2.28.39.0", {"position": v(882.1, -1016.13) * mm});
            skPoint(sketch, "E2.28.40.0", {"position": v(882.1, -1041.13) * mm});
            skPoint(sketch, "E2.28.41.0", {"position": v(882.1, -1066.13) * mm});
            skPoint(sketch, "E2.28.42.0", {"position": v(882.1, -1091.13) * mm});
            skPoint(sketch, "E2.28.43.0", {"position": v(882.1, -1116.13) * mm});
            skPoint(sketch, "E2.28.44.0", {"position": v(882.1, -1141.13) * mm});
            skPoint(sketch, "E2.28.45.0", {"position": v(882.1, -1166.13) * mm});
            skPoint(sketch, "E2.28.46.0", {"position": v(882.1, -1191.13) * mm});
            skPoint(sketch, "E2.28.47.0", {"position": v(882.1, -1216.13) * mm});
            skPoint(sketch, "E2.28.48.0", {"position": v(882.1, -1241.13) * mm});
            skPoint(sketch, "E2.28.49.0", {"position": v(882.1, -1266.13) * mm});
            skPoint(sketch, "E2.28.50.0", {"position": v(882.1, -1291.13) * mm});
            skPoint(sketch, "E2.28.51.0", {"position": v(882.1, -1316.13) * mm});
            skPoint(sketch, "E2.28.52.0", {"position": v(882.1, -1341.13) * mm});
            skPoint(sketch, "E2.28.53.0", {"position": v(882.1, -1366.13) * mm});
            skPoint(sketch, "E2.28.54.0", {"position": v(882.1, -1391.13) * mm});
            skPoint(sketch, "E2.28.55.0", {"position": v(882.1, -1416.13) * mm});
            skPoint(sketch, "E2.28.56.0", {"position": v(882.1, -1441.13) * mm});
            skPoint(sketch, "E2.28.57.0", {"position": v(882.1, -1466.13) * mm});
            skPoint(sketch, "E2.28.58.0", {"position": v(882.1, -1491.13) * mm});
            skPoint(sketch, "E2.28.59.0", {"position": v(882.1, -1516.13) * mm});
            skPoint(sketch, "E2.28.60.0", {"position": v(882.1, -1541.13) * mm});
            skPoint(sketch, "E2.28.61.0", {"position": v(882.1, -1566.13) * mm});
            skPoint(sketch, "E2.28.62.0", {"position": v(882.1, -1591.13) * mm});
            skPoint(sketch, "E2.28.63.0", {"position": v(882.1, -1616.13) * mm});
            skPoint(sketch, "E2.28.64.0", {"position": v(882.1, -1641.13) * mm});
            skPoint(sketch, "E2.28.65.0", {"position": v(882.1, -1666.13) * mm});
            skPoint(sketch, "E2.28.66.0", {"position": v(882.1, -1691.13) * mm});
            skPoint(sketch, "E2.28.67.0", {"position": v(882.1, -1716.13) * mm});
            skPoint(sketch, "E2.28.68.0", {"position": v(882.1, -1741.13) * mm});
            skPoint(sketch, "E2.29.0.0", {"position": v(912.1, -41.13) * mm});
            skPoint(sketch, "E2.29.1.0", {"position": v(912.1, -66.13) * mm});
            skPoint(sketch, "E2.29.2.0", {"position": v(912.1, -91.13) * mm});
            skPoint(sketch, "E2.29.3.0", {"position": v(912.1, -116.13) * mm});
            skPoint(sketch, "E2.29.4.0", {"position": v(912.1, -141.13) * mm});
            skPoint(sketch, "E2.29.5.0", {"position": v(912.1, -166.13) * mm});
            skPoint(sketch, "E2.29.6.0", {"position": v(912.1, -191.13) * mm});
            skPoint(sketch, "E2.29.7.0", {"position": v(912.1, -216.13) * mm});
            skPoint(sketch, "E2.29.8.0", {"position": v(912.1, -241.13) * mm});
            skPoint(sketch, "E2.29.9.0", {"position": v(912.1, -266.13) * mm});
            skPoint(sketch, "E2.29.10.0", {"position": v(912.1, -291.13) * mm});
            skPoint(sketch, "E2.29.11.0", {"position": v(912.1, -316.13) * mm});
            skPoint(sketch, "E2.29.12.0", {"position": v(912.1, -341.13) * mm});
            skPoint(sketch, "E2.29.13.0", {"position": v(912.1, -366.13) * mm});
            skPoint(sketch, "E2.29.14.0", {"position": v(912.1, -391.13) * mm});
            skPoint(sketch, "E2.29.15.0", {"position": v(912.1, -416.13) * mm});
            skPoint(sketch, "E2.29.16.0", {"position": v(912.1, -441.13) * mm});
            skPoint(sketch, "E2.29.17.0", {"position": v(912.1, -466.13) * mm});
            skPoint(sketch, "E2.29.18.0", {"position": v(912.1, -491.13) * mm});
            skPoint(sketch, "E2.29.19.0", {"position": v(912.1, -516.13) * mm});
            skPoint(sketch, "E2.29.20.0", {"position": v(912.1, -541.13) * mm});
            skPoint(sketch, "E2.29.21.0", {"position": v(912.1, -566.13) * mm});
            skPoint(sketch, "E2.29.22.0", {"position": v(912.1, -591.13) * mm});
            skPoint(sketch, "E2.29.23.0", {"position": v(912.1, -616.13) * mm});
            skPoint(sketch, "E2.29.24.0", {"position": v(912.1, -641.13) * mm});
            skPoint(sketch, "E2.29.25.0", {"position": v(912.1, -666.13) * mm});
            skPoint(sketch, "E2.29.26.0", {"position": v(912.1, -691.13) * mm});
            skPoint(sketch, "E2.29.27.0", {"position": v(912.1, -716.13) * mm});
            skPoint(sketch, "E2.29.28.0", {"position": v(912.1, -741.13) * mm});
            skPoint(sketch, "E2.29.29.0", {"position": v(912.1, -766.13) * mm});
            skPoint(sketch, "E2.29.30.0", {"position": v(912.1, -791.13) * mm});
            skPoint(sketch, "E2.29.31.0", {"position": v(912.1, -816.13) * mm});
            skPoint(sketch, "E2.29.32.0", {"position": v(912.1, -841.13) * mm});
            skPoint(sketch, "E2.29.33.0", {"position": v(912.1, -866.13) * mm});
            skPoint(sketch, "E2.29.34.0", {"position": v(912.1, -891.13) * mm});
            skPoint(sketch, "E2.29.35.0", {"position": v(912.1, -916.13) * mm});
            skPoint(sketch, "E2.29.36.0", {"position": v(912.1, -941.13) * mm});
            skPoint(sketch, "E2.29.37.0", {"position": v(912.1, -966.13) * mm});
            skPoint(sketch, "E2.29.38.0", {"position": v(912.1, -991.13) * mm});
            skPoint(sketch, "E2.29.39.0", {"position": v(912.1, -1016.13) * mm});
            skPoint(sketch, "E2.29.40.0", {"position": v(912.1, -1041.13) * mm});
            skPoint(sketch, "E2.29.41.0", {"position": v(912.1, -1066.13) * mm});
            skPoint(sketch, "E2.29.42.0", {"position": v(912.1, -1091.13) * mm});
            skPoint(sketch, "E2.29.43.0", {"position": v(912.1, -1116.13) * mm});
            skPoint(sketch, "E2.29.44.0", {"position": v(912.1, -1141.13) * mm});
            skPoint(sketch, "E2.29.45.0", {"position": v(912.1, -1166.13) * mm});
            skPoint(sketch, "E2.29.46.0", {"position": v(912.1, -1191.13) * mm});
            skPoint(sketch, "E2.29.47.0", {"position": v(912.1, -1216.13) * mm});
            skPoint(sketch, "E2.29.48.0", {"position": v(912.1, -1241.13) * mm});
            skPoint(sketch, "E2.29.49.0", {"position": v(912.1, -1266.13) * mm});
            skPoint(sketch, "E2.29.50.0", {"position": v(912.1, -1291.13) * mm});
            skPoint(sketch, "E2.29.51.0", {"position": v(912.1, -1316.13) * mm});
            skPoint(sketch, "E2.29.52.0", {"position": v(912.1, -1341.13) * mm});
            skPoint(sketch, "E2.29.53.0", {"position": v(912.1, -1366.13) * mm});
            skPoint(sketch, "E2.29.54.0", {"position": v(912.1, -1391.13) * mm});
            skPoint(sketch, "E2.29.55.0", {"position": v(912.1, -1416.13) * mm});
            skPoint(sketch, "E2.29.56.0", {"position": v(912.1, -1441.13) * mm});
            skPoint(sketch, "E2.29.57.0", {"position": v(912.1, -1466.13) * mm});
            skPoint(sketch, "E2.29.58.0", {"position": v(912.1, -1491.13) * mm});
            skPoint(sketch, "E2.29.59.0", {"position": v(912.1, -1516.13) * mm});
            skPoint(sketch, "E2.29.60.0", {"position": v(912.1, -1541.13) * mm});
            skPoint(sketch, "E2.29.61.0", {"position": v(912.1, -1566.13) * mm});
            skPoint(sketch, "E2.29.62.0", {"position": v(912.1, -1591.13) * mm});
            skPoint(sketch, "E2.29.63.0", {"position": v(912.1, -1616.13) * mm});
            skPoint(sketch, "E2.29.64.0", {"position": v(912.1, -1641.13) * mm});
            skPoint(sketch, "E2.29.65.0", {"position": v(912.1, -1666.13) * mm});
            skPoint(sketch, "E2.29.66.0", {"position": v(912.1, -1691.13) * mm});
            skPoint(sketch, "E2.29.67.0", {"position": v(912.1, -1716.13) * mm});
            skPoint(sketch, "E2.29.68.0", {"position": v(912.1, -1741.13) * mm});
            skPoint(sketch, "E2.30.0.0", {"position": v(942.1, -41.13) * mm});
            skPoint(sketch, "E2.30.1.0", {"position": v(942.1, -66.13) * mm});
            skPoint(sketch, "E2.30.2.0", {"position": v(942.1, -91.13) * mm});
            skPoint(sketch, "E2.30.3.0", {"position": v(942.1, -116.13) * mm});
            skPoint(sketch, "E2.30.4.0", {"position": v(942.1, -141.13) * mm});
            skPoint(sketch, "E2.30.5.0", {"position": v(942.1, -166.13) * mm});
            skPoint(sketch, "E2.30.6.0", {"position": v(942.1, -191.13) * mm});
            skPoint(sketch, "E2.30.7.0", {"position": v(942.1, -216.13) * mm});
            skPoint(sketch, "E2.30.8.0", {"position": v(942.1, -241.13) * mm});
            skPoint(sketch, "E2.30.9.0", {"position": v(942.1, -266.13) * mm});
            skPoint(sketch, "E2.30.10.0", {"position": v(942.1, -291.13) * mm});
            skPoint(sketch, "E2.30.11.0", {"position": v(942.1, -316.13) * mm});
            skPoint(sketch, "E2.30.12.0", {"position": v(942.1, -341.13) * mm});
            skPoint(sketch, "E2.30.13.0", {"position": v(942.1, -366.13) * mm});
            skPoint(sketch, "E2.30.14.0", {"position": v(942.1, -391.13) * mm});
            skPoint(sketch, "E2.30.15.0", {"position": v(942.1, -416.13) * mm});
            skPoint(sketch, "E2.30.16.0", {"position": v(942.1, -441.13) * mm});
            skPoint(sketch, "E2.30.17.0", {"position": v(942.1, -466.13) * mm});
            skPoint(sketch, "E2.30.18.0", {"position": v(942.1, -491.13) * mm});
            skPoint(sketch, "E2.30.19.0", {"position": v(942.1, -516.13) * mm});
            skPoint(sketch, "E2.30.20.0", {"position": v(942.1, -541.13) * mm});
            skPoint(sketch, "E2.30.21.0", {"position": v(942.1, -566.13) * mm});
            skPoint(sketch, "E2.30.22.0", {"position": v(942.1, -591.13) * mm});
            skPoint(sketch, "E2.30.23.0", {"position": v(942.1, -616.13) * mm});
            skPoint(sketch, "E2.30.24.0", {"position": v(942.1, -641.13) * mm});
            skPoint(sketch, "E2.30.25.0", {"position": v(942.1, -666.13) * mm});
            skPoint(sketch, "E2.30.26.0", {"position": v(942.1, -691.13) * mm});
            skPoint(sketch, "E2.30.27.0", {"position": v(942.1, -716.13) * mm});
            skPoint(sketch, "E2.30.28.0", {"position": v(942.1, -741.13) * mm});
            skPoint(sketch, "E2.30.29.0", {"position": v(942.1, -766.13) * mm});
            skPoint(sketch, "E2.30.30.0", {"position": v(942.1, -791.13) * mm});
            skPoint(sketch, "E2.30.31.0", {"position": v(942.1, -816.13) * mm});
            skPoint(sketch, "E2.30.32.0", {"position": v(942.1, -841.13) * mm});
            skPoint(sketch, "E2.30.33.0", {"position": v(942.1, -866.13) * mm});
            skPoint(sketch, "E2.30.34.0", {"position": v(942.1, -891.13) * mm});
            skPoint(sketch, "E2.30.35.0", {"position": v(942.1, -916.13) * mm});
            skPoint(sketch, "E2.30.36.0", {"position": v(942.1, -941.13) * mm});
            skPoint(sketch, "E2.30.37.0", {"position": v(942.1, -966.13) * mm});
            skPoint(sketch, "E2.30.38.0", {"position": v(942.1, -991.13) * mm});
            skPoint(sketch, "E2.30.39.0", {"position": v(942.1, -1016.13) * mm});
            skPoint(sketch, "E2.30.40.0", {"position": v(942.1, -1041.13) * mm});
            skPoint(sketch, "E2.30.41.0", {"position": v(942.1, -1066.13) * mm});
            skPoint(sketch, "E2.30.42.0", {"position": v(942.1, -1091.13) * mm});
            skPoint(sketch, "E2.30.43.0", {"position": v(942.1, -1116.13) * mm});
            skPoint(sketch, "E2.30.44.0", {"position": v(942.1, -1141.13) * mm});
            skPoint(sketch, "E2.30.45.0", {"position": v(942.1, -1166.13) * mm});
            skPoint(sketch, "E2.30.46.0", {"position": v(942.1, -1191.13) * mm});
            skPoint(sketch, "E2.30.47.0", {"position": v(942.1, -1216.13) * mm});
            skPoint(sketch, "E2.30.48.0", {"position": v(942.1, -1241.13) * mm});
            skPoint(sketch, "E2.30.49.0", {"position": v(942.1, -1266.13) * mm});
            skPoint(sketch, "E2.30.50.0", {"position": v(942.1, -1291.13) * mm});
            skPoint(sketch, "E2.30.51.0", {"position": v(942.1, -1316.13) * mm});
            skPoint(sketch, "E2.30.52.0", {"position": v(942.1, -1341.13) * mm});
            skPoint(sketch, "E2.30.53.0", {"position": v(942.1, -1366.13) * mm});
            skPoint(sketch, "E2.30.54.0", {"position": v(942.1, -1391.13) * mm});
            skPoint(sketch, "E2.30.55.0", {"position": v(942.1, -1416.13) * mm});
            skPoint(sketch, "E2.30.56.0", {"position": v(942.1, -1441.13) * mm});
            skPoint(sketch, "E2.30.57.0", {"position": v(942.1, -1466.13) * mm});
            skPoint(sketch, "E2.30.58.0", {"position": v(942.1, -1491.13) * mm});
            skPoint(sketch, "E2.30.59.0", {"position": v(942.1, -1516.13) * mm});
            skPoint(sketch, "E2.30.60.0", {"position": v(942.1, -1541.13) * mm});
            skPoint(sketch, "E2.30.61.0", {"position": v(942.1, -1566.13) * mm});
            skPoint(sketch, "E2.30.62.0", {"position": v(942.1, -1591.13) * mm});
            skPoint(sketch, "E2.30.63.0", {"position": v(942.1, -1616.13) * mm});
            skPoint(sketch, "E2.30.64.0", {"position": v(942.1, -1641.13) * mm});
            skPoint(sketch, "E2.30.65.0", {"position": v(942.1, -1666.13) * mm});
            skPoint(sketch, "E2.30.66.0", {"position": v(942.1, -1691.13) * mm});
            skPoint(sketch, "E2.30.67.0", {"position": v(942.1, -1716.13) * mm});
            skPoint(sketch, "E2.30.68.0", {"position": v(942.1, -1741.13) * mm});
            skPoint(sketch, "E2.31.0.0", {"position": v(972.1, -41.13) * mm});
            skPoint(sketch, "E2.31.1.0", {"position": v(972.1, -66.13) * mm});
            skPoint(sketch, "E2.31.2.0", {"position": v(972.1, -91.13) * mm});
            skPoint(sketch, "E2.31.3.0", {"position": v(972.1, -116.13) * mm});
            skPoint(sketch, "E2.31.4.0", {"position": v(972.1, -141.13) * mm});
            skPoint(sketch, "E2.31.5.0", {"position": v(972.1, -166.13) * mm});
            skPoint(sketch, "E2.31.6.0", {"position": v(972.1, -191.13) * mm});
            skPoint(sketch, "E2.31.7.0", {"position": v(972.1, -216.13) * mm});
            skPoint(sketch, "E2.31.8.0", {"position": v(972.1, -241.13) * mm});
            skPoint(sketch, "E2.31.9.0", {"position": v(972.1, -266.13) * mm});
            skPoint(sketch, "E2.31.10.0", {"position": v(972.1, -291.13) * mm});
            skPoint(sketch, "E2.31.11.0", {"position": v(972.1, -316.13) * mm});
            skPoint(sketch, "E2.31.12.0", {"position": v(972.1, -341.13) * mm});
            skPoint(sketch, "E2.31.13.0", {"position": v(972.1, -366.13) * mm});
            skPoint(sketch, "E2.31.14.0", {"position": v(972.1, -391.13) * mm});
            skPoint(sketch, "E2.31.15.0", {"position": v(972.1, -416.13) * mm});
            skPoint(sketch, "E2.31.16.0", {"position": v(972.1, -441.13) * mm});
            skPoint(sketch, "E2.31.17.0", {"position": v(972.1, -466.13) * mm});
            skPoint(sketch, "E2.31.18.0", {"position": v(972.1, -491.13) * mm});
            skPoint(sketch, "E2.31.19.0", {"position": v(972.1, -516.13) * mm});
            skPoint(sketch, "E2.31.20.0", {"position": v(972.1, -541.13) * mm});
            skPoint(sketch, "E2.31.21.0", {"position": v(972.1, -566.13) * mm});
            skPoint(sketch, "E2.31.22.0", {"position": v(972.1, -591.13) * mm});
            skPoint(sketch, "E2.31.23.0", {"position": v(972.1, -616.13) * mm});
            skPoint(sketch, "E2.31.24.0", {"position": v(972.1, -641.13) * mm});
            skPoint(sketch, "E2.31.25.0", {"position": v(972.1, -666.13) * mm});
            skPoint(sketch, "E2.31.26.0", {"position": v(972.1, -691.13) * mm});
            skPoint(sketch, "E2.31.27.0", {"position": v(972.1, -716.13) * mm});
            skPoint(sketch, "E2.31.28.0", {"position": v(972.1, -741.13) * mm});
            skPoint(sketch, "E2.31.29.0", {"position": v(972.1, -766.13) * mm});
            skPoint(sketch, "E2.31.30.0", {"position": v(972.1, -791.13) * mm});
            skPoint(sketch, "E2.31.31.0", {"position": v(972.1, -816.13) * mm});
            skPoint(sketch, "E2.31.32.0", {"position": v(972.1, -841.13) * mm});
            skPoint(sketch, "E2.31.33.0", {"position": v(972.1, -866.13) * mm});
            skPoint(sketch, "E2.31.34.0", {"position": v(972.1, -891.13) * mm});
            skPoint(sketch, "E2.31.35.0", {"position": v(972.1, -916.13) * mm});
            skPoint(sketch, "E2.31.36.0", {"position": v(972.1, -941.13) * mm});
            skPoint(sketch, "E2.31.37.0", {"position": v(972.1, -966.13) * mm});
            skPoint(sketch, "E2.31.38.0", {"position": v(972.1, -991.13) * mm});
            skPoint(sketch, "E2.31.39.0", {"position": v(972.1, -1016.13) * mm});
            skPoint(sketch, "E2.31.40.0", {"position": v(972.1, -1041.13) * mm});
            skPoint(sketch, "E2.31.41.0", {"position": v(972.1, -1066.13) * mm});
            skPoint(sketch, "E2.31.42.0", {"position": v(972.1, -1091.13) * mm});
            skPoint(sketch, "E2.31.43.0", {"position": v(972.1, -1116.13) * mm});
            skPoint(sketch, "E2.31.44.0", {"position": v(972.1, -1141.13) * mm});
            skPoint(sketch, "E2.31.45.0", {"position": v(972.1, -1166.13) * mm});
            skPoint(sketch, "E2.31.46.0", {"position": v(972.1, -1191.13) * mm});
            skPoint(sketch, "E2.31.47.0", {"position": v(972.1, -1216.13) * mm});
            skPoint(sketch, "E2.31.48.0", {"position": v(972.1, -1241.13) * mm});
            skPoint(sketch, "E2.31.49.0", {"position": v(972.1, -1266.13) * mm});
            skPoint(sketch, "E2.31.50.0", {"position": v(972.1, -1291.13) * mm});
            skPoint(sketch, "E2.31.51.0", {"position": v(972.1, -1316.13) * mm});
            skPoint(sketch, "E2.31.52.0", {"position": v(972.1, -1341.13) * mm});
            skPoint(sketch, "E2.31.53.0", {"position": v(972.1, -1366.13) * mm});
            skPoint(sketch, "E2.31.54.0", {"position": v(972.1, -1391.13) * mm});
            skPoint(sketch, "E2.31.55.0", {"position": v(972.1, -1416.13) * mm});
            skPoint(sketch, "E2.31.56.0", {"position": v(972.1, -1441.13) * mm});
            skPoint(sketch, "E2.31.57.0", {"position": v(972.1, -1466.13) * mm});
            skPoint(sketch, "E2.31.58.0", {"position": v(972.1, -1491.13) * mm});
            skPoint(sketch, "E2.31.59.0", {"position": v(972.1, -1516.13) * mm});
            skPoint(sketch, "E2.31.60.0", {"position": v(972.1, -1541.13) * mm});
            skPoint(sketch, "E2.31.61.0", {"position": v(972.1, -1566.13) * mm});
            skPoint(sketch, "E2.31.62.0", {"position": v(972.1, -1591.13) * mm});
            skPoint(sketch, "E2.31.63.0", {"position": v(972.1, -1616.13) * mm});
            skPoint(sketch, "E2.31.64.0", {"position": v(972.1, -1641.13) * mm});
            skPoint(sketch, "E2.31.65.0", {"position": v(972.1, -1666.13) * mm});
            skPoint(sketch, "E2.31.66.0", {"position": v(972.1, -1691.13) * mm});
            skPoint(sketch, "E2.31.67.0", {"position": v(972.1, -1716.13) * mm});
            skPoint(sketch, "E2.31.68.0", {"position": v(972.1, -1741.13) * mm});
            skPoint(sketch, "E2.32.0.0", {"position": v(1002.1, -41.13) * mm});
            skPoint(sketch, "E2.32.1.0", {"position": v(1002.1, -66.13) * mm});
            skPoint(sketch, "E2.32.2.0", {"position": v(1002.1, -91.13) * mm});
            skPoint(sketch, "E2.32.3.0", {"position": v(1002.1, -116.13) * mm});
            skPoint(sketch, "E2.32.4.0", {"position": v(1002.1, -141.13) * mm});
            skPoint(sketch, "E2.32.5.0", {"position": v(1002.1, -166.13) * mm});
            skPoint(sketch, "E2.32.6.0", {"position": v(1002.1, -191.13) * mm});
            skPoint(sketch, "E2.32.7.0", {"position": v(1002.1, -216.13) * mm});
            skPoint(sketch, "E2.32.8.0", {"position": v(1002.1, -241.13) * mm});
            skPoint(sketch, "E2.32.9.0", {"position": v(1002.1, -266.13) * mm});
            skPoint(sketch, "E2.32.10.0", {"position": v(1002.1, -291.13) * mm});
            skPoint(sketch, "E2.32.11.0", {"position": v(1002.1, -316.13) * mm});
            skPoint(sketch, "E2.32.12.0", {"position": v(1002.1, -341.13) * mm});
            skPoint(sketch, "E2.32.13.0", {"position": v(1002.1, -366.13) * mm});
            skPoint(sketch, "E2.32.14.0", {"position": v(1002.1, -391.13) * mm});
            skPoint(sketch, "E2.32.15.0", {"position": v(1002.1, -416.13) * mm});
            skPoint(sketch, "E2.32.16.0", {"position": v(1002.1, -441.13) * mm});
            skPoint(sketch, "E2.32.17.0", {"position": v(1002.1, -466.13) * mm});
            skPoint(sketch, "E2.32.18.0", {"position": v(1002.1, -491.13) * mm});
            skPoint(sketch, "E2.32.19.0", {"position": v(1002.1, -516.13) * mm});
            skPoint(sketch, "E2.32.20.0", {"position": v(1002.1, -541.13) * mm});
            skPoint(sketch, "E2.32.21.0", {"position": v(1002.1, -566.13) * mm});
            skPoint(sketch, "E2.32.22.0", {"position": v(1002.1, -591.13) * mm});
            skPoint(sketch, "E2.32.23.0", {"position": v(1002.1, -616.13) * mm});
            skPoint(sketch, "E2.32.24.0", {"position": v(1002.1, -641.13) * mm});
            skPoint(sketch, "E2.32.25.0", {"position": v(1002.1, -666.13) * mm});
            skPoint(sketch, "E2.32.26.0", {"position": v(1002.1, -691.13) * mm});
            skPoint(sketch, "E2.32.27.0", {"position": v(1002.1, -716.13) * mm});
            skPoint(sketch, "E2.32.28.0", {"position": v(1002.1, -741.13) * mm});
            skPoint(sketch, "E2.32.29.0", {"position": v(1002.1, -766.13) * mm});
            skPoint(sketch, "E2.32.30.0", {"position": v(1002.1, -791.13) * mm});
            skPoint(sketch, "E2.32.31.0", {"position": v(1002.1, -816.13) * mm});
            skPoint(sketch, "E2.32.32.0", {"position": v(1002.1, -841.13) * mm});
            skPoint(sketch, "E2.32.33.0", {"position": v(1002.1, -866.13) * mm});
            skPoint(sketch, "E2.32.34.0", {"position": v(1002.1, -891.13) * mm});
            skPoint(sketch, "E2.32.35.0", {"position": v(1002.1, -916.13) * mm});
            skPoint(sketch, "E2.32.36.0", {"position": v(1002.1, -941.13) * mm});
            skPoint(sketch, "E2.32.37.0", {"position": v(1002.1, -966.13) * mm});
            skPoint(sketch, "E2.32.38.0", {"position": v(1002.1, -991.13) * mm});
            skPoint(sketch, "E2.32.39.0", {"position": v(1002.1, -1016.13) * mm});
            skPoint(sketch, "E2.32.40.0", {"position": v(1002.1, -1041.13) * mm});
            skPoint(sketch, "E2.32.41.0", {"position": v(1002.1, -1066.13) * mm});
            skPoint(sketch, "E2.32.42.0", {"position": v(1002.1, -1091.13) * mm});
            skPoint(sketch, "E2.32.43.0", {"position": v(1002.1, -1116.13) * mm});
            skPoint(sketch, "E2.32.44.0", {"position": v(1002.1, -1141.13) * mm});
            skPoint(sketch, "E2.32.45.0", {"position": v(1002.1, -1166.13) * mm});
            skPoint(sketch, "E2.32.46.0", {"position": v(1002.1, -1191.13) * mm});
            skPoint(sketch, "E2.32.47.0", {"position": v(1002.1, -1216.13) * mm});
            skPoint(sketch, "E2.32.48.0", {"position": v(1002.1, -1241.13) * mm});
            skPoint(sketch, "E2.32.49.0", {"position": v(1002.1, -1266.13) * mm});
            skPoint(sketch, "E2.32.50.0", {"position": v(1002.1, -1291.13) * mm});
            skPoint(sketch, "E2.32.51.0", {"position": v(1002.1, -1316.13) * mm});
            skPoint(sketch, "E2.32.52.0", {"position": v(1002.1, -1341.13) * mm});
            skPoint(sketch, "E2.32.53.0", {"position": v(1002.1, -1366.13) * mm});
            skPoint(sketch, "E2.32.54.0", {"position": v(1002.1, -1391.13) * mm});
            skPoint(sketch, "E2.32.55.0", {"position": v(1002.1, -1416.13) * mm});
            skPoint(sketch, "E2.32.56.0", {"position": v(1002.1, -1441.13) * mm});
            skPoint(sketch, "E2.32.57.0", {"position": v(1002.1, -1466.13) * mm});
            skPoint(sketch, "E2.32.58.0", {"position": v(1002.1, -1491.13) * mm});
            skPoint(sketch, "E2.32.59.0", {"position": v(1002.1, -1516.13) * mm});
            skPoint(sketch, "E2.32.60.0", {"position": v(1002.1, -1541.13) * mm});
            skPoint(sketch, "E2.32.61.0", {"position": v(1002.1, -1566.13) * mm});
            skPoint(sketch, "E2.32.62.0", {"position": v(1002.1, -1591.13) * mm});
            skPoint(sketch, "E2.32.63.0", {"position": v(1002.1, -1616.13) * mm});
            skPoint(sketch, "E2.32.64.0", {"position": v(1002.1, -1641.13) * mm});
            skPoint(sketch, "E2.32.65.0", {"position": v(1002.1, -1666.13) * mm});
            skPoint(sketch, "E2.32.66.0", {"position": v(1002.1, -1691.13) * mm});
            skPoint(sketch, "E2.32.67.0", {"position": v(1002.1, -1716.13) * mm});
            skPoint(sketch, "E2.32.68.0", {"position": v(1002.1, -1741.13) * mm});
            skPoint(sketch, "E2.33.0.0", {"position": v(1032.1, -41.13) * mm});
            skPoint(sketch, "E2.33.1.0", {"position": v(1032.1, -66.13) * mm});
            skPoint(sketch, "E2.33.2.0", {"position": v(1032.1, -91.13) * mm});
            skPoint(sketch, "E2.33.3.0", {"position": v(1032.1, -116.13) * mm});
            skPoint(sketch, "E2.33.4.0", {"position": v(1032.1, -141.13) * mm});
            skPoint(sketch, "E2.33.5.0", {"position": v(1032.1, -166.13) * mm});
            skPoint(sketch, "E2.33.6.0", {"position": v(1032.1, -191.13) * mm});
            skPoint(sketch, "E2.33.7.0", {"position": v(1032.1, -216.13) * mm});
            skPoint(sketch, "E2.33.8.0", {"position": v(1032.1, -241.13) * mm});
            skPoint(sketch, "E2.33.9.0", {"position": v(1032.1, -266.13) * mm});
            skPoint(sketch, "E2.33.10.0", {"position": v(1032.1, -291.13) * mm});
            skPoint(sketch, "E2.33.11.0", {"position": v(1032.1, -316.13) * mm});
            skPoint(sketch, "E2.33.12.0", {"position": v(1032.1, -341.13) * mm});
            skPoint(sketch, "E2.33.13.0", {"position": v(1032.1, -366.13) * mm});
            skPoint(sketch, "E2.33.14.0", {"position": v(1032.1, -391.13) * mm});
            skPoint(sketch, "E2.33.15.0", {"position": v(1032.1, -416.13) * mm});
            skPoint(sketch, "E2.33.16.0", {"position": v(1032.1, -441.13) * mm});
            skPoint(sketch, "E2.33.17.0", {"position": v(1032.1, -466.13) * mm});
            skPoint(sketch, "E2.33.18.0", {"position": v(1032.1, -491.13) * mm});
            skPoint(sketch, "E2.33.19.0", {"position": v(1032.1, -516.13) * mm});
            skPoint(sketch, "E2.33.20.0", {"position": v(1032.1, -541.13) * mm});
            skPoint(sketch, "E2.33.21.0", {"position": v(1032.1, -566.13) * mm});
            skPoint(sketch, "E2.33.22.0", {"position": v(1032.1, -591.13) * mm});
            skPoint(sketch, "E2.33.23.0", {"position": v(1032.1, -616.13) * mm});
            skPoint(sketch, "E2.33.24.0", {"position": v(1032.1, -641.13) * mm});
            skPoint(sketch, "E2.33.25.0", {"position": v(1032.1, -666.13) * mm});
            skPoint(sketch, "E2.33.26.0", {"position": v(1032.1, -691.13) * mm});
            skPoint(sketch, "E2.33.27.0", {"position": v(1032.1, -716.13) * mm});
            skPoint(sketch, "E2.33.28.0", {"position": v(1032.1, -741.13) * mm});
            skPoint(sketch, "E2.33.29.0", {"position": v(1032.1, -766.13) * mm});
            skPoint(sketch, "E2.33.30.0", {"position": v(1032.1, -791.13) * mm});
            skPoint(sketch, "E2.33.31.0", {"position": v(1032.1, -816.13) * mm});
            skPoint(sketch, "E2.33.32.0", {"position": v(1032.1, -841.13) * mm});
            skPoint(sketch, "E2.33.33.0", {"position": v(1032.1, -866.13) * mm});
            skPoint(sketch, "E2.33.34.0", {"position": v(1032.1, -891.13) * mm});
            skPoint(sketch, "E2.33.35.0", {"position": v(1032.1, -916.13) * mm});
            skPoint(sketch, "E2.33.36.0", {"position": v(1032.1, -941.13) * mm});
            skPoint(sketch, "E2.33.37.0", {"position": v(1032.1, -966.13) * mm});
            skPoint(sketch, "E2.33.38.0", {"position": v(1032.1, -991.13) * mm});
            skPoint(sketch, "E2.33.39.0", {"position": v(1032.1, -1016.13) * mm});
            skPoint(sketch, "E2.33.40.0", {"position": v(1032.1, -1041.13) * mm});
            skPoint(sketch, "E2.33.41.0", {"position": v(1032.1, -1066.13) * mm});
            skPoint(sketch, "E2.33.42.0", {"position": v(1032.1, -1091.13) * mm});
            skPoint(sketch, "E2.33.43.0", {"position": v(1032.1, -1116.13) * mm});
            skPoint(sketch, "E2.33.44.0", {"position": v(1032.1, -1141.13) * mm});
            skPoint(sketch, "E2.33.45.0", {"position": v(1032.1, -1166.13) * mm});
            skPoint(sketch, "E2.33.46.0", {"position": v(1032.1, -1191.13) * mm});
            skPoint(sketch, "E2.33.47.0", {"position": v(1032.1, -1216.13) * mm});
            skPoint(sketch, "E2.33.48.0", {"position": v(1032.1, -1241.13) * mm});
            skPoint(sketch, "E2.33.49.0", {"position": v(1032.1, -1266.13) * mm});
            skPoint(sketch, "E2.33.50.0", {"position": v(1032.1, -1291.13) * mm});
            skPoint(sketch, "E2.33.51.0", {"position": v(1032.1, -1316.13) * mm});
            skPoint(sketch, "E2.33.52.0", {"position": v(1032.1, -1341.13) * mm});
            skPoint(sketch, "E2.33.53.0", {"position": v(1032.1, -1366.13) * mm});
            skPoint(sketch, "E2.33.54.0", {"position": v(1032.1, -1391.13) * mm});
            skPoint(sketch, "E2.33.55.0", {"position": v(1032.1, -1416.13) * mm});
            skPoint(sketch, "E2.33.56.0", {"position": v(1032.1, -1441.13) * mm});
            skPoint(sketch, "E2.33.57.0", {"position": v(1032.1, -1466.13) * mm});
            skPoint(sketch, "E2.33.58.0", {"position": v(1032.1, -1491.13) * mm});
            skPoint(sketch, "E2.33.59.0", {"position": v(1032.1, -1516.13) * mm});
            skPoint(sketch, "E2.33.60.0", {"position": v(1032.1, -1541.13) * mm});
            skPoint(sketch, "E2.33.61.0", {"position": v(1032.1, -1566.13) * mm});
            skPoint(sketch, "E2.33.62.0", {"position": v(1032.1, -1591.13) * mm});
            skPoint(sketch, "E2.33.63.0", {"position": v(1032.1, -1616.13) * mm});
            skPoint(sketch, "E2.33.64.0", {"position": v(1032.1, -1641.13) * mm});
            skPoint(sketch, "E2.33.65.0", {"position": v(1032.1, -1666.13) * mm});
            skPoint(sketch, "E2.33.66.0", {"position": v(1032.1, -1691.13) * mm});
            skPoint(sketch, "E2.33.67.0", {"position": v(1032.1, -1716.13) * mm});
            skPoint(sketch, "E2.33.68.0", {"position": v(1032.1, -1741.13) * mm});
            skPoint(sketch, "E2.34.0.0", {"position": v(1062.1, -41.13) * mm});
            skPoint(sketch, "E2.34.1.0", {"position": v(1062.1, -66.13) * mm});
            skPoint(sketch, "E2.34.2.0", {"position": v(1062.1, -91.13) * mm});
            skPoint(sketch, "E2.34.3.0", {"position": v(1062.1, -116.13) * mm});
            skPoint(sketch, "E2.34.4.0", {"position": v(1062.1, -141.13) * mm});
            skPoint(sketch, "E2.34.5.0", {"position": v(1062.1, -166.13) * mm});
            skPoint(sketch, "E2.34.6.0", {"position": v(1062.1, -191.13) * mm});
            skPoint(sketch, "E2.34.7.0", {"position": v(1062.1, -216.13) * mm});
            skPoint(sketch, "E2.34.8.0", {"position": v(1062.1, -241.13) * mm});
            skPoint(sketch, "E2.34.9.0", {"position": v(1062.1, -266.13) * mm});
            skPoint(sketch, "E2.34.10.0", {"position": v(1062.1, -291.13) * mm});
            skPoint(sketch, "E2.34.11.0", {"position": v(1062.1, -316.13) * mm});
            skPoint(sketch, "E2.34.12.0", {"position": v(1062.1, -341.13) * mm});
            skPoint(sketch, "E2.34.13.0", {"position": v(1062.1, -366.13) * mm});
            skPoint(sketch, "E2.34.14.0", {"position": v(1062.1, -391.13) * mm});
            skPoint(sketch, "E2.34.15.0", {"position": v(1062.1, -416.13) * mm});
            skPoint(sketch, "E2.34.16.0", {"position": v(1062.1, -441.13) * mm});
            skPoint(sketch, "E2.34.17.0", {"position": v(1062.1, -466.13) * mm});
            skPoint(sketch, "E2.34.18.0", {"position": v(1062.1, -491.13) * mm});
            skPoint(sketch, "E2.34.19.0", {"position": v(1062.1, -516.13) * mm});
            skPoint(sketch, "E2.34.20.0", {"position": v(1062.1, -541.13) * mm});
            skPoint(sketch, "E2.34.21.0", {"position": v(1062.1, -566.13) * mm});
            skPoint(sketch, "E2.34.22.0", {"position": v(1062.1, -591.13) * mm});
            skPoint(sketch, "E2.34.23.0", {"position": v(1062.1, -616.13) * mm});
            skPoint(sketch, "E2.34.24.0", {"position": v(1062.1, -641.13) * mm});
            skPoint(sketch, "E2.34.25.0", {"position": v(1062.1, -666.13) * mm});
            skPoint(sketch, "E2.34.26.0", {"position": v(1062.1, -691.13) * mm});
            skPoint(sketch, "E2.34.27.0", {"position": v(1062.1, -716.13) * mm});
            skPoint(sketch, "E2.34.28.0", {"position": v(1062.1, -741.13) * mm});
            skPoint(sketch, "E2.34.29.0", {"position": v(1062.1, -766.13) * mm});
            skPoint(sketch, "E2.34.30.0", {"position": v(1062.1, -791.13) * mm});
            skPoint(sketch, "E2.34.31.0", {"position": v(1062.1, -816.13) * mm});
            skPoint(sketch, "E2.34.32.0", {"position": v(1062.1, -841.13) * mm});
            skPoint(sketch, "E2.34.33.0", {"position": v(1062.1, -866.13) * mm});
            skPoint(sketch, "E2.34.34.0", {"position": v(1062.1, -891.13) * mm});
            skPoint(sketch, "E2.34.35.0", {"position": v(1062.1, -916.13) * mm});
            skPoint(sketch, "E2.34.36.0", {"position": v(1062.1, -941.13) * mm});
            skPoint(sketch, "E2.34.37.0", {"position": v(1062.1, -966.13) * mm});
            skPoint(sketch, "E2.34.38.0", {"position": v(1062.1, -991.13) * mm});
            skPoint(sketch, "E2.34.39.0", {"position": v(1062.1, -1016.13) * mm});
            skPoint(sketch, "E2.34.40.0", {"position": v(1062.1, -1041.13) * mm});
            skPoint(sketch, "E2.34.41.0", {"position": v(1062.1, -1066.13) * mm});
            skPoint(sketch, "E2.34.42.0", {"position": v(1062.1, -1091.13) * mm});
            skPoint(sketch, "E2.34.43.0", {"position": v(1062.1, -1116.13) * mm});
            skPoint(sketch, "E2.34.44.0", {"position": v(1062.1, -1141.13) * mm});
            skPoint(sketch, "E2.34.45.0", {"position": v(1062.1, -1166.13) * mm});
            skPoint(sketch, "E2.34.46.0", {"position": v(1062.1, -1191.13) * mm});
            skPoint(sketch, "E2.34.47.0", {"position": v(1062.1, -1216.13) * mm});
            skPoint(sketch, "E2.34.48.0", {"position": v(1062.1, -1241.13) * mm});
            skPoint(sketch, "E2.34.49.0", {"position": v(1062.1, -1266.13) * mm});
            skPoint(sketch, "E2.34.50.0", {"position": v(1062.1, -1291.13) * mm});
            skPoint(sketch, "E2.34.51.0", {"position": v(1062.1, -1316.13) * mm});
            skPoint(sketch, "E2.34.52.0", {"position": v(1062.1, -1341.13) * mm});
            skPoint(sketch, "E2.34.53.0", {"position": v(1062.1, -1366.13) * mm});
            skPoint(sketch, "E2.34.54.0", {"position": v(1062.1, -1391.13) * mm});
            skPoint(sketch, "E2.34.55.0", {"position": v(1062.1, -1416.13) * mm});
            skPoint(sketch, "E2.34.56.0", {"position": v(1062.1, -1441.13) * mm});
            skPoint(sketch, "E2.34.57.0", {"position": v(1062.1, -1466.13) * mm});
            skPoint(sketch, "E2.34.58.0", {"position": v(1062.1, -1491.13) * mm});
            skPoint(sketch, "E2.34.59.0", {"position": v(1062.1, -1516.13) * mm});
            skPoint(sketch, "E2.34.60.0", {"position": v(1062.1, -1541.13) * mm});
            skPoint(sketch, "E2.34.61.0", {"position": v(1062.1, -1566.13) * mm});
            skPoint(sketch, "E2.34.62.0", {"position": v(1062.1, -1591.13) * mm});
            skPoint(sketch, "E2.34.63.0", {"position": v(1062.1, -1616.13) * mm});
            skPoint(sketch, "E2.34.64.0", {"position": v(1062.1, -1641.13) * mm});
            skPoint(sketch, "E2.34.65.0", {"position": v(1062.1, -1666.13) * mm});
            skPoint(sketch, "E2.34.66.0", {"position": v(1062.1, -1691.13) * mm});
            skPoint(sketch, "E2.34.67.0", {"position": v(1062.1, -1716.13) * mm});
            skPoint(sketch, "E2.34.68.0", {"position": v(1062.1, -1741.13) * mm});
            skPoint(sketch, "E2.35.0.0", {"position": v(1092.1, -41.13) * mm});
            skPoint(sketch, "E2.35.1.0", {"position": v(1092.1, -66.13) * mm});
            skPoint(sketch, "E2.35.2.0", {"position": v(1092.1, -91.13) * mm});
            skPoint(sketch, "E2.35.3.0", {"position": v(1092.1, -116.13) * mm});
            skPoint(sketch, "E2.35.4.0", {"position": v(1092.1, -141.13) * mm});
            skPoint(sketch, "E2.35.5.0", {"position": v(1092.1, -166.13) * mm});
            skPoint(sketch, "E2.35.6.0", {"position": v(1092.1, -191.13) * mm});
            skPoint(sketch, "E2.35.7.0", {"position": v(1092.1, -216.13) * mm});
            skPoint(sketch, "E2.35.8.0", {"position": v(1092.1, -241.13) * mm});
            skPoint(sketch, "E2.35.9.0", {"position": v(1092.1, -266.13) * mm});
            skPoint(sketch, "E2.35.10.0", {"position": v(1092.1, -291.13) * mm});
            skPoint(sketch, "E2.35.11.0", {"position": v(1092.1, -316.13) * mm});
            skPoint(sketch, "E2.35.12.0", {"position": v(1092.1, -341.13) * mm});
            skPoint(sketch, "E2.35.13.0", {"position": v(1092.1, -366.13) * mm});
            skPoint(sketch, "E2.35.14.0", {"position": v(1092.1, -391.13) * mm});
            skPoint(sketch, "E2.35.15.0", {"position": v(1092.1, -416.13) * mm});
            skPoint(sketch, "E2.35.16.0", {"position": v(1092.1, -441.13) * mm});
            skPoint(sketch, "E2.35.17.0", {"position": v(1092.1, -466.13) * mm});
            skPoint(sketch, "E2.35.18.0", {"position": v(1092.1, -491.13) * mm});
            skPoint(sketch, "E2.35.19.0", {"position": v(1092.1, -516.13) * mm});
            skPoint(sketch, "E2.35.20.0", {"position": v(1092.1, -541.13) * mm});
            skPoint(sketch, "E2.35.21.0", {"position": v(1092.1, -566.13) * mm});
            skPoint(sketch, "E2.35.22.0", {"position": v(1092.1, -591.13) * mm});
            skPoint(sketch, "E2.35.23.0", {"position": v(1092.1, -616.13) * mm});
            skPoint(sketch, "E2.35.24.0", {"position": v(1092.1, -641.13) * mm});
            skPoint(sketch, "E2.35.25.0", {"position": v(1092.1, -666.13) * mm});
            skPoint(sketch, "E2.35.26.0", {"position": v(1092.1, -691.13) * mm});
            skPoint(sketch, "E2.35.27.0", {"position": v(1092.1, -716.13) * mm});
            skPoint(sketch, "E2.35.28.0", {"position": v(1092.1, -741.13) * mm});
            skPoint(sketch, "E2.35.29.0", {"position": v(1092.1, -766.13) * mm});
            skPoint(sketch, "E2.35.30.0", {"position": v(1092.1, -791.13) * mm});
            skPoint(sketch, "E2.35.31.0", {"position": v(1092.1, -816.13) * mm});
            skPoint(sketch, "E2.35.32.0", {"position": v(1092.1, -841.13) * mm});
            skPoint(sketch, "E2.35.33.0", {"position": v(1092.1, -866.13) * mm});
            skPoint(sketch, "E2.35.34.0", {"position": v(1092.1, -891.13) * mm});
            skPoint(sketch, "E2.35.35.0", {"position": v(1092.1, -916.13) * mm});
            skPoint(sketch, "E2.35.36.0", {"position": v(1092.1, -941.13) * mm});
            skPoint(sketch, "E2.35.37.0", {"position": v(1092.1, -966.13) * mm});
            skPoint(sketch, "E2.35.38.0", {"position": v(1092.1, -991.13) * mm});
            skPoint(sketch, "E2.35.39.0", {"position": v(1092.1, -1016.13) * mm});
            skPoint(sketch, "E2.35.40.0", {"position": v(1092.1, -1041.13) * mm});
            skPoint(sketch, "E2.35.41.0", {"position": v(1092.1, -1066.13) * mm});
            skPoint(sketch, "E2.35.42.0", {"position": v(1092.1, -1091.13) * mm});
            skPoint(sketch, "E2.35.43.0", {"position": v(1092.1, -1116.13) * mm});
            skPoint(sketch, "E2.35.44.0", {"position": v(1092.1, -1141.13) * mm});
            skPoint(sketch, "E2.35.45.0", {"position": v(1092.1, -1166.13) * mm});
            skPoint(sketch, "E2.35.46.0", {"position": v(1092.1, -1191.13) * mm});
            skPoint(sketch, "E2.35.47.0", {"position": v(1092.1, -1216.13) * mm});
            skPoint(sketch, "E2.35.48.0", {"position": v(1092.1, -1241.13) * mm});
            skPoint(sketch, "E2.35.49.0", {"position": v(1092.1, -1266.13) * mm});
            skPoint(sketch, "E2.35.50.0", {"position": v(1092.1, -1291.13) * mm});
            skPoint(sketch, "E2.35.51.0", {"position": v(1092.1, -1316.13) * mm});
            skPoint(sketch, "E2.35.52.0", {"position": v(1092.1, -1341.13) * mm});
            skPoint(sketch, "E2.35.53.0", {"position": v(1092.1, -1366.13) * mm});
            skPoint(sketch, "E2.35.54.0", {"position": v(1092.1, -1391.13) * mm});
            skPoint(sketch, "E2.35.55.0", {"position": v(1092.1, -1416.13) * mm});
            skPoint(sketch, "E2.35.56.0", {"position": v(1092.1, -1441.13) * mm});
            skPoint(sketch, "E2.35.57.0", {"position": v(1092.1, -1466.13) * mm});
            skPoint(sketch, "E2.35.58.0", {"position": v(1092.1, -1491.13) * mm});
            skPoint(sketch, "E2.35.59.0", {"position": v(1092.1, -1516.13) * mm});
            skPoint(sketch, "E2.35.60.0", {"position": v(1092.1, -1541.13) * mm});
            skPoint(sketch, "E2.35.61.0", {"position": v(1092.1, -1566.13) * mm});
            skPoint(sketch, "E2.35.62.0", {"position": v(1092.1, -1591.13) * mm});
            skPoint(sketch, "E2.35.63.0", {"position": v(1092.1, -1616.13) * mm});
            skPoint(sketch, "E2.35.64.0", {"position": v(1092.1, -1641.13) * mm});
            skPoint(sketch, "E2.35.65.0", {"position": v(1092.1, -1666.13) * mm});
            skPoint(sketch, "E2.35.66.0", {"position": v(1092.1, -1691.13) * mm});
            skPoint(sketch, "E2.35.67.0", {"position": v(1092.1, -1716.13) * mm});
            skPoint(sketch, "E2.35.68.0", {"position": v(1092.1, -1741.13) * mm});
            skPoint(sketch, "E2.36.0.0", {"position": v(1122.1, -41.13) * mm});
            skPoint(sketch, "E2.36.1.0", {"position": v(1122.1, -66.13) * mm});
            skPoint(sketch, "E2.36.2.0", {"position": v(1122.1, -91.13) * mm});
            skPoint(sketch, "E2.36.3.0", {"position": v(1122.1, -116.13) * mm});
            skPoint(sketch, "E2.36.4.0", {"position": v(1122.1, -141.13) * mm});
            skPoint(sketch, "E2.36.5.0", {"position": v(1122.1, -166.13) * mm});
            skPoint(sketch, "E2.36.6.0", {"position": v(1122.1, -191.13) * mm});
            skPoint(sketch, "E2.36.7.0", {"position": v(1122.1, -216.13) * mm});
            skPoint(sketch, "E2.36.8.0", {"position": v(1122.1, -241.13) * mm});
            skPoint(sketch, "E2.36.9.0", {"position": v(1122.1, -266.13) * mm});
            skPoint(sketch, "E2.36.10.0", {"position": v(1122.1, -291.13) * mm});
            skPoint(sketch, "E2.36.11.0", {"position": v(1122.1, -316.13) * mm});
            skPoint(sketch, "E2.36.12.0", {"position": v(1122.1, -341.13) * mm});
            skPoint(sketch, "E2.36.13.0", {"position": v(1122.1, -366.13) * mm});
            skPoint(sketch, "E2.36.14.0", {"position": v(1122.1, -391.13) * mm});
            skPoint(sketch, "E2.36.15.0", {"position": v(1122.1, -416.13) * mm});
            skPoint(sketch, "E2.36.16.0", {"position": v(1122.1, -441.13) * mm});
            skPoint(sketch, "E2.36.17.0", {"position": v(1122.1, -466.13) * mm});
            skPoint(sketch, "E2.36.18.0", {"position": v(1122.1, -491.13) * mm});
            skPoint(sketch, "E2.36.19.0", {"position": v(1122.1, -516.13) * mm});
            skPoint(sketch, "E2.36.20.0", {"position": v(1122.1, -541.13) * mm});
            skPoint(sketch, "E2.36.21.0", {"position": v(1122.1, -566.13) * mm});
            skPoint(sketch, "E2.36.22.0", {"position": v(1122.1, -591.13) * mm});
            skPoint(sketch, "E2.36.23.0", {"position": v(1122.1, -616.13) * mm});
            skPoint(sketch, "E2.36.24.0", {"position": v(1122.1, -641.13) * mm});
            skPoint(sketch, "E2.36.25.0", {"position": v(1122.1, -666.13) * mm});
            skPoint(sketch, "E2.36.26.0", {"position": v(1122.1, -691.13) * mm});
            skPoint(sketch, "E2.36.27.0", {"position": v(1122.1, -716.13) * mm});
            skPoint(sketch, "E2.36.28.0", {"position": v(1122.1, -741.13) * mm});
            skPoint(sketch, "E2.36.29.0", {"position": v(1122.1, -766.13) * mm});
            skPoint(sketch, "E2.36.30.0", {"position": v(1122.1, -791.13) * mm});
            skPoint(sketch, "E2.36.31.0", {"position": v(1122.1, -816.13) * mm});
            skPoint(sketch, "E2.36.32.0", {"position": v(1122.1, -841.13) * mm});
            skPoint(sketch, "E2.36.33.0", {"position": v(1122.1, -866.13) * mm});
            skPoint(sketch, "E2.36.34.0", {"position": v(1122.1, -891.13) * mm});
            skPoint(sketch, "E2.36.35.0", {"position": v(1122.1, -916.13) * mm});
            skPoint(sketch, "E2.36.36.0", {"position": v(1122.1, -941.13) * mm});
            skPoint(sketch, "E2.36.37.0", {"position": v(1122.1, -966.13) * mm});
            skPoint(sketch, "E2.36.38.0", {"position": v(1122.1, -991.13) * mm});
            skPoint(sketch, "E2.36.39.0", {"position": v(1122.1, -1016.13) * mm});
            skPoint(sketch, "E2.36.40.0", {"position": v(1122.1, -1041.13) * mm});
            skPoint(sketch, "E2.36.41.0", {"position": v(1122.1, -1066.13) * mm});
            skPoint(sketch, "E2.36.42.0", {"position": v(1122.1, -1091.13) * mm});
            skPoint(sketch, "E2.36.43.0", {"position": v(1122.1, -1116.13) * mm});
            skPoint(sketch, "E2.36.44.0", {"position": v(1122.1, -1141.13) * mm});
            skPoint(sketch, "E2.36.45.0", {"position": v(1122.1, -1166.13) * mm});
            skPoint(sketch, "E2.36.46.0", {"position": v(1122.1, -1191.13) * mm});
            skPoint(sketch, "E2.36.47.0", {"position": v(1122.1, -1216.13) * mm});
            skPoint(sketch, "E2.36.48.0", {"position": v(1122.1, -1241.13) * mm});
            skPoint(sketch, "E2.36.49.0", {"position": v(1122.1, -1266.13) * mm});
            skPoint(sketch, "E2.36.50.0", {"position": v(1122.1, -1291.13) * mm});
            skPoint(sketch, "E2.36.51.0", {"position": v(1122.1, -1316.13) * mm});
            skPoint(sketch, "E2.36.52.0", {"position": v(1122.1, -1341.13) * mm});
            skPoint(sketch, "E2.36.53.0", {"position": v(1122.1, -1366.13) * mm});
            skPoint(sketch, "E2.36.54.0", {"position": v(1122.1, -1391.13) * mm});
            skPoint(sketch, "E2.36.55.0", {"position": v(1122.1, -1416.13) * mm});
            skPoint(sketch, "E2.36.56.0", {"position": v(1122.1, -1441.13) * mm});
            skPoint(sketch, "E2.36.57.0", {"position": v(1122.1, -1466.13) * mm});
            skPoint(sketch, "E2.36.58.0", {"position": v(1122.1, -1491.13) * mm});
            skPoint(sketch, "E2.36.59.0", {"position": v(1122.1, -1516.13) * mm});
            skPoint(sketch, "E2.36.60.0", {"position": v(1122.1, -1541.13) * mm});
            skPoint(sketch, "E2.36.61.0", {"position": v(1122.1, -1566.13) * mm});
            skPoint(sketch, "E2.36.62.0", {"position": v(1122.1, -1591.13) * mm});
            skPoint(sketch, "E2.36.63.0", {"position": v(1122.1, -1616.13) * mm});
            skPoint(sketch, "E2.36.64.0", {"position": v(1122.1, -1641.13) * mm});
            skPoint(sketch, "E2.36.65.0", {"position": v(1122.1, -1666.13) * mm});
            skPoint(sketch, "E2.36.66.0", {"position": v(1122.1, -1691.13) * mm});
            skPoint(sketch, "E2.36.67.0", {"position": v(1122.1, -1716.13) * mm});
            skPoint(sketch, "E2.36.68.0", {"position": v(1122.1, -1741.13) * mm});
            skPoint(sketch, "E2.37.0.0", {"position": v(1152.1, -41.13) * mm});
            skPoint(sketch, "E2.37.1.0", {"position": v(1152.1, -66.13) * mm});
            skPoint(sketch, "E2.37.2.0", {"position": v(1152.1, -91.13) * mm});
            skPoint(sketch, "E2.37.3.0", {"position": v(1152.1, -116.13) * mm});
            skPoint(sketch, "E2.37.4.0", {"position": v(1152.1, -141.13) * mm});
            skPoint(sketch, "E2.37.5.0", {"position": v(1152.1, -166.13) * mm});
            skPoint(sketch, "E2.37.6.0", {"position": v(1152.1, -191.13) * mm});
            skPoint(sketch, "E2.37.7.0", {"position": v(1152.1, -216.13) * mm});
            skPoint(sketch, "E2.37.8.0", {"position": v(1152.1, -241.13) * mm});
            skPoint(sketch, "E2.37.9.0", {"position": v(1152.1, -266.13) * mm});
            skPoint(sketch, "E2.37.10.0", {"position": v(1152.1, -291.13) * mm});
            skPoint(sketch, "E2.37.11.0", {"position": v(1152.1, -316.13) * mm});
            skPoint(sketch, "E2.37.12.0", {"position": v(1152.1, -341.13) * mm});
            skPoint(sketch, "E2.37.13.0", {"position": v(1152.1, -366.13) * mm});
            skPoint(sketch, "E2.37.14.0", {"position": v(1152.1, -391.13) * mm});
            skPoint(sketch, "E2.37.15.0", {"position": v(1152.1, -416.13) * mm});
            skPoint(sketch, "E2.37.16.0", {"position": v(1152.1, -441.13) * mm});
            skPoint(sketch, "E2.37.17.0", {"position": v(1152.1, -466.13) * mm});
            skPoint(sketch, "E2.37.18.0", {"position": v(1152.1, -491.13) * mm});
            skPoint(sketch, "E2.37.19.0", {"position": v(1152.1, -516.13) * mm});
            skPoint(sketch, "E2.37.20.0", {"position": v(1152.1, -541.13) * mm});
            skPoint(sketch, "E2.37.21.0", {"position": v(1152.1, -566.13) * mm});
            skPoint(sketch, "E2.37.22.0", {"position": v(1152.1, -591.13) * mm});
            skPoint(sketch, "E2.37.23.0", {"position": v(1152.1, -616.13) * mm});
            skPoint(sketch, "E2.37.24.0", {"position": v(1152.1, -641.13) * mm});
            skPoint(sketch, "E2.37.25.0", {"position": v(1152.1, -666.13) * mm});
            skPoint(sketch, "E2.37.26.0", {"position": v(1152.1, -691.13) * mm});
            skPoint(sketch, "E2.37.27.0", {"position": v(1152.1, -716.13) * mm});
            skPoint(sketch, "E2.37.28.0", {"position": v(1152.1, -741.13) * mm});
            skPoint(sketch, "E2.37.29.0", {"position": v(1152.1, -766.13) * mm});
            skPoint(sketch, "E2.37.30.0", {"position": v(1152.1, -791.13) * mm});
            skPoint(sketch, "E2.37.31.0", {"position": v(1152.1, -816.13) * mm});
            skPoint(sketch, "E2.37.32.0", {"position": v(1152.1, -841.13) * mm});
            skPoint(sketch, "E2.37.33.0", {"position": v(1152.1, -866.13) * mm});
            skPoint(sketch, "E2.37.34.0", {"position": v(1152.1, -891.13) * mm});
            skPoint(sketch, "E2.37.35.0", {"position": v(1152.1, -916.13) * mm});
            skPoint(sketch, "E2.37.36.0", {"position": v(1152.1, -941.13) * mm});
            skPoint(sketch, "E2.37.37.0", {"position": v(1152.1, -966.13) * mm});
            skPoint(sketch, "E2.37.38.0", {"position": v(1152.1, -991.13) * mm});
            skPoint(sketch, "E2.37.39.0", {"position": v(1152.1, -1016.13) * mm});
            skPoint(sketch, "E2.37.40.0", {"position": v(1152.1, -1041.13) * mm});
            skPoint(sketch, "E2.37.41.0", {"position": v(1152.1, -1066.13) * mm});
            skPoint(sketch, "E2.37.42.0", {"position": v(1152.1, -1091.13) * mm});
            skPoint(sketch, "E2.37.43.0", {"position": v(1152.1, -1116.13) * mm});
            skPoint(sketch, "E2.37.44.0", {"position": v(1152.1, -1141.13) * mm});
            skPoint(sketch, "E2.37.45.0", {"position": v(1152.1, -1166.13) * mm});
            skPoint(sketch, "E2.37.46.0", {"position": v(1152.1, -1191.13) * mm});
            skPoint(sketch, "E2.37.47.0", {"position": v(1152.1, -1216.13) * mm});
            skPoint(sketch, "E2.37.48.0", {"position": v(1152.1, -1241.13) * mm});
            skPoint(sketch, "E2.37.49.0", {"position": v(1152.1, -1266.13) * mm});
            skPoint(sketch, "E2.37.50.0", {"position": v(1152.1, -1291.13) * mm});
            skPoint(sketch, "E2.37.51.0", {"position": v(1152.1, -1316.13) * mm});
            skPoint(sketch, "E2.37.52.0", {"position": v(1152.1, -1341.13) * mm});
            skPoint(sketch, "E2.37.53.0", {"position": v(1152.1, -1366.13) * mm});
            skPoint(sketch, "E2.37.54.0", {"position": v(1152.1, -1391.13) * mm});
            skPoint(sketch, "E2.37.55.0", {"position": v(1152.1, -1416.13) * mm});
            skPoint(sketch, "E2.37.56.0", {"position": v(1152.1, -1441.13) * mm});
            skPoint(sketch, "E2.37.57.0", {"position": v(1152.1, -1466.13) * mm});
            skPoint(sketch, "E2.37.58.0", {"position": v(1152.1, -1491.13) * mm});
            skPoint(sketch, "E2.37.59.0", {"position": v(1152.1, -1516.13) * mm});
            skPoint(sketch, "E2.37.60.0", {"position": v(1152.1, -1541.13) * mm});
            skPoint(sketch, "E2.37.61.0", {"position": v(1152.1, -1566.13) * mm});
            skPoint(sketch, "E2.37.62.0", {"position": v(1152.1, -1591.13) * mm});
            skPoint(sketch, "E2.37.63.0", {"position": v(1152.1, -1616.13) * mm});
            skPoint(sketch, "E2.37.64.0", {"position": v(1152.1, -1641.13) * mm});
            skPoint(sketch, "E2.37.65.0", {"position": v(1152.1, -1666.13) * mm});
            skPoint(sketch, "E2.37.66.0", {"position": v(1152.1, -1691.13) * mm});
            skPoint(sketch, "E2.37.67.0", {"position": v(1152.1, -1716.13) * mm});
            skPoint(sketch, "E2.37.68.0", {"position": v(1152.1, -1741.13) * mm});
            skLineSegment(sketch, "E2.direction1", {"start": v(42.1, -41.13) * mm, "end": v(72.1, -41.13) * mm, "construction": true});
            skLineSegment(sketch, "E2.direction2", {"start": v(42.1, -41.13) * mm, "end": v(42.1, -66.13) * mm, "construction": true});
            skSolve(sketch);
        }
        {
            var Q0;
            Q0=sQuery(id+"F2.wireOp",VERTEX,"E1");
            var Q1;
            Q1=sQuery(id+"F2.wireOp",VERTEX,"E2.1.0.0");
            var Q2;
            Q2=sQuery(id+"F2.wireOp",VERTEX,"E2.2.0.0");
            var Q3;
            Q3=sQuery(id+"F2.wireOp",VERTEX,"E2.3.0.0");
            var Q4;
            Q4=sQuery(id+"F2.wireOp",VERTEX,"E2.4.0.0");
            var Q5;
            Q5=sQuery(id+"F2.wireOp",VERTEX,"E2.5.0.0");
            var Q6;
            Q6=sQuery(id+"F2.wireOp",VERTEX,"E2.6.0.0");
            var Q7;
            Q7=sQuery(id+"F2.wireOp",VERTEX,"E2.7.0.0");
            var Q8;
            Q8=sQuery(id+"F2.wireOp",VERTEX,"E2.8.0.0");
            var Q9;
            Q9=sQuery(id+"F2.wireOp",VERTEX,"E2.9.0.0");
            var Q10;
            Q10=sQuery(id+"F2.wireOp",VERTEX,"E2.10.0.0");
            var Q11;
            Q11=sQuery(id+"F2.wireOp",VERTEX,"E2.11.0.0");
            var Q12;
            Q12=sQuery(id+"F2.wireOp",VERTEX,"E2.12.0.0");
            var Q13;
            Q13=sQuery(id+"F2.wireOp",VERTEX,"E2.13.0.0");
            var Q14;
            Q14=sQuery(id+"F2.wireOp",VERTEX,"E2.14.0.0");
            var Q15;
            Q15=sQuery(id+"F2.wireOp",VERTEX,"E2.15.0.0");
            var Q16;
            Q16=sQuery(id+"F2.wireOp",VERTEX,"E2.16.0.0");
            var Q17;
            Q17=sQuery(id+"F2.wireOp",VERTEX,"E2.17.0.0");
            var Q18;
            Q18=sQuery(id+"F2.wireOp",VERTEX,"E2.18.0.0");
            var Q19;
            Q19=sQuery(id+"F2.wireOp",VERTEX,"E2.19.0.0");
            var Q20;
            Q20=sQuery(id+"F2.wireOp",VERTEX,"E2.20.0.0");
            var Q21;
            Q21=sQuery(id+"F2.wireOp",VERTEX,"E2.21.0.0");
            var Q22;
            Q22=sQuery(id+"F2.wireOp",VERTEX,"E2.22.0.0");
            var Q23;
            Q23=sQuery(id+"F2.wireOp",VERTEX,"E2.23.0.0");
            var Q24;
            Q24=sQuery(id+"F2.wireOp",VERTEX,"E2.24.0.0");
            var Q25;
            Q25=sQuery(id+"F2.wireOp",VERTEX,"E2.25.0.0");
            var Q26;
            Q26=sQuery(id+"F2.wireOp",VERTEX,"E2.26.0.0");
            var Q27;
            Q27=sQuery(id+"F2.wireOp",VERTEX,"E2.27.0.0");
            var Q28;
            Q28=sQuery(id+"F2.wireOp",VERTEX,"E2.28.0.0");
            var Q29;
            Q29=sQuery(id+"F2.wireOp",VERTEX,"E2.29.0.0");
            var Q30;
            Q30=sQuery(id+"F2.wireOp",VERTEX,"E2.30.0.0");
            var Q31;
            Q31=sQuery(id+"F2.wireOp",VERTEX,"E2.31.0.0");
            var Q32;
            Q32=sQuery(id+"F2.wireOp",VERTEX,"E2.32.0.0");
            var Q33;
            Q33=sQuery(id+"F2.wireOp",VERTEX,"E2.33.0.0");
            var Q34;
            Q34=sQuery(id+"F2.wireOp",VERTEX,"E2.34.0.0");
            var Q35;
            Q35=sQuery(id+"F2.wireOp",VERTEX,"E2.35.0.0");
            var Q36;
            Q36=sQuery(id+"F2.wireOp",VERTEX,"E2.36.0.0");
            var Q37;
            Q37=sQuery(id+"F2.wireOp",VERTEX,"E2.37.0.0");
            var Q38;
            Q38=makeQuery(id+"F1.opExtrude","SWEPT_BODY",BODY,{"disambiguationData":[OSD([sQuery(id+"F0.wireOp",EDGE,"E0.bottom"),sQuery(id+"F0.wireOp",EDGE,"E0.top"),sQuery(id+"F0.wireOp",EDGE,"E0.left"),sQuery(id+"F0.wireOp",EDGE,"E0.right")])]});
            hole(context, id + "F3", {"style" : HoleStyle.SIMPLE, "endStyle" : HoleEndStyle.THROUGH, "oppositeDirection" : true, "holeDiameter" : 20 * mm, "majorDiameter" : 5 * mm, "isTappedThrough" : true, "tappedDepth" : 12 * mm, "tapClearance" : 3, "locations" : qUnion([Q0, Q1, Q2, Q3, Q4, Q5, Q6, Q7, Q8, Q9, Q10, Q11, Q12, Q13, Q14, Q15, Q16, Q17, Q18, Q19, Q20, Q21, Q22, Q23, Q24, Q25, Q26, Q27, Q28, Q29, Q30, Q31, Q32, Q33, Q34, Q35, Q36, Q37]), "scope" : qUnion([Q38])});
        }
    });
